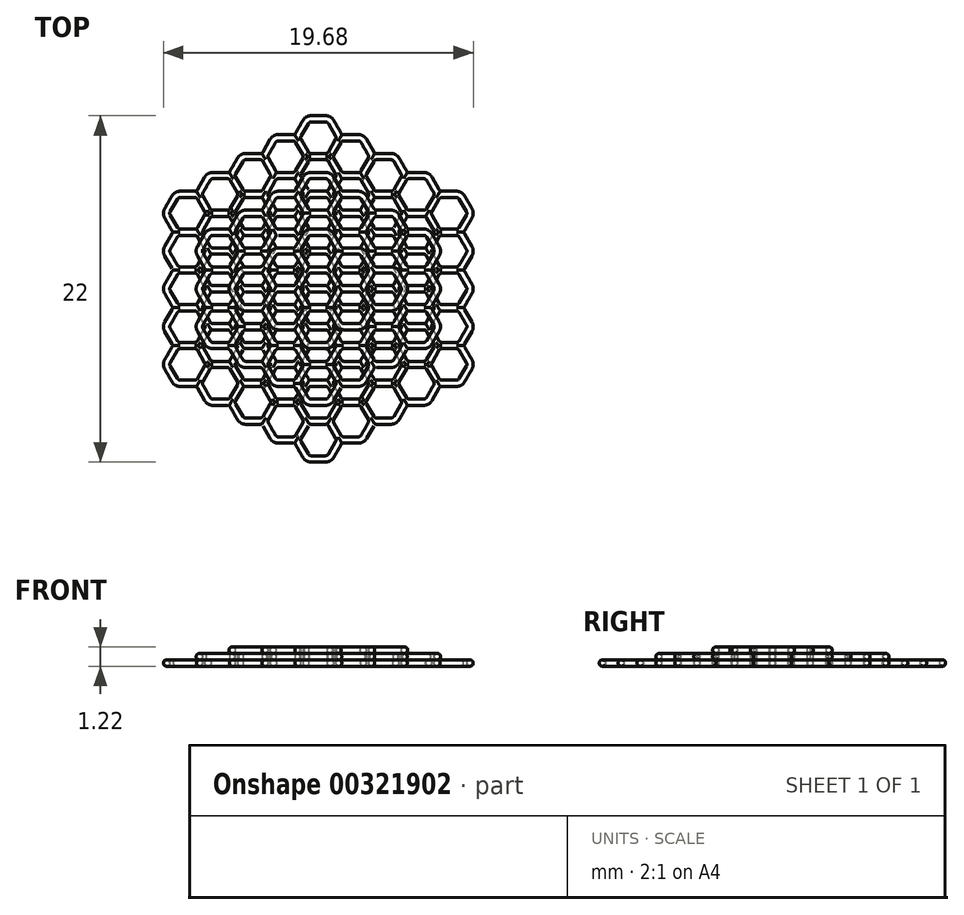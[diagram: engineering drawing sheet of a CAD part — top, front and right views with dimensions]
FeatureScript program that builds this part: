
annotation { "Feature Type Name" : "Feature", "Feature Type Description" : "" }
export const myFeature = defineFeature(function(context is Context, id is Id, definition is map)
    precondition{}
    {
        {
            var Q0;
            Q0=qCreatedBy(makeId("Top.planeOp"),FACE);
            cPlane(context, id + "F0", {"entities" : qUnion([Q0]), "cplaneType" : CPlaneType.OFFSET, "offset" : 0.2 * mm, "width" : 150 * mm, "height" : 150 * mm});
        }
        {
            var Q0;
            Q0=qCreatedBy(id+"F0.planeOp",FACE);
            var sketch = newSketch(context, id + "F1", { "sketchPlane" : qUnion([Q0])});
            skPoint(sketch, "E0.middle", {"position": v(0, 0) * mm});
            skLineSegment(sketch, "E1", {"start": v(-1.27, 0.2) * mm, "end": v(-0.8, 1) * mm});
            skLineSegment(sketch, "E2", {"start": v(-0.46, 1.2) * mm, "end": v(0.46, 1.2) * mm});
            skLineSegment(sketch, "E3", {"start": v(0.8, 1) * mm, "end": v(1.27, 0.2) * mm});
            skLineSegment(sketch, "E4", {"start": v(1.27, -0.2) * mm, "end": v(0.8, -1) * mm});
            skLineSegment(sketch, "E5", {"start": v(0.46, -1.2) * mm, "end": v(-0.46, -1.2) * mm});
            skLineSegment(sketch, "E6", {"start": v(-0.8, -1) * mm, "end": v(-1.27, -0.2) * mm});
            skArc(sketch, "E7.filletArc", {"start": v(-0.46, 1.2) * mm, "mid": v(-0.66, 1.15) * mm, "end": v(-0.8, 1) * mm});
            skArc(sketch, "E8.filletArc", {"start": v(0.8, 1) * mm, "mid": v(0.66, 1.15) * mm, "end": v(0.46, 1.2) * mm});
            skArc(sketch, "E9.filletArc", {"start": v(1.27, -0.2) * mm, "mid": v(1.32, 0) * mm, "end": v(1.27, 0.2) * mm});
            skArc(sketch, "E10.filletArc", {"start": v(0.46, -1.2) * mm, "mid": v(0.66, -1.15) * mm, "end": v(0.8, -1) * mm});
            skArc(sketch, "E11.filletArc", {"start": v(-0.8, -1) * mm, "mid": v(-0.66, -1.15) * mm, "end": v(-0.46, -1.2) * mm});
            skArc(sketch, "E12.filletArc", {"start": v(-1.27, 0.2) * mm, "mid": v(-1.32, 0) * mm, "end": v(-1.27, -0.2) * mm});
            skLineSegment(sketch, "E13", {"start": v(0.8, 1.4) * mm, "end": v(1.27, 2.2) * mm});
            skLineSegment(sketch, "E14", {"start": v(1.62, 2.4) * mm, "end": v(2.54, 2.4) * mm});
            skLineSegment(sketch, "E15", {"start": v(2.89, 2.2) * mm, "end": v(3.35, 1.4) * mm});
            skLineSegment(sketch, "E16", {"start": v(3.35, 1) * mm, "end": v(2.89, 0.2) * mm});
            skLineSegment(sketch, "E17", {"start": v(2.54, 0) * mm, "end": v(1.62, 0) * mm});
            skLineSegment(sketch, "E18", {"start": v(1.27, 0.2) * mm, "end": v(0.8, 1) * mm});
            skArc(sketch, "E19.filletArc", {"start": v(1.62, 2.4) * mm, "mid": v(1.42, 2.35) * mm, "end": v(1.27, 2.2) * mm});
            skArc(sketch, "E20.filletArc", {"start": v(2.89, 2.2) * mm, "mid": v(2.74, 2.35) * mm, "end": v(2.54, 2.4) * mm});
            skArc(sketch, "E21.filletArc", {"start": v(3.35, 1) * mm, "mid": v(3.4, 1.2) * mm, "end": v(3.35, 1.4) * mm});
            skArc(sketch, "E22.filletArc", {"start": v(2.54, 0) * mm, "mid": v(2.74, 0.05) * mm, "end": v(2.89, 0.2) * mm});
            skArc(sketch, "E23.filletArc", {"start": v(1.27, 0.2) * mm, "mid": v(1.42, 0.05) * mm, "end": v(1.62, 0) * mm});
            skArc(sketch, "E24.filletArc", {"start": v(0.8, 1.4) * mm, "mid": v(0.75, 1.2) * mm, "end": v(0.8, 1) * mm});
            skLineSegment(sketch, "E25", {"start": v(-1.27, 2.6) * mm, "end": v(-0.8, 3.4) * mm});
            skLineSegment(sketch, "E26", {"start": v(-0.46, 3.6) * mm, "end": v(0.46, 3.6) * mm});
            skLineSegment(sketch, "E27", {"start": v(0.8, 3.4) * mm, "end": v(1.27, 2.6) * mm});
            skLineSegment(sketch, "E28", {"start": v(1.27, 2.2) * mm, "end": v(0.8, 1.4) * mm});
            skLineSegment(sketch, "E29", {"start": v(0.46, 1.2) * mm, "end": v(-0.46, 1.2) * mm});
            skLineSegment(sketch, "E30", {"start": v(-0.8, 1.4) * mm, "end": v(-1.27, 2.2) * mm});
            skArc(sketch, "E31.filletArc", {"start": v(-0.46, 3.6) * mm, "mid": v(-0.66, 3.55) * mm, "end": v(-0.8, 3.4) * mm});
            skArc(sketch, "E32.filletArc", {"start": v(0.8, 3.4) * mm, "mid": v(0.66, 3.55) * mm, "end": v(0.46, 3.6) * mm});
            skArc(sketch, "E33.filletArc", {"start": v(1.27, 2.2) * mm, "mid": v(1.32, 2.4) * mm, "end": v(1.27, 2.6) * mm});
            skArc(sketch, "E34.filletArc", {"start": v(0.46, 1.2) * mm, "mid": v(0.66, 1.25) * mm, "end": v(0.8, 1.4) * mm});
            skArc(sketch, "E35.filletArc", {"start": v(-0.8, 1.4) * mm, "mid": v(-0.66, 1.25) * mm, "end": v(-0.46, 1.2) * mm});
            skArc(sketch, "E36.filletArc", {"start": v(-1.27, 2.6) * mm, "mid": v(-1.32, 2.4) * mm, "end": v(-1.27, 2.2) * mm});
            skLineSegment(sketch, "E37", {"start": v(-3.35, 1.4) * mm, "end": v(-2.89, 2.2) * mm});
            skLineSegment(sketch, "E38", {"start": v(-2.54, 2.4) * mm, "end": v(-1.62, 2.4) * mm});
            skLineSegment(sketch, "E39", {"start": v(-1.27, 2.2) * mm, "end": v(-0.8, 1.4) * mm});
            skLineSegment(sketch, "E40", {"start": v(-0.8, 1) * mm, "end": v(-1.27, 0.2) * mm});
            skLineSegment(sketch, "E41", {"start": v(-1.62, 0) * mm, "end": v(-2.54, 0) * mm});
            skLineSegment(sketch, "E42", {"start": v(-2.89, 0.2) * mm, "end": v(-3.35, 1) * mm});
            skArc(sketch, "E43.filletArc", {"start": v(-2.54, 2.4) * mm, "mid": v(-2.74, 2.35) * mm, "end": v(-2.89, 2.2) * mm});
            skArc(sketch, "E44.filletArc", {"start": v(-1.27, 2.2) * mm, "mid": v(-1.42, 2.35) * mm, "end": v(-1.62, 2.4) * mm});
            skArc(sketch, "E45.filletArc", {"start": v(-0.8, 1) * mm, "mid": v(-0.75, 1.2) * mm, "end": v(-0.8, 1.4) * mm});
            skArc(sketch, "E46.filletArc", {"start": v(-1.62, 0) * mm, "mid": v(-1.42, 0.05) * mm, "end": v(-1.27, 0.2) * mm});
            skArc(sketch, "E47.filletArc", {"start": v(-2.89, 0.2) * mm, "mid": v(-2.74, 0.05) * mm, "end": v(-2.54, 0) * mm});
            skArc(sketch, "E48.filletArc", {"start": v(-3.35, 1.4) * mm, "mid": v(-3.4, 1.2) * mm, "end": v(-3.35, 1) * mm});
            skLineSegment(sketch, "E49", {"start": v(-3.35, -1) * mm, "end": v(-2.89, -0.2) * mm});
            skLineSegment(sketch, "E50", {"start": v(-2.54, 0) * mm, "end": v(-1.62, 0) * mm});
            skLineSegment(sketch, "E51", {"start": v(-1.27, -0.2) * mm, "end": v(-0.8, -1) * mm});
            skLineSegment(sketch, "E52", {"start": v(-0.8, -1.4) * mm, "end": v(-1.27, -2.2) * mm});
            skLineSegment(sketch, "E53", {"start": v(-1.62, -2.4) * mm, "end": v(-2.54, -2.4) * mm});
            skLineSegment(sketch, "E54", {"start": v(-2.89, -2.2) * mm, "end": v(-3.35, -1.4) * mm});
            skArc(sketch, "E55.filletArc", {"start": v(-2.54, 0) * mm, "mid": v(-2.74, -0.05) * mm, "end": v(-2.89, -0.2) * mm});
            skArc(sketch, "E56.filletArc", {"start": v(-1.27, -0.2) * mm, "mid": v(-1.42, -0.05) * mm, "end": v(-1.62, 0) * mm});
            skArc(sketch, "E57.filletArc", {"start": v(-0.8, -1.4) * mm, "mid": v(-0.75, -1.2) * mm, "end": v(-0.8, -1) * mm});
            skArc(sketch, "E58.filletArc", {"start": v(-1.62, -2.4) * mm, "mid": v(-1.42, -2.35) * mm, "end": v(-1.27, -2.2) * mm});
            skArc(sketch, "E59.filletArc", {"start": v(-2.89, -2.2) * mm, "mid": v(-2.74, -2.35) * mm, "end": v(-2.54, -2.4) * mm});
            skArc(sketch, "E60.filletArc", {"start": v(-3.35, -1) * mm, "mid": v(-3.4, -1.2) * mm, "end": v(-3.35, -1.4) * mm});
            skLineSegment(sketch, "E61", {"start": v(-1.27, -2.2) * mm, "end": v(-0.8, -1.4) * mm});
            skLineSegment(sketch, "E62", {"start": v(-0.46, -1.2) * mm, "end": v(0.46, -1.2) * mm});
            skLineSegment(sketch, "E63", {"start": v(0.8, -1.4) * mm, "end": v(1.27, -2.2) * mm});
            skLineSegment(sketch, "E64", {"start": v(1.27, -2.6) * mm, "end": v(0.8, -3.4) * mm});
            skLineSegment(sketch, "E65", {"start": v(0.46, -3.6) * mm, "end": v(-0.46, -3.6) * mm});
            skLineSegment(sketch, "E66", {"start": v(-0.8, -3.4) * mm, "end": v(-1.27, -2.6) * mm});
            skArc(sketch, "E67.filletArc", {"start": v(-0.46, -1.2) * mm, "mid": v(-0.66, -1.25) * mm, "end": v(-0.8, -1.4) * mm});
            skArc(sketch, "E68.filletArc", {"start": v(0.8, -1.4) * mm, "mid": v(0.66, -1.25) * mm, "end": v(0.46, -1.2) * mm});
            skArc(sketch, "E69.filletArc", {"start": v(1.27, -2.6) * mm, "mid": v(1.32, -2.4) * mm, "end": v(1.27, -2.2) * mm});
            skArc(sketch, "E70.filletArc", {"start": v(0.46, -3.6) * mm, "mid": v(0.66, -3.55) * mm, "end": v(0.8, -3.4) * mm});
            skArc(sketch, "E71.filletArc", {"start": v(-0.8, -3.4) * mm, "mid": v(-0.66, -3.55) * mm, "end": v(-0.46, -3.6) * mm});
            skArc(sketch, "E72.filletArc", {"start": v(-1.27, -2.2) * mm, "mid": v(-1.32, -2.4) * mm, "end": v(-1.27, -2.6) * mm});
            skLineSegment(sketch, "E73", {"start": v(0.8, -1) * mm, "end": v(1.27, -0.2) * mm});
            skLineSegment(sketch, "E74", {"start": v(1.62, 0) * mm, "end": v(2.54, 0) * mm});
            skLineSegment(sketch, "E75", {"start": v(2.89, -0.2) * mm, "end": v(3.35, -1) * mm});
            skLineSegment(sketch, "E76", {"start": v(3.35, -1.4) * mm, "end": v(2.89, -2.2) * mm});
            skLineSegment(sketch, "E77", {"start": v(2.54, -2.4) * mm, "end": v(1.62, -2.4) * mm});
            skLineSegment(sketch, "E78", {"start": v(1.27, -2.2) * mm, "end": v(0.8, -1.4) * mm});
            skArc(sketch, "E79.filletArc", {"start": v(1.62, 0) * mm, "mid": v(1.42, -0.05) * mm, "end": v(1.27, -0.2) * mm});
            skArc(sketch, "E80.filletArc", {"start": v(2.89, -0.2) * mm, "mid": v(2.74, -0.05) * mm, "end": v(2.54, 0) * mm});
            skArc(sketch, "E81.filletArc", {"start": v(3.35, -1.4) * mm, "mid": v(3.4, -1.2) * mm, "end": v(3.35, -1) * mm});
            skArc(sketch, "E82.filletArc", {"start": v(2.54, -2.4) * mm, "mid": v(2.74, -2.35) * mm, "end": v(2.89, -2.2) * mm});
            skArc(sketch, "E83.filletArc", {"start": v(1.27, -2.2) * mm, "mid": v(1.42, -2.35) * mm, "end": v(1.62, -2.4) * mm});
            skArc(sketch, "E84.filletArc", {"start": v(0.8, -1) * mm, "mid": v(0.75, -1.2) * mm, "end": v(0.8, -1.4) * mm});
            skLineSegment(sketch, "E85", {"start": v(2.89, 2.6) * mm, "end": v(3.35, 3.4) * mm});
            skLineSegment(sketch, "E86", {"start": v(3.7, 3.6) * mm, "end": v(4.62, 3.6) * mm});
            skLineSegment(sketch, "E87", {"start": v(4.97, 3.4) * mm, "end": v(5.43, 2.6) * mm});
            skLineSegment(sketch, "E88", {"start": v(5.43, 2.2) * mm, "end": v(4.97, 1.4) * mm});
            skLineSegment(sketch, "E89", {"start": v(4.62, 1.2) * mm, "end": v(3.7, 1.2) * mm});
            skLineSegment(sketch, "E90", {"start": v(3.35, 1.4) * mm, "end": v(2.89, 2.2) * mm});
            skArc(sketch, "E91.filletArc", {"start": v(3.7, 3.6) * mm, "mid": v(3.5, 3.55) * mm, "end": v(3.35, 3.4) * mm});
            skArc(sketch, "E92.filletArc", {"start": v(4.97, 3.4) * mm, "mid": v(4.82, 3.55) * mm, "end": v(4.62, 3.6) * mm});
            skArc(sketch, "E93.filletArc", {"start": v(5.43, 2.2) * mm, "mid": v(5.48, 2.4) * mm, "end": v(5.43, 2.6) * mm});
            skArc(sketch, "E94.filletArc", {"start": v(4.62, 1.2) * mm, "mid": v(4.82, 1.25) * mm, "end": v(4.97, 1.4) * mm});
            skArc(sketch, "E95.filletArc", {"start": v(3.35, 1.4) * mm, "mid": v(3.5, 1.25) * mm, "end": v(3.7, 1.2) * mm});
            skArc(sketch, "E96.filletArc", {"start": v(2.89, 2.6) * mm, "mid": v(2.83, 2.4) * mm, "end": v(2.89, 2.2) * mm});
            skLineSegment(sketch, "E97", {"start": v(0.8, 3.8) * mm, "end": v(1.27, 4.6) * mm});
            skLineSegment(sketch, "E98", {"start": v(1.62, 4.8) * mm, "end": v(2.54, 4.8) * mm});
            skLineSegment(sketch, "E99", {"start": v(2.89, 4.6) * mm, "end": v(3.35, 3.8) * mm});
            skLineSegment(sketch, "E100", {"start": v(3.35, 3.4) * mm, "end": v(2.89, 2.6) * mm});
            skLineSegment(sketch, "E101", {"start": v(2.54, 2.4) * mm, "end": v(1.62, 2.4) * mm});
            skLineSegment(sketch, "E102", {"start": v(1.27, 2.6) * mm, "end": v(0.8, 3.4) * mm});
            skArc(sketch, "E103.filletArc", {"start": v(1.62, 4.8) * mm, "mid": v(1.42, 4.75) * mm, "end": v(1.27, 4.6) * mm});
            skArc(sketch, "E104.filletArc", {"start": v(2.89, 4.6) * mm, "mid": v(2.74, 4.75) * mm, "end": v(2.54, 4.8) * mm});
            skArc(sketch, "E105.filletArc", {"start": v(3.35, 3.4) * mm, "mid": v(3.4, 3.6) * mm, "end": v(3.35, 3.8) * mm});
            skArc(sketch, "E106.filletArc", {"start": v(2.54, 2.4) * mm, "mid": v(2.74, 2.45) * mm, "end": v(2.89, 2.6) * mm});
            skArc(sketch, "E107.filletArc", {"start": v(1.27, 2.6) * mm, "mid": v(1.42, 2.45) * mm, "end": v(1.62, 2.4) * mm});
            skArc(sketch, "E108.filletArc", {"start": v(0.8, 3.8) * mm, "mid": v(0.75, 3.6) * mm, "end": v(0.8, 3.4) * mm});
            skLineSegment(sketch, "E109", {"start": v(2.89, 0.2) * mm, "end": v(3.35, 1) * mm});
            skLineSegment(sketch, "E110", {"start": v(3.7, 1.2) * mm, "end": v(4.62, 1.2) * mm});
            skLineSegment(sketch, "E111", {"start": v(4.97, 1) * mm, "end": v(5.43, 0.2) * mm});
            skLineSegment(sketch, "E112", {"start": v(5.43, -0.2) * mm, "end": v(4.97, -1) * mm});
            skLineSegment(sketch, "E113", {"start": v(4.62, -1.2) * mm, "end": v(3.7, -1.2) * mm});
            skLineSegment(sketch, "E114", {"start": v(3.35, -1) * mm, "end": v(2.89, -0.2) * mm});
            skArc(sketch, "E115.filletArc", {"start": v(3.7, 1.2) * mm, "mid": v(3.5, 1.15) * mm, "end": v(3.35, 1) * mm});
            skArc(sketch, "E116.filletArc", {"start": v(4.97, 1) * mm, "mid": v(4.82, 1.15) * mm, "end": v(4.62, 1.2) * mm});
            skArc(sketch, "E117.filletArc", {"start": v(5.43, -0.2) * mm, "mid": v(5.48, 0) * mm, "end": v(5.43, 0.2) * mm});
            skArc(sketch, "E118.filletArc", {"start": v(4.62, -1.2) * mm, "mid": v(4.82, -1.15) * mm, "end": v(4.97, -1) * mm});
            skArc(sketch, "E119.filletArc", {"start": v(3.35, -1) * mm, "mid": v(3.5, -1.15) * mm, "end": v(3.7, -1.2) * mm});
            skArc(sketch, "E120.filletArc", {"start": v(2.89, 0.2) * mm, "mid": v(2.83, 0) * mm, "end": v(2.89, -0.2) * mm});
            skLineSegment(sketch, "E121", {"start": v(2.89, -2.2) * mm, "end": v(3.35, -1.4) * mm});
            skLineSegment(sketch, "E122", {"start": v(3.7, -1.2) * mm, "end": v(4.62, -1.2) * mm});
            skLineSegment(sketch, "E123", {"start": v(4.97, -1.4) * mm, "end": v(5.43, -2.2) * mm});
            skLineSegment(sketch, "E124", {"start": v(5.43, -2.6) * mm, "end": v(4.97, -3.4) * mm});
            skLineSegment(sketch, "E125", {"start": v(4.62, -3.6) * mm, "end": v(3.7, -3.6) * mm});
            skLineSegment(sketch, "E126", {"start": v(3.35, -3.4) * mm, "end": v(2.89, -2.6) * mm});
            skArc(sketch, "E127.filletArc", {"start": v(3.7, -1.2) * mm, "mid": v(3.5, -1.25) * mm, "end": v(3.35, -1.4) * mm});
            skArc(sketch, "E128.filletArc", {"start": v(4.97, -1.4) * mm, "mid": v(4.82, -1.25) * mm, "end": v(4.62, -1.2) * mm});
            skArc(sketch, "E129.filletArc", {"start": v(5.43, -2.6) * mm, "mid": v(5.48, -2.4) * mm, "end": v(5.43, -2.2) * mm});
            skArc(sketch, "E130.filletArc", {"start": v(4.62, -3.6) * mm, "mid": v(4.82, -3.55) * mm, "end": v(4.97, -3.4) * mm});
            skArc(sketch, "E131.filletArc", {"start": v(3.35, -3.4) * mm, "mid": v(3.5, -3.55) * mm, "end": v(3.7, -3.6) * mm});
            skArc(sketch, "E132.filletArc", {"start": v(2.89, -2.2) * mm, "mid": v(2.83, -2.4) * mm, "end": v(2.89, -2.6) * mm});
            skLineSegment(sketch, "E133", {"start": v(0.8, -3.4) * mm, "end": v(1.27, -2.6) * mm});
            skLineSegment(sketch, "E134", {"start": v(1.62, -2.4) * mm, "end": v(2.54, -2.4) * mm});
            skLineSegment(sketch, "E135", {"start": v(2.89, -2.6) * mm, "end": v(3.35, -3.4) * mm});
            skLineSegment(sketch, "E136", {"start": v(3.35, -3.8) * mm, "end": v(2.89, -4.6) * mm});
            skLineSegment(sketch, "E137", {"start": v(2.54, -4.8) * mm, "end": v(1.62, -4.8) * mm});
            skLineSegment(sketch, "E138", {"start": v(1.27, -4.6) * mm, "end": v(0.8, -3.8) * mm});
            skArc(sketch, "E139.filletArc", {"start": v(1.62, -2.4) * mm, "mid": v(1.42, -2.45) * mm, "end": v(1.27, -2.6) * mm});
            skArc(sketch, "E140.filletArc", {"start": v(2.89, -2.6) * mm, "mid": v(2.74, -2.45) * mm, "end": v(2.54, -2.4) * mm});
            skArc(sketch, "E141.filletArc", {"start": v(3.35, -3.8) * mm, "mid": v(3.4, -3.6) * mm, "end": v(3.35, -3.4) * mm});
            skArc(sketch, "E142.filletArc", {"start": v(2.54, -4.8) * mm, "mid": v(2.74, -4.75) * mm, "end": v(2.89, -4.6) * mm});
            skArc(sketch, "E143.filletArc", {"start": v(1.27, -4.6) * mm, "mid": v(1.42, -4.75) * mm, "end": v(1.62, -4.8) * mm});
            skArc(sketch, "E144.filletArc", {"start": v(0.8, -3.4) * mm, "mid": v(0.75, -3.6) * mm, "end": v(0.8, -3.8) * mm});
            skLineSegment(sketch, "E145", {"start": v(-1.27, -4.6) * mm, "end": v(-0.8, -3.8) * mm});
            skLineSegment(sketch, "E146", {"start": v(-0.46, -3.6) * mm, "end": v(0.46, -3.6) * mm});
            skLineSegment(sketch, "E147", {"start": v(0.8, -3.8) * mm, "end": v(1.27, -4.6) * mm});
            skLineSegment(sketch, "E148", {"start": v(1.27, -5) * mm, "end": v(0.8, -5.8) * mm});
            skLineSegment(sketch, "E149", {"start": v(0.46, -6) * mm, "end": v(-0.46, -6) * mm});
            skLineSegment(sketch, "E150", {"start": v(-0.8, -5.8) * mm, "end": v(-1.27, -5) * mm});
            skArc(sketch, "E151.filletArc", {"start": v(-0.46, -3.6) * mm, "mid": v(-0.66, -3.65) * mm, "end": v(-0.8, -3.8) * mm});
            skArc(sketch, "E152.filletArc", {"start": v(0.8, -3.8) * mm, "mid": v(0.66, -3.65) * mm, "end": v(0.46, -3.6) * mm});
            skArc(sketch, "E153.filletArc", {"start": v(1.27, -5) * mm, "mid": v(1.32, -4.8) * mm, "end": v(1.27, -4.6) * mm});
            skArc(sketch, "E154.filletArc", {"start": v(0.46, -6) * mm, "mid": v(0.66, -5.95) * mm, "end": v(0.8, -5.8) * mm});
            skArc(sketch, "E155.filletArc", {"start": v(-0.8, -5.8) * mm, "mid": v(-0.66, -5.95) * mm, "end": v(-0.46, -6) * mm});
            skArc(sketch, "E156.filletArc", {"start": v(-1.27, -4.6) * mm, "mid": v(-1.32, -4.8) * mm, "end": v(-1.27, -5) * mm});
            skLineSegment(sketch, "E157", {"start": v(-3.35, -3.4) * mm, "end": v(-2.89, -2.6) * mm});
            skLineSegment(sketch, "E158", {"start": v(-2.54, -2.4) * mm, "end": v(-1.62, -2.4) * mm});
            skLineSegment(sketch, "E159", {"start": v(-1.27, -2.6) * mm, "end": v(-0.8, -3.4) * mm});
            skLineSegment(sketch, "E160", {"start": v(-0.8, -3.8) * mm, "end": v(-1.27, -4.6) * mm});
            skLineSegment(sketch, "E161", {"start": v(-1.62, -4.8) * mm, "end": v(-2.54, -4.8) * mm});
            skLineSegment(sketch, "E162", {"start": v(-2.89, -4.6) * mm, "end": v(-3.35, -3.8) * mm});
            skArc(sketch, "E163.filletArc", {"start": v(-2.54, -2.4) * mm, "mid": v(-2.74, -2.45) * mm, "end": v(-2.89, -2.6) * mm});
            skArc(sketch, "E164.filletArc", {"start": v(-1.27, -2.6) * mm, "mid": v(-1.42, -2.45) * mm, "end": v(-1.62, -2.4) * mm});
            skArc(sketch, "E165.filletArc", {"start": v(-0.8, -3.8) * mm, "mid": v(-0.75, -3.6) * mm, "end": v(-0.8, -3.4) * mm});
            skArc(sketch, "E166.filletArc", {"start": v(-1.62, -4.8) * mm, "mid": v(-1.42, -4.75) * mm, "end": v(-1.27, -4.6) * mm});
            skArc(sketch, "E167.filletArc", {"start": v(-2.89, -4.6) * mm, "mid": v(-2.74, -4.75) * mm, "end": v(-2.54, -4.8) * mm});
            skArc(sketch, "E168.filletArc", {"start": v(-3.35, -3.4) * mm, "mid": v(-3.4, -3.6) * mm, "end": v(-3.35, -3.8) * mm});
            skLineSegment(sketch, "E169", {"start": v(-5.43, -2.2) * mm, "end": v(-4.97, -1.4) * mm});
            skLineSegment(sketch, "E170", {"start": v(-4.62, -1.2) * mm, "end": v(-3.7, -1.2) * mm});
            skLineSegment(sketch, "E171", {"start": v(-3.35, -1.4) * mm, "end": v(-2.89, -2.2) * mm});
            skLineSegment(sketch, "E172", {"start": v(-2.89, -2.6) * mm, "end": v(-3.35, -3.4) * mm});
            skLineSegment(sketch, "E173", {"start": v(-3.7, -3.6) * mm, "end": v(-4.62, -3.6) * mm});
            skLineSegment(sketch, "E174", {"start": v(-4.97, -3.4) * mm, "end": v(-5.43, -2.6) * mm});
            skArc(sketch, "E175.filletArc", {"start": v(-4.62, -1.2) * mm, "mid": v(-4.82, -1.25) * mm, "end": v(-4.97, -1.4) * mm});
            skArc(sketch, "E176.filletArc", {"start": v(-3.35, -1.4) * mm, "mid": v(-3.5, -1.25) * mm, "end": v(-3.7, -1.2) * mm});
            skArc(sketch, "E177.filletArc", {"start": v(-2.89, -2.6) * mm, "mid": v(-2.83, -2.4) * mm, "end": v(-2.89, -2.2) * mm});
            skArc(sketch, "E178.filletArc", {"start": v(-3.7, -3.6) * mm, "mid": v(-3.5, -3.55) * mm, "end": v(-3.35, -3.4) * mm});
            skArc(sketch, "E179.filletArc", {"start": v(-4.97, -3.4) * mm, "mid": v(-4.82, -3.55) * mm, "end": v(-4.62, -3.6) * mm});
            skArc(sketch, "E180.filletArc", {"start": v(-5.43, -2.2) * mm, "mid": v(-5.48, -2.4) * mm, "end": v(-5.43, -2.6) * mm});
            skLineSegment(sketch, "E181", {"start": v(-5.43, 0.2) * mm, "end": v(-4.97, 1) * mm});
            skLineSegment(sketch, "E182", {"start": v(-4.62, 1.2) * mm, "end": v(-3.7, 1.2) * mm});
            skLineSegment(sketch, "E183", {"start": v(-3.35, 1) * mm, "end": v(-2.89, 0.2) * mm});
            skLineSegment(sketch, "E184", {"start": v(-2.89, -0.2) * mm, "end": v(-3.35, -1) * mm});
            skLineSegment(sketch, "E185", {"start": v(-3.7, -1.2) * mm, "end": v(-4.62, -1.2) * mm});
            skLineSegment(sketch, "E186", {"start": v(-4.97, -1) * mm, "end": v(-5.43, -0.2) * mm});
            skArc(sketch, "E187.filletArc", {"start": v(-4.62, 1.2) * mm, "mid": v(-4.82, 1.15) * mm, "end": v(-4.97, 1) * mm});
            skArc(sketch, "E188.filletArc", {"start": v(-3.35, 1) * mm, "mid": v(-3.5, 1.15) * mm, "end": v(-3.7, 1.2) * mm});
            skArc(sketch, "E189.filletArc", {"start": v(-2.89, -0.2) * mm, "mid": v(-2.83, 0) * mm, "end": v(-2.89, 0.2) * mm});
            skArc(sketch, "E190.filletArc", {"start": v(-3.7, -1.2) * mm, "mid": v(-3.5, -1.15) * mm, "end": v(-3.35, -1) * mm});
            skArc(sketch, "E191.filletArc", {"start": v(-4.97, -1) * mm, "mid": v(-4.82, -1.15) * mm, "end": v(-4.62, -1.2) * mm});
            skArc(sketch, "E192.filletArc", {"start": v(-5.43, 0.2) * mm, "mid": v(-5.48, 0) * mm, "end": v(-5.43, -0.2) * mm});
            skLineSegment(sketch, "E193", {"start": v(-5.43, 2.6) * mm, "end": v(-4.97, 3.4) * mm});
            skLineSegment(sketch, "E194", {"start": v(-4.62, 3.6) * mm, "end": v(-3.7, 3.6) * mm});
            skLineSegment(sketch, "E195", {"start": v(-3.35, 3.4) * mm, "end": v(-2.89, 2.6) * mm});
            skLineSegment(sketch, "E196", {"start": v(-2.89, 2.2) * mm, "end": v(-3.35, 1.4) * mm});
            skLineSegment(sketch, "E197", {"start": v(-3.7, 1.2) * mm, "end": v(-4.62, 1.2) * mm});
            skLineSegment(sketch, "E198", {"start": v(-4.97, 1.4) * mm, "end": v(-5.43, 2.2) * mm});
            skArc(sketch, "E199.filletArc", {"start": v(-4.62, 3.6) * mm, "mid": v(-4.82, 3.55) * mm, "end": v(-4.97, 3.4) * mm});
            skArc(sketch, "E200.filletArc", {"start": v(-3.35, 3.4) * mm, "mid": v(-3.5, 3.55) * mm, "end": v(-3.7, 3.6) * mm});
            skArc(sketch, "E201.filletArc", {"start": v(-2.89, 2.2) * mm, "mid": v(-2.83, 2.4) * mm, "end": v(-2.89, 2.6) * mm});
            skArc(sketch, "E202.filletArc", {"start": v(-3.7, 1.2) * mm, "mid": v(-3.5, 1.25) * mm, "end": v(-3.35, 1.4) * mm});
            skArc(sketch, "E203.filletArc", {"start": v(-4.97, 1.4) * mm, "mid": v(-4.82, 1.25) * mm, "end": v(-4.62, 1.2) * mm});
            skArc(sketch, "E204.filletArc", {"start": v(-5.43, 2.6) * mm, "mid": v(-5.48, 2.4) * mm, "end": v(-5.43, 2.2) * mm});
            skLineSegment(sketch, "E205", {"start": v(-3.35, 3.8) * mm, "end": v(-2.89, 4.6) * mm});
            skLineSegment(sketch, "E206", {"start": v(-2.54, 4.8) * mm, "end": v(-1.62, 4.8) * mm});
            skLineSegment(sketch, "E207", {"start": v(-1.27, 4.6) * mm, "end": v(-0.8, 3.8) * mm});
            skLineSegment(sketch, "E208", {"start": v(-0.8, 3.4) * mm, "end": v(-1.27, 2.6) * mm});
            skLineSegment(sketch, "E209", {"start": v(-1.62, 2.4) * mm, "end": v(-2.54, 2.4) * mm});
            skLineSegment(sketch, "E210", {"start": v(-2.89, 2.6) * mm, "end": v(-3.35, 3.4) * mm});
            skArc(sketch, "E211.filletArc", {"start": v(-2.54, 4.8) * mm, "mid": v(-2.74, 4.75) * mm, "end": v(-2.89, 4.6) * mm});
            skArc(sketch, "E212.filletArc", {"start": v(-1.27, 4.6) * mm, "mid": v(-1.42, 4.75) * mm, "end": v(-1.62, 4.8) * mm});
            skArc(sketch, "E213.filletArc", {"start": v(-0.8, 3.4) * mm, "mid": v(-0.75, 3.6) * mm, "end": v(-0.8, 3.8) * mm});
            skArc(sketch, "E214.filletArc", {"start": v(-1.62, 2.4) * mm, "mid": v(-1.42, 2.45) * mm, "end": v(-1.27, 2.6) * mm});
            skArc(sketch, "E215.filletArc", {"start": v(-2.89, 2.6) * mm, "mid": v(-2.74, 2.45) * mm, "end": v(-2.54, 2.4) * mm});
            skArc(sketch, "E216.filletArc", {"start": v(-3.35, 3.8) * mm, "mid": v(-3.4, 3.6) * mm, "end": v(-3.35, 3.4) * mm});
            skLineSegment(sketch, "E217", {"start": v(-1.27, 5) * mm, "end": v(-0.8, 5.8) * mm});
            skLineSegment(sketch, "E218", {"start": v(-0.46, 6) * mm, "end": v(0.46, 6) * mm});
            skLineSegment(sketch, "E219", {"start": v(0.8, 5.8) * mm, "end": v(1.27, 5) * mm});
            skLineSegment(sketch, "E220", {"start": v(1.27, 4.6) * mm, "end": v(0.8, 3.8) * mm});
            skLineSegment(sketch, "E221", {"start": v(0.46, 3.6) * mm, "end": v(-0.46, 3.6) * mm});
            skLineSegment(sketch, "E222", {"start": v(-0.8, 3.8) * mm, "end": v(-1.27, 4.6) * mm});
            skArc(sketch, "E223.filletArc", {"start": v(-0.46, 6) * mm, "mid": v(-0.66, 5.95) * mm, "end": v(-0.8, 5.8) * mm});
            skArc(sketch, "E224.filletArc", {"start": v(0.8, 5.8) * mm, "mid": v(0.66, 5.95) * mm, "end": v(0.46, 6) * mm});
            skArc(sketch, "E225.filletArc", {"start": v(1.27, 4.6) * mm, "mid": v(1.32, 4.8) * mm, "end": v(1.27, 5) * mm});
            skArc(sketch, "E226.filletArc", {"start": v(0.46, 3.6) * mm, "mid": v(0.66, 3.65) * mm, "end": v(0.8, 3.8) * mm});
            skArc(sketch, "E227.filletArc", {"start": v(-0.8, 3.8) * mm, "mid": v(-0.66, 3.65) * mm, "end": v(-0.46, 3.6) * mm});
            skArc(sketch, "E228.filletArc", {"start": v(-1.27, 5) * mm, "mid": v(-1.32, 4.8) * mm, "end": v(-1.27, 4.6) * mm});
            skLineSegment(sketch, "E229", {"start": v(2.89, 5) * mm, "end": v(3.35, 5.8) * mm});
            skLineSegment(sketch, "E230", {"start": v(3.7, 6) * mm, "end": v(4.62, 6) * mm});
            skLineSegment(sketch, "E231", {"start": v(4.97, 5.8) * mm, "end": v(5.43, 5) * mm});
            skLineSegment(sketch, "E232", {"start": v(5.43, 4.6) * mm, "end": v(4.97, 3.8) * mm});
            skLineSegment(sketch, "E233", {"start": v(4.62, 3.6) * mm, "end": v(3.7, 3.6) * mm});
            skLineSegment(sketch, "E234", {"start": v(3.35, 3.8) * mm, "end": v(2.89, 4.6) * mm});
            skArc(sketch, "E235.filletArc", {"start": v(3.7, 6) * mm, "mid": v(3.5, 5.95) * mm, "end": v(3.35, 5.8) * mm});
            skArc(sketch, "E236.filletArc", {"start": v(4.97, 5.8) * mm, "mid": v(4.82, 5.95) * mm, "end": v(4.62, 6) * mm});
            skArc(sketch, "E237.filletArc", {"start": v(5.43, 4.6) * mm, "mid": v(5.48, 4.8) * mm, "end": v(5.43, 5) * mm});
            skArc(sketch, "E238.filletArc", {"start": v(4.62, 3.6) * mm, "mid": v(4.82, 3.65) * mm, "end": v(4.97, 3.8) * mm});
            skArc(sketch, "E239.filletArc", {"start": v(3.35, 3.8) * mm, "mid": v(3.5, 3.65) * mm, "end": v(3.7, 3.6) * mm});
            skArc(sketch, "E240.filletArc", {"start": v(2.89, 5) * mm, "mid": v(2.83, 4.8) * mm, "end": v(2.89, 4.6) * mm});
            skLineSegment(sketch, "E241", {"start": v(0.8, 6.2) * mm, "end": v(1.27, 7) * mm});
            skLineSegment(sketch, "E242", {"start": v(1.62, 7.2) * mm, "end": v(2.54, 7.2) * mm});
            skLineSegment(sketch, "E243", {"start": v(2.89, 7) * mm, "end": v(3.35, 6.2) * mm});
            skLineSegment(sketch, "E244", {"start": v(3.35, 5.8) * mm, "end": v(2.89, 5) * mm});
            skLineSegment(sketch, "E245", {"start": v(2.54, 4.8) * mm, "end": v(1.62, 4.8) * mm});
            skLineSegment(sketch, "E246", {"start": v(1.27, 5) * mm, "end": v(0.8, 5.8) * mm});
            skArc(sketch, "E247.filletArc", {"start": v(1.62, 7.2) * mm, "mid": v(1.42, 7.15) * mm, "end": v(1.27, 7) * mm});
            skArc(sketch, "E248.filletArc", {"start": v(2.89, 7) * mm, "mid": v(2.74, 7.15) * mm, "end": v(2.54, 7.2) * mm});
            skArc(sketch, "E249.filletArc", {"start": v(3.35, 5.8) * mm, "mid": v(3.4, 6) * mm, "end": v(3.35, 6.2) * mm});
            skArc(sketch, "E250.filletArc", {"start": v(2.54, 4.8) * mm, "mid": v(2.74, 4.85) * mm, "end": v(2.89, 5) * mm});
            skArc(sketch, "E251.filletArc", {"start": v(1.27, 5) * mm, "mid": v(1.42, 4.85) * mm, "end": v(1.62, 4.8) * mm});
            skArc(sketch, "E252.filletArc", {"start": v(0.8, 6.2) * mm, "mid": v(0.75, 6) * mm, "end": v(0.8, 5.8) * mm});
            skLineSegment(sketch, "E253", {"start": v(-1.27, 7.4) * mm, "end": v(-0.8, 8.2) * mm});
            skLineSegment(sketch, "E254", {"start": v(-0.46, 8.4) * mm, "end": v(0.46, 8.4) * mm});
            skLineSegment(sketch, "E255", {"start": v(0.8, 8.2) * mm, "end": v(1.27, 7.4) * mm});
            skLineSegment(sketch, "E256", {"start": v(1.27, 7) * mm, "end": v(0.8, 6.2) * mm});
            skLineSegment(sketch, "E257", {"start": v(0.46, 6) * mm, "end": v(-0.46, 6) * mm});
            skLineSegment(sketch, "E258", {"start": v(-0.8, 6.2) * mm, "end": v(-1.27, 7) * mm});
            skArc(sketch, "E259.filletArc", {"start": v(-0.46, 8.4) * mm, "mid": v(-0.66, 8.35) * mm, "end": v(-0.8, 8.2) * mm});
            skArc(sketch, "E260.filletArc", {"start": v(0.8, 8.2) * mm, "mid": v(0.66, 8.35) * mm, "end": v(0.46, 8.4) * mm});
            skArc(sketch, "E261.filletArc", {"start": v(1.27, 7) * mm, "mid": v(1.32, 7.2) * mm, "end": v(1.27, 7.4) * mm});
            skArc(sketch, "E262.filletArc", {"start": v(0.46, 6) * mm, "mid": v(0.66, 6.05) * mm, "end": v(0.8, 6.2) * mm});
            skArc(sketch, "E263.filletArc", {"start": v(-0.8, 6.2) * mm, "mid": v(-0.66, 6.05) * mm, "end": v(-0.46, 6) * mm});
            skArc(sketch, "E264.filletArc", {"start": v(-1.27, 7.4) * mm, "mid": v(-1.32, 7.2) * mm, "end": v(-1.27, 7) * mm});
            skLineSegment(sketch, "E265", {"start": v(-3.35, 6.2) * mm, "end": v(-2.89, 7) * mm});
            skLineSegment(sketch, "E266", {"start": v(-2.54, 7.2) * mm, "end": v(-1.62, 7.2) * mm});
            skLineSegment(sketch, "E267", {"start": v(-1.27, 7) * mm, "end": v(-0.8, 6.2) * mm});
            skLineSegment(sketch, "E268", {"start": v(-0.8, 5.8) * mm, "end": v(-1.27, 5) * mm});
            skLineSegment(sketch, "E269", {"start": v(-1.62, 4.8) * mm, "end": v(-2.54, 4.8) * mm});
            skLineSegment(sketch, "E270", {"start": v(-2.89, 5) * mm, "end": v(-3.35, 5.8) * mm});
            skArc(sketch, "E271.filletArc", {"start": v(-2.54, 7.2) * mm, "mid": v(-2.74, 7.15) * mm, "end": v(-2.89, 7) * mm});
            skArc(sketch, "E272.filletArc", {"start": v(-1.27, 7) * mm, "mid": v(-1.42, 7.15) * mm, "end": v(-1.62, 7.2) * mm});
            skArc(sketch, "E273.filletArc", {"start": v(-0.8, 5.8) * mm, "mid": v(-0.75, 6) * mm, "end": v(-0.8, 6.2) * mm});
            skArc(sketch, "E274.filletArc", {"start": v(-1.62, 4.8) * mm, "mid": v(-1.42, 4.85) * mm, "end": v(-1.27, 5) * mm});
            skArc(sketch, "E275.filletArc", {"start": v(-2.89, 5) * mm, "mid": v(-2.74, 4.85) * mm, "end": v(-2.54, 4.8) * mm});
            skArc(sketch, "E276.filletArc", {"start": v(-3.35, 6.2) * mm, "mid": v(-3.4, 6) * mm, "end": v(-3.35, 5.8) * mm});
            skLineSegment(sketch, "E277", {"start": v(-5.43, 5) * mm, "end": v(-4.97, 5.8) * mm});
            skLineSegment(sketch, "E278", {"start": v(-4.62, 6) * mm, "end": v(-3.7, 6) * mm});
            skLineSegment(sketch, "E279", {"start": v(-3.35, 5.8) * mm, "end": v(-2.89, 5) * mm});
            skLineSegment(sketch, "E280", {"start": v(-2.89, 4.6) * mm, "end": v(-3.35, 3.8) * mm});
            skLineSegment(sketch, "E281", {"start": v(-3.7, 3.6) * mm, "end": v(-4.62, 3.6) * mm});
            skLineSegment(sketch, "E282", {"start": v(-4.97, 3.8) * mm, "end": v(-5.43, 4.6) * mm});
            skArc(sketch, "E283.filletArc", {"start": v(-4.62, 6) * mm, "mid": v(-4.82, 5.95) * mm, "end": v(-4.97, 5.8) * mm});
            skArc(sketch, "E284.filletArc", {"start": v(-3.35, 5.8) * mm, "mid": v(-3.5, 5.95) * mm, "end": v(-3.7, 6) * mm});
            skArc(sketch, "E285.filletArc", {"start": v(-2.89, 4.6) * mm, "mid": v(-2.83, 4.8) * mm, "end": v(-2.89, 5) * mm});
            skArc(sketch, "E286.filletArc", {"start": v(-3.7, 3.6) * mm, "mid": v(-3.5, 3.65) * mm, "end": v(-3.35, 3.8) * mm});
            skArc(sketch, "E287.filletArc", {"start": v(-4.97, 3.8) * mm, "mid": v(-4.82, 3.65) * mm, "end": v(-4.62, 3.6) * mm});
            skArc(sketch, "E288.filletArc", {"start": v(-5.43, 5) * mm, "mid": v(-5.48, 4.8) * mm, "end": v(-5.43, 4.6) * mm});
            skLineSegment(sketch, "E289", {"start": v(-7.5, 3.8) * mm, "end": v(-7.04, 4.6) * mm});
            skLineSegment(sketch, "E290", {"start": v(-6.7, 4.8) * mm, "end": v(-5.77, 4.8) * mm});
            skLineSegment(sketch, "E291", {"start": v(-5.43, 4.6) * mm, "end": v(-4.97, 3.8) * mm});
            skLineSegment(sketch, "E292", {"start": v(-4.97, 3.4) * mm, "end": v(-5.43, 2.6) * mm});
            skLineSegment(sketch, "E293", {"start": v(-5.77, 2.4) * mm, "end": v(-6.7, 2.4) * mm});
            skLineSegment(sketch, "E294", {"start": v(-7.04, 2.6) * mm, "end": v(-7.5, 3.4) * mm});
            skArc(sketch, "E295.filletArc", {"start": v(-6.7, 4.8) * mm, "mid": v(-6.9, 4.75) * mm, "end": v(-7.04, 4.6) * mm});
            skArc(sketch, "E296.filletArc", {"start": v(-5.43, 4.6) * mm, "mid": v(-5.57, 4.75) * mm, "end": v(-5.77, 4.8) * mm});
            skArc(sketch, "E297.filletArc", {"start": v(-4.97, 3.4) * mm, "mid": v(-4.91, 3.6) * mm, "end": v(-4.97, 3.8) * mm});
            skArc(sketch, "E298.filletArc", {"start": v(-5.77, 2.4) * mm, "mid": v(-5.57, 2.45) * mm, "end": v(-5.43, 2.6) * mm});
            skArc(sketch, "E299.filletArc", {"start": v(-7.04, 2.6) * mm, "mid": v(-6.9, 2.45) * mm, "end": v(-6.7, 2.4) * mm});
            skArc(sketch, "E300.filletArc", {"start": v(-7.5, 3.8) * mm, "mid": v(-7.56, 3.6) * mm, "end": v(-7.5, 3.4) * mm});
            skLineSegment(sketch, "E301", {"start": v(-7.5, 1.4) * mm, "end": v(-7.04, 2.2) * mm});
            skLineSegment(sketch, "E302", {"start": v(-6.7, 2.4) * mm, "end": v(-5.77, 2.4) * mm});
            skLineSegment(sketch, "E303", {"start": v(-5.43, 2.2) * mm, "end": v(-4.97, 1.4) * mm});
            skLineSegment(sketch, "E304", {"start": v(-4.97, 1) * mm, "end": v(-5.43, 0.2) * mm});
            skLineSegment(sketch, "E305", {"start": v(-5.77, 0) * mm, "end": v(-6.7, 0) * mm});
            skLineSegment(sketch, "E306", {"start": v(-7.04, 0.2) * mm, "end": v(-7.5, 1) * mm});
            skArc(sketch, "E307.filletArc", {"start": v(-6.7, 2.4) * mm, "mid": v(-6.9, 2.35) * mm, "end": v(-7.04, 2.2) * mm});
            skArc(sketch, "E308.filletArc", {"start": v(-5.43, 2.2) * mm, "mid": v(-5.57, 2.35) * mm, "end": v(-5.77, 2.4) * mm});
            skArc(sketch, "E309.filletArc", {"start": v(-4.97, 1) * mm, "mid": v(-4.91, 1.2) * mm, "end": v(-4.97, 1.4) * mm});
            skArc(sketch, "E310.filletArc", {"start": v(-5.77, 0) * mm, "mid": v(-5.57, 0.05) * mm, "end": v(-5.43, 0.2) * mm});
            skArc(sketch, "E311.filletArc", {"start": v(-7.04, 0.2) * mm, "mid": v(-6.9, 0.05) * mm, "end": v(-6.7, 0) * mm});
            skArc(sketch, "E312.filletArc", {"start": v(-7.5, 1.4) * mm, "mid": v(-7.56, 1.2) * mm, "end": v(-7.5, 1) * mm});
            skLineSegment(sketch, "E313", {"start": v(-7.5, -1) * mm, "end": v(-7.04, -0.2) * mm});
            skLineSegment(sketch, "E314", {"start": v(-6.7, 0) * mm, "end": v(-5.77, 0) * mm});
            skLineSegment(sketch, "E315", {"start": v(-5.43, -0.2) * mm, "end": v(-4.97, -1) * mm});
            skLineSegment(sketch, "E316", {"start": v(-4.97, -1.4) * mm, "end": v(-5.43, -2.2) * mm});
            skLineSegment(sketch, "E317", {"start": v(-5.77, -2.4) * mm, "end": v(-6.7, -2.4) * mm});
            skLineSegment(sketch, "E318", {"start": v(-7.04, -2.2) * mm, "end": v(-7.5, -1.4) * mm});
            skArc(sketch, "E319.filletArc", {"start": v(-6.7, 0) * mm, "mid": v(-6.9, -0.05) * mm, "end": v(-7.04, -0.2) * mm});
            skArc(sketch, "E320.filletArc", {"start": v(-5.43, -0.2) * mm, "mid": v(-5.57, -0.05) * mm, "end": v(-5.77, 0) * mm});
            skArc(sketch, "E321.filletArc", {"start": v(-4.97, -1.4) * mm, "mid": v(-4.91, -1.2) * mm, "end": v(-4.97, -1) * mm});
            skArc(sketch, "E322.filletArc", {"start": v(-5.77, -2.4) * mm, "mid": v(-5.57, -2.35) * mm, "end": v(-5.43, -2.2) * mm});
            skArc(sketch, "E323.filletArc", {"start": v(-7.04, -2.2) * mm, "mid": v(-6.9, -2.35) * mm, "end": v(-6.7, -2.4) * mm});
            skArc(sketch, "E324.filletArc", {"start": v(-7.5, -1) * mm, "mid": v(-7.56, -1.2) * mm, "end": v(-7.5, -1.4) * mm});
            skLineSegment(sketch, "E325", {"start": v(-7.5, -3.4) * mm, "end": v(-7.04, -2.6) * mm});
            skLineSegment(sketch, "E326", {"start": v(-6.7, -2.4) * mm, "end": v(-5.77, -2.4) * mm});
            skLineSegment(sketch, "E327", {"start": v(-5.43, -2.6) * mm, "end": v(-4.97, -3.4) * mm});
            skLineSegment(sketch, "E328", {"start": v(-4.97, -3.8) * mm, "end": v(-5.43, -4.6) * mm});
            skLineSegment(sketch, "E329", {"start": v(-5.77, -4.8) * mm, "end": v(-6.7, -4.8) * mm});
            skLineSegment(sketch, "E330", {"start": v(-7.04, -4.6) * mm, "end": v(-7.5, -3.8) * mm});
            skArc(sketch, "E331.filletArc", {"start": v(-6.7, -2.4) * mm, "mid": v(-6.9, -2.45) * mm, "end": v(-7.04, -2.6) * mm});
            skArc(sketch, "E332.filletArc", {"start": v(-5.43, -2.6) * mm, "mid": v(-5.57, -2.45) * mm, "end": v(-5.77, -2.4) * mm});
            skArc(sketch, "E333.filletArc", {"start": v(-4.97, -3.8) * mm, "mid": v(-4.91, -3.6) * mm, "end": v(-4.97, -3.4) * mm});
            skArc(sketch, "E334.filletArc", {"start": v(-5.77, -4.8) * mm, "mid": v(-5.57, -4.75) * mm, "end": v(-5.43, -4.6) * mm});
            skArc(sketch, "E335.filletArc", {"start": v(-7.04, -4.6) * mm, "mid": v(-6.9, -4.75) * mm, "end": v(-6.7, -4.8) * mm});
            skArc(sketch, "E336.filletArc", {"start": v(-7.5, -3.4) * mm, "mid": v(-7.56, -3.6) * mm, "end": v(-7.5, -3.8) * mm});
            skLineSegment(sketch, "E337", {"start": v(-3.35, -5.8) * mm, "end": v(-2.89, -5) * mm});
            skLineSegment(sketch, "E338", {"start": v(-2.54, -4.8) * mm, "end": v(-1.62, -4.8) * mm});
            skLineSegment(sketch, "E339", {"start": v(-1.27, -5) * mm, "end": v(-0.8, -5.8) * mm});
            skLineSegment(sketch, "E340", {"start": v(-0.8, -6.2) * mm, "end": v(-1.27, -7) * mm});
            skLineSegment(sketch, "E341", {"start": v(-1.62, -7.2) * mm, "end": v(-2.54, -7.2) * mm});
            skLineSegment(sketch, "E342", {"start": v(-2.89, -7) * mm, "end": v(-3.35, -6.2) * mm});
            skArc(sketch, "E343.filletArc", {"start": v(-2.54, -4.8) * mm, "mid": v(-2.74, -4.85) * mm, "end": v(-2.89, -5) * mm});
            skArc(sketch, "E344.filletArc", {"start": v(-1.27, -5) * mm, "mid": v(-1.42, -4.85) * mm, "end": v(-1.62, -4.8) * mm});
            skArc(sketch, "E345.filletArc", {"start": v(-0.8, -6.2) * mm, "mid": v(-0.75, -6) * mm, "end": v(-0.8, -5.8) * mm});
            skArc(sketch, "E346.filletArc", {"start": v(-1.62, -7.2) * mm, "mid": v(-1.42, -7.15) * mm, "end": v(-1.27, -7) * mm});
            skArc(sketch, "E347.filletArc", {"start": v(-2.89, -7) * mm, "mid": v(-2.74, -7.15) * mm, "end": v(-2.54, -7.2) * mm});
            skArc(sketch, "E348.filletArc", {"start": v(-3.35, -5.8) * mm, "mid": v(-3.4, -6) * mm, "end": v(-3.35, -6.2) * mm});
            skLineSegment(sketch, "E349", {"start": v(-5.43, -4.6) * mm, "end": v(-4.97, -3.8) * mm});
            skLineSegment(sketch, "E350", {"start": v(-4.62, -3.6) * mm, "end": v(-3.7, -3.6) * mm});
            skLineSegment(sketch, "E351", {"start": v(-3.35, -3.8) * mm, "end": v(-2.89, -4.6) * mm});
            skLineSegment(sketch, "E352", {"start": v(-2.89, -5) * mm, "end": v(-3.35, -5.8) * mm});
            skLineSegment(sketch, "E353", {"start": v(-3.7, -6) * mm, "end": v(-4.62, -6) * mm});
            skLineSegment(sketch, "E354", {"start": v(-4.97, -5.8) * mm, "end": v(-5.43, -5) * mm});
            skArc(sketch, "E355.filletArc", {"start": v(-4.62, -3.6) * mm, "mid": v(-4.82, -3.65) * mm, "end": v(-4.97, -3.8) * mm});
            skArc(sketch, "E356.filletArc", {"start": v(-3.35, -3.8) * mm, "mid": v(-3.5, -3.65) * mm, "end": v(-3.7, -3.6) * mm});
            skArc(sketch, "E357.filletArc", {"start": v(-2.89, -5) * mm, "mid": v(-2.83, -4.8) * mm, "end": v(-2.89, -4.6) * mm});
            skArc(sketch, "E358.filletArc", {"start": v(-3.7, -6) * mm, "mid": v(-3.5, -5.95) * mm, "end": v(-3.35, -5.8) * mm});
            skArc(sketch, "E359.filletArc", {"start": v(-4.97, -5.8) * mm, "mid": v(-4.82, -5.95) * mm, "end": v(-4.62, -6) * mm});
            skArc(sketch, "E360.filletArc", {"start": v(-5.43, -4.6) * mm, "mid": v(-5.48, -4.8) * mm, "end": v(-5.43, -5) * mm});
            skLineSegment(sketch, "E361", {"start": v(-1.27, -7) * mm, "end": v(-0.8, -6.2) * mm});
            skLineSegment(sketch, "E362", {"start": v(-0.46, -6) * mm, "end": v(0.46, -6) * mm});
            skLineSegment(sketch, "E363", {"start": v(0.8, -6.2) * mm, "end": v(1.27, -7) * mm});
            skLineSegment(sketch, "E364", {"start": v(1.27, -7.4) * mm, "end": v(0.8, -8.2) * mm});
            skLineSegment(sketch, "E365", {"start": v(0.46, -8.4) * mm, "end": v(-0.46, -8.4) * mm});
            skLineSegment(sketch, "E366", {"start": v(-0.8, -8.2) * mm, "end": v(-1.27, -7.4) * mm});
            skArc(sketch, "E367.filletArc", {"start": v(-0.46, -6) * mm, "mid": v(-0.66, -6.05) * mm, "end": v(-0.8, -6.2) * mm});
            skArc(sketch, "E368.filletArc", {"start": v(0.8, -6.2) * mm, "mid": v(0.66, -6.05) * mm, "end": v(0.46, -6) * mm});
            skArc(sketch, "E369.filletArc", {"start": v(1.27, -7.4) * mm, "mid": v(1.32, -7.2) * mm, "end": v(1.27, -7) * mm});
            skArc(sketch, "E370.filletArc", {"start": v(0.46, -8.4) * mm, "mid": v(0.66, -8.35) * mm, "end": v(0.8, -8.2) * mm});
            skArc(sketch, "E371.filletArc", {"start": v(-0.8, -8.2) * mm, "mid": v(-0.66, -8.35) * mm, "end": v(-0.46, -8.4) * mm});
            skArc(sketch, "E372.filletArc", {"start": v(-1.27, -7) * mm, "mid": v(-1.32, -7.2) * mm, "end": v(-1.27, -7.4) * mm});
            skLineSegment(sketch, "E373", {"start": v(0.8, -5.8) * mm, "end": v(1.27, -5) * mm});
            skLineSegment(sketch, "E374", {"start": v(1.62, -4.8) * mm, "end": v(2.54, -4.8) * mm});
            skLineSegment(sketch, "E375", {"start": v(2.89, -5) * mm, "end": v(3.35, -5.8) * mm});
            skLineSegment(sketch, "E376", {"start": v(3.35, -6.2) * mm, "end": v(2.89, -7) * mm});
            skLineSegment(sketch, "E377", {"start": v(2.54, -7.2) * mm, "end": v(1.62, -7.2) * mm});
            skLineSegment(sketch, "E378", {"start": v(1.27, -7) * mm, "end": v(0.8, -6.2) * mm});
            skArc(sketch, "E379.filletArc", {"start": v(1.62, -4.8) * mm, "mid": v(1.42, -4.85) * mm, "end": v(1.27, -5) * mm});
            skArc(sketch, "E380.filletArc", {"start": v(2.89, -5) * mm, "mid": v(2.74, -4.85) * mm, "end": v(2.54, -4.8) * mm});
            skArc(sketch, "E381.filletArc", {"start": v(3.35, -6.2) * mm, "mid": v(3.4, -6) * mm, "end": v(3.35, -5.8) * mm});
            skArc(sketch, "E382.filletArc", {"start": v(2.54, -7.2) * mm, "mid": v(2.74, -7.15) * mm, "end": v(2.89, -7) * mm});
            skArc(sketch, "E383.filletArc", {"start": v(1.27, -7) * mm, "mid": v(1.42, -7.15) * mm, "end": v(1.62, -7.2) * mm});
            skArc(sketch, "E384.filletArc", {"start": v(0.8, -5.8) * mm, "mid": v(0.75, -6) * mm, "end": v(0.8, -6.2) * mm});
            skLineSegment(sketch, "E385", {"start": v(2.89, -4.6) * mm, "end": v(3.35, -3.8) * mm});
            skLineSegment(sketch, "E386", {"start": v(3.7, -3.6) * mm, "end": v(4.62, -3.6) * mm});
            skLineSegment(sketch, "E387", {"start": v(4.97, -3.8) * mm, "end": v(5.43, -4.6) * mm});
            skLineSegment(sketch, "E388", {"start": v(5.43, -5) * mm, "end": v(4.97, -5.8) * mm});
            skLineSegment(sketch, "E389", {"start": v(4.62, -6) * mm, "end": v(3.7, -6) * mm});
            skLineSegment(sketch, "E390", {"start": v(3.35, -5.8) * mm, "end": v(2.89, -5) * mm});
            skArc(sketch, "E391.filletArc", {"start": v(3.7, -3.6) * mm, "mid": v(3.5, -3.65) * mm, "end": v(3.35, -3.8) * mm});
            skArc(sketch, "E392.filletArc", {"start": v(4.97, -3.8) * mm, "mid": v(4.82, -3.65) * mm, "end": v(4.62, -3.6) * mm});
            skArc(sketch, "E393.filletArc", {"start": v(5.43, -5) * mm, "mid": v(5.48, -4.8) * mm, "end": v(5.43, -4.6) * mm});
            skArc(sketch, "E394.filletArc", {"start": v(4.62, -6) * mm, "mid": v(4.82, -5.95) * mm, "end": v(4.97, -5.8) * mm});
            skArc(sketch, "E395.filletArc", {"start": v(3.35, -5.8) * mm, "mid": v(3.5, -5.95) * mm, "end": v(3.7, -6) * mm});
            skArc(sketch, "E396.filletArc", {"start": v(2.89, -4.6) * mm, "mid": v(2.83, -4.8) * mm, "end": v(2.89, -5) * mm});
            skLineSegment(sketch, "E397", {"start": v(4.97, -3.4) * mm, "end": v(5.43, -2.6) * mm});
            skLineSegment(sketch, "E398", {"start": v(5.77, -2.4) * mm, "end": v(6.7, -2.4) * mm});
            skLineSegment(sketch, "E399", {"start": v(7.04, -2.6) * mm, "end": v(7.5, -3.4) * mm});
            skLineSegment(sketch, "E400", {"start": v(7.5, -3.8) * mm, "end": v(7.04, -4.6) * mm});
            skLineSegment(sketch, "E401", {"start": v(6.7, -4.8) * mm, "end": v(5.77, -4.8) * mm});
            skLineSegment(sketch, "E402", {"start": v(5.43, -4.6) * mm, "end": v(4.97, -3.8) * mm});
            skArc(sketch, "E403.filletArc", {"start": v(5.77, -2.4) * mm, "mid": v(5.57, -2.45) * mm, "end": v(5.43, -2.6) * mm});
            skArc(sketch, "E404.filletArc", {"start": v(7.04, -2.6) * mm, "mid": v(6.9, -2.45) * mm, "end": v(6.7, -2.4) * mm});
            skArc(sketch, "E405.filletArc", {"start": v(7.5, -3.8) * mm, "mid": v(7.56, -3.6) * mm, "end": v(7.5, -3.4) * mm});
            skArc(sketch, "E406.filletArc", {"start": v(6.7, -4.8) * mm, "mid": v(6.9, -4.75) * mm, "end": v(7.04, -4.6) * mm});
            skArc(sketch, "E407.filletArc", {"start": v(5.43, -4.6) * mm, "mid": v(5.57, -4.75) * mm, "end": v(5.77, -4.8) * mm});
            skArc(sketch, "E408.filletArc", {"start": v(4.97, -3.4) * mm, "mid": v(4.91, -3.6) * mm, "end": v(4.97, -3.8) * mm});
            skLineSegment(sketch, "E409", {"start": v(4.97, -1) * mm, "end": v(5.43, -0.2) * mm});
            skLineSegment(sketch, "E410", {"start": v(5.77, 0) * mm, "end": v(6.7, 0) * mm});
            skLineSegment(sketch, "E411", {"start": v(7.04, -0.2) * mm, "end": v(7.5, -1) * mm});
            skLineSegment(sketch, "E412", {"start": v(7.5, -1.4) * mm, "end": v(7.04, -2.2) * mm});
            skLineSegment(sketch, "E413", {"start": v(6.7, -2.4) * mm, "end": v(5.77, -2.4) * mm});
            skLineSegment(sketch, "E414", {"start": v(5.43, -2.2) * mm, "end": v(4.97, -1.4) * mm});
            skArc(sketch, "E415.filletArc", {"start": v(5.77, 0) * mm, "mid": v(5.57, -0.05) * mm, "end": v(5.43, -0.2) * mm});
            skArc(sketch, "E416.filletArc", {"start": v(7.04, -0.2) * mm, "mid": v(6.9, -0.05) * mm, "end": v(6.7, 0) * mm});
            skArc(sketch, "E417.filletArc", {"start": v(7.5, -1.4) * mm, "mid": v(7.56, -1.2) * mm, "end": v(7.5, -1) * mm});
            skArc(sketch, "E418.filletArc", {"start": v(6.7, -2.4) * mm, "mid": v(6.9, -2.35) * mm, "end": v(7.04, -2.2) * mm});
            skArc(sketch, "E419.filletArc", {"start": v(5.43, -2.2) * mm, "mid": v(5.57, -2.35) * mm, "end": v(5.77, -2.4) * mm});
            skArc(sketch, "E420.filletArc", {"start": v(4.97, -1) * mm, "mid": v(4.91, -1.2) * mm, "end": v(4.97, -1.4) * mm});
            skLineSegment(sketch, "E421", {"start": v(4.97, 1.4) * mm, "end": v(5.43, 2.2) * mm});
            skLineSegment(sketch, "E422", {"start": v(5.77, 2.4) * mm, "end": v(6.7, 2.4) * mm});
            skLineSegment(sketch, "E423", {"start": v(7.04, 2.2) * mm, "end": v(7.5, 1.4) * mm});
            skLineSegment(sketch, "E424", {"start": v(7.5, 1) * mm, "end": v(7.04, 0.2) * mm});
            skLineSegment(sketch, "E425", {"start": v(6.7, 0) * mm, "end": v(5.77, 0) * mm});
            skLineSegment(sketch, "E426", {"start": v(5.43, 0.2) * mm, "end": v(4.97, 1) * mm});
            skArc(sketch, "E427.filletArc", {"start": v(5.77, 2.4) * mm, "mid": v(5.57, 2.35) * mm, "end": v(5.43, 2.2) * mm});
            skArc(sketch, "E428.filletArc", {"start": v(7.04, 2.2) * mm, "mid": v(6.9, 2.35) * mm, "end": v(6.7, 2.4) * mm});
            skArc(sketch, "E429.filletArc", {"start": v(7.5, 1) * mm, "mid": v(7.56, 1.2) * mm, "end": v(7.5, 1.4) * mm});
            skArc(sketch, "E430.filletArc", {"start": v(6.7, 0) * mm, "mid": v(6.9, 0.05) * mm, "end": v(7.04, 0.2) * mm});
            skArc(sketch, "E431.filletArc", {"start": v(5.43, 0.2) * mm, "mid": v(5.57, 0.05) * mm, "end": v(5.77, 0) * mm});
            skArc(sketch, "E432.filletArc", {"start": v(4.97, 1.4) * mm, "mid": v(4.91, 1.2) * mm, "end": v(4.97, 1) * mm});
            skLineSegment(sketch, "E433", {"start": v(4.97, 3.8) * mm, "end": v(5.43, 4.6) * mm});
            skLineSegment(sketch, "E434", {"start": v(5.77, 4.8) * mm, "end": v(6.7, 4.8) * mm});
            skLineSegment(sketch, "E435", {"start": v(7.04, 4.6) * mm, "end": v(7.5, 3.8) * mm});
            skLineSegment(sketch, "E436", {"start": v(7.5, 3.4) * mm, "end": v(7.04, 2.6) * mm});
            skLineSegment(sketch, "E437", {"start": v(6.7, 2.4) * mm, "end": v(5.77, 2.4) * mm});
            skLineSegment(sketch, "E438", {"start": v(5.43, 2.6) * mm, "end": v(4.97, 3.4) * mm});
            skArc(sketch, "E439.filletArc", {"start": v(5.77, 4.8) * mm, "mid": v(5.57, 4.75) * mm, "end": v(5.43, 4.6) * mm});
            skArc(sketch, "E440.filletArc", {"start": v(7.04, 4.6) * mm, "mid": v(6.9, 4.75) * mm, "end": v(6.7, 4.8) * mm});
            skArc(sketch, "E441.filletArc", {"start": v(7.5, 3.4) * mm, "mid": v(7.56, 3.6) * mm, "end": v(7.5, 3.8) * mm});
            skArc(sketch, "E442.filletArc", {"start": v(6.7, 2.4) * mm, "mid": v(6.9, 2.45) * mm, "end": v(7.04, 2.6) * mm});
            skArc(sketch, "E443.filletArc", {"start": v(5.43, 2.6) * mm, "mid": v(5.57, 2.45) * mm, "end": v(5.77, 2.4) * mm});
            skArc(sketch, "E444.filletArc", {"start": v(4.97, 3.8) * mm, "mid": v(4.91, 3.6) * mm, "end": v(4.97, 3.4) * mm});
            skLineSegment(sketch, "E445", {"start": v(0.8, 8.6) * mm, "end": v(1.27, 9.4) * mm});
            skLineSegment(sketch, "E446", {"start": v(1.62, 9.6) * mm, "end": v(2.54, 9.6) * mm});
            skLineSegment(sketch, "E447", {"start": v(2.89, 9.4) * mm, "end": v(3.35, 8.6) * mm});
            skLineSegment(sketch, "E448", {"start": v(3.35, 8.2) * mm, "end": v(2.89, 7.4) * mm});
            skLineSegment(sketch, "E449", {"start": v(2.54, 7.2) * mm, "end": v(1.62, 7.2) * mm});
            skLineSegment(sketch, "E450", {"start": v(1.27, 7.4) * mm, "end": v(0.8, 8.2) * mm});
            skArc(sketch, "E451.filletArc", {"start": v(1.62, 9.6) * mm, "mid": v(1.42, 9.55) * mm, "end": v(1.27, 9.4) * mm});
            skArc(sketch, "E452.filletArc", {"start": v(2.89, 9.4) * mm, "mid": v(2.74, 9.55) * mm, "end": v(2.54, 9.6) * mm});
            skArc(sketch, "E453.filletArc", {"start": v(3.35, 8.2) * mm, "mid": v(3.4, 8.4) * mm, "end": v(3.35, 8.6) * mm});
            skArc(sketch, "E454.filletArc", {"start": v(2.54, 7.2) * mm, "mid": v(2.74, 7.25) * mm, "end": v(2.89, 7.4) * mm});
            skArc(sketch, "E455.filletArc", {"start": v(1.27, 7.4) * mm, "mid": v(1.42, 7.25) * mm, "end": v(1.62, 7.2) * mm});
            skArc(sketch, "E456.filletArc", {"start": v(0.8, 8.6) * mm, "mid": v(0.75, 8.4) * mm, "end": v(0.8, 8.2) * mm});
            skLineSegment(sketch, "E457", {"start": v(2.89, 7.4) * mm, "end": v(3.35, 8.2) * mm});
            skLineSegment(sketch, "E458", {"start": v(3.7, 8.4) * mm, "end": v(4.62, 8.4) * mm});
            skLineSegment(sketch, "E459", {"start": v(4.97, 8.2) * mm, "end": v(5.43, 7.4) * mm});
            skLineSegment(sketch, "E460", {"start": v(5.43, 7) * mm, "end": v(4.97, 6.2) * mm});
            skLineSegment(sketch, "E461", {"start": v(4.62, 6) * mm, "end": v(3.7, 6) * mm});
            skLineSegment(sketch, "E462", {"start": v(3.35, 6.2) * mm, "end": v(2.89, 7) * mm});
            skArc(sketch, "E463.filletArc", {"start": v(3.7, 8.4) * mm, "mid": v(3.5, 8.35) * mm, "end": v(3.35, 8.2) * mm});
            skArc(sketch, "E464.filletArc", {"start": v(4.97, 8.2) * mm, "mid": v(4.82, 8.35) * mm, "end": v(4.62, 8.4) * mm});
            skArc(sketch, "E465.filletArc", {"start": v(5.43, 7) * mm, "mid": v(5.48, 7.2) * mm, "end": v(5.43, 7.4) * mm});
            skArc(sketch, "E466.filletArc", {"start": v(4.62, 6) * mm, "mid": v(4.82, 6.05) * mm, "end": v(4.97, 6.2) * mm});
            skArc(sketch, "E467.filletArc", {"start": v(3.35, 6.2) * mm, "mid": v(3.5, 6.05) * mm, "end": v(3.7, 6) * mm});
            skArc(sketch, "E468.filletArc", {"start": v(2.89, 7.4) * mm, "mid": v(2.83, 7.2) * mm, "end": v(2.89, 7) * mm});
            skLineSegment(sketch, "E469", {"start": v(4.97, 6.2) * mm, "end": v(5.43, 7) * mm});
            skLineSegment(sketch, "E470", {"start": v(5.77, 7.2) * mm, "end": v(6.7, 7.2) * mm});
            skLineSegment(sketch, "E471", {"start": v(7.04, 7) * mm, "end": v(7.5, 6.2) * mm});
            skLineSegment(sketch, "E472", {"start": v(7.5, 5.8) * mm, "end": v(7.04, 5) * mm});
            skLineSegment(sketch, "E473", {"start": v(6.7, 4.8) * mm, "end": v(5.77, 4.8) * mm});
            skLineSegment(sketch, "E474", {"start": v(5.43, 5) * mm, "end": v(4.97, 5.8) * mm});
            skArc(sketch, "E475.filletArc", {"start": v(5.77, 7.2) * mm, "mid": v(5.57, 7.15) * mm, "end": v(5.43, 7) * mm});
            skArc(sketch, "E476.filletArc", {"start": v(7.04, 7) * mm, "mid": v(6.9, 7.15) * mm, "end": v(6.7, 7.2) * mm});
            skArc(sketch, "E477.filletArc", {"start": v(7.5, 5.8) * mm, "mid": v(7.56, 6) * mm, "end": v(7.5, 6.2) * mm});
            skArc(sketch, "E478.filletArc", {"start": v(6.7, 4.8) * mm, "mid": v(6.9, 4.85) * mm, "end": v(7.04, 5) * mm});
            skArc(sketch, "E479.filletArc", {"start": v(5.43, 5) * mm, "mid": v(5.57, 4.85) * mm, "end": v(5.77, 4.8) * mm});
            skArc(sketch, "E480.filletArc", {"start": v(4.97, 6.2) * mm, "mid": v(4.91, 6) * mm, "end": v(4.97, 5.8) * mm});
            skLineSegment(sketch, "E481", {"start": v(7.04, 5) * mm, "end": v(7.5, 5.8) * mm});
            skLineSegment(sketch, "E482", {"start": v(7.85, 6) * mm, "end": v(8.78, 6) * mm});
            skLineSegment(sketch, "E483", {"start": v(9.12, 5.8) * mm, "end": v(9.58, 5) * mm});
            skLineSegment(sketch, "E484", {"start": v(9.58, 4.6) * mm, "end": v(9.12, 3.8) * mm});
            skLineSegment(sketch, "E485", {"start": v(8.78, 3.6) * mm, "end": v(7.85, 3.6) * mm});
            skLineSegment(sketch, "E486", {"start": v(7.5, 3.8) * mm, "end": v(7.04, 4.6) * mm});
            skArc(sketch, "E487.filletArc", {"start": v(7.85, 6) * mm, "mid": v(7.65, 5.95) * mm, "end": v(7.5, 5.8) * mm});
            skArc(sketch, "E488.filletArc", {"start": v(9.12, 5.8) * mm, "mid": v(8.98, 5.95) * mm, "end": v(8.78, 6) * mm});
            skArc(sketch, "E489.filletArc", {"start": v(9.58, 4.6) * mm, "mid": v(9.64, 4.8) * mm, "end": v(9.58, 5) * mm});
            skArc(sketch, "E490.filletArc", {"start": v(8.78, 3.6) * mm, "mid": v(8.98, 3.65) * mm, "end": v(9.12, 3.8) * mm});
            skArc(sketch, "E491.filletArc", {"start": v(7.5, 3.8) * mm, "mid": v(7.65, 3.65) * mm, "end": v(7.85, 3.6) * mm});
            skArc(sketch, "E492.filletArc", {"start": v(7.04, 5) * mm, "mid": v(7, 4.8) * mm, "end": v(7.04, 4.6) * mm});
            skLineSegment(sketch, "E493", {"start": v(7.04, 2.6) * mm, "end": v(7.5, 3.4) * mm});
            skLineSegment(sketch, "E494", {"start": v(7.85, 3.6) * mm, "end": v(8.78, 3.6) * mm});
            skLineSegment(sketch, "E495", {"start": v(9.12, 3.4) * mm, "end": v(9.58, 2.6) * mm});
            skLineSegment(sketch, "E496", {"start": v(9.58, 2.2) * mm, "end": v(9.12, 1.4) * mm});
            skLineSegment(sketch, "E497", {"start": v(8.78, 1.2) * mm, "end": v(7.85, 1.2) * mm});
            skLineSegment(sketch, "E498", {"start": v(7.5, 1.4) * mm, "end": v(7.04, 2.2) * mm});
            skArc(sketch, "E499.filletArc", {"start": v(7.85, 3.6) * mm, "mid": v(7.65, 3.55) * mm, "end": v(7.5, 3.4) * mm});
            skArc(sketch, "E500.filletArc", {"start": v(9.12, 3.4) * mm, "mid": v(8.98, 3.55) * mm, "end": v(8.78, 3.6) * mm});
            skArc(sketch, "E501.filletArc", {"start": v(9.58, 2.2) * mm, "mid": v(9.64, 2.4) * mm, "end": v(9.58, 2.6) * mm});
            skArc(sketch, "E502.filletArc", {"start": v(8.78, 1.2) * mm, "mid": v(8.98, 1.25) * mm, "end": v(9.12, 1.4) * mm});
            skArc(sketch, "E503.filletArc", {"start": v(7.5, 1.4) * mm, "mid": v(7.65, 1.25) * mm, "end": v(7.85, 1.2) * mm});
            skArc(sketch, "E504.filletArc", {"start": v(7.04, 2.6) * mm, "mid": v(7, 2.4) * mm, "end": v(7.04, 2.2) * mm});
            skLineSegment(sketch, "E505", {"start": v(7.04, 0.2) * mm, "end": v(7.5, 1) * mm});
            skLineSegment(sketch, "E506", {"start": v(7.85, 1.2) * mm, "end": v(8.78, 1.2) * mm});
            skLineSegment(sketch, "E507", {"start": v(9.12, 1) * mm, "end": v(9.58, 0.2) * mm});
            skLineSegment(sketch, "E508", {"start": v(9.58, -0.2) * mm, "end": v(9.12, -1) * mm});
            skLineSegment(sketch, "E509", {"start": v(8.78, -1.2) * mm, "end": v(7.85, -1.2) * mm});
            skLineSegment(sketch, "E510", {"start": v(7.5, -1) * mm, "end": v(7.04, -0.2) * mm});
            skArc(sketch, "E511.filletArc", {"start": v(7.85, 1.2) * mm, "mid": v(7.65, 1.15) * mm, "end": v(7.5, 1) * mm});
            skArc(sketch, "E512.filletArc", {"start": v(9.12, 1) * mm, "mid": v(8.98, 1.15) * mm, "end": v(8.78, 1.2) * mm});
            skArc(sketch, "E513.filletArc", {"start": v(9.58, -0.2) * mm, "mid": v(9.64, 0) * mm, "end": v(9.58, 0.2) * mm});
            skArc(sketch, "E514.filletArc", {"start": v(8.78, -1.2) * mm, "mid": v(8.98, -1.15) * mm, "end": v(9.12, -1) * mm});
            skArc(sketch, "E515.filletArc", {"start": v(7.5, -1) * mm, "mid": v(7.65, -1.15) * mm, "end": v(7.85, -1.2) * mm});
            skArc(sketch, "E516.filletArc", {"start": v(7.04, 0.2) * mm, "mid": v(7, 0) * mm, "end": v(7.04, -0.2) * mm});
            skLineSegment(sketch, "E517", {"start": v(7.04, -2.2) * mm, "end": v(7.5, -1.4) * mm});
            skLineSegment(sketch, "E518", {"start": v(7.85, -1.2) * mm, "end": v(8.78, -1.2) * mm});
            skLineSegment(sketch, "E519", {"start": v(9.12, -1.4) * mm, "end": v(9.58, -2.2) * mm});
            skLineSegment(sketch, "E520", {"start": v(9.58, -2.6) * mm, "end": v(9.12, -3.4) * mm});
            skLineSegment(sketch, "E521", {"start": v(8.78, -3.6) * mm, "end": v(7.85, -3.6) * mm});
            skLineSegment(sketch, "E522", {"start": v(7.5, -3.4) * mm, "end": v(7.04, -2.6) * mm});
            skArc(sketch, "E523.filletArc", {"start": v(7.85, -1.2) * mm, "mid": v(7.65, -1.25) * mm, "end": v(7.5, -1.4) * mm});
            skArc(sketch, "E524.filletArc", {"start": v(9.12, -1.4) * mm, "mid": v(8.98, -1.25) * mm, "end": v(8.78, -1.2) * mm});
            skArc(sketch, "E525.filletArc", {"start": v(9.58, -2.6) * mm, "mid": v(9.64, -2.4) * mm, "end": v(9.58, -2.2) * mm});
            skArc(sketch, "E526.filletArc", {"start": v(8.78, -3.6) * mm, "mid": v(8.98, -3.55) * mm, "end": v(9.12, -3.4) * mm});
            skArc(sketch, "E527.filletArc", {"start": v(7.5, -3.4) * mm, "mid": v(7.65, -3.55) * mm, "end": v(7.85, -3.6) * mm});
            skArc(sketch, "E528.filletArc", {"start": v(7.04, -2.2) * mm, "mid": v(7, -2.4) * mm, "end": v(7.04, -2.6) * mm});
            skLineSegment(sketch, "E529", {"start": v(7.04, -4.6) * mm, "end": v(7.5, -3.8) * mm});
            skLineSegment(sketch, "E530", {"start": v(7.85, -3.6) * mm, "end": v(8.78, -3.6) * mm});
            skLineSegment(sketch, "E531", {"start": v(9.12, -3.8) * mm, "end": v(9.58, -4.6) * mm});
            skLineSegment(sketch, "E532", {"start": v(9.58, -5) * mm, "end": v(9.12, -5.8) * mm});
            skLineSegment(sketch, "E533", {"start": v(8.78, -6) * mm, "end": v(7.85, -6) * mm});
            skLineSegment(sketch, "E534", {"start": v(7.5, -5.8) * mm, "end": v(7.04, -5) * mm});
            skArc(sketch, "E535.filletArc", {"start": v(7.85, -3.6) * mm, "mid": v(7.65, -3.65) * mm, "end": v(7.5, -3.8) * mm});
            skArc(sketch, "E536.filletArc", {"start": v(9.12, -3.8) * mm, "mid": v(8.98, -3.65) * mm, "end": v(8.78, -3.6) * mm});
            skArc(sketch, "E537.filletArc", {"start": v(9.58, -5) * mm, "mid": v(9.64, -4.8) * mm, "end": v(9.58, -4.6) * mm});
            skArc(sketch, "E538.filletArc", {"start": v(8.78, -6) * mm, "mid": v(8.98, -5.95) * mm, "end": v(9.12, -5.8) * mm});
            skArc(sketch, "E539.filletArc", {"start": v(7.5, -5.8) * mm, "mid": v(7.65, -5.95) * mm, "end": v(7.85, -6) * mm});
            skArc(sketch, "E540.filletArc", {"start": v(7.04, -4.6) * mm, "mid": v(7, -4.8) * mm, "end": v(7.04, -5) * mm});
            skLineSegment(sketch, "E541", {"start": v(2.89, -7) * mm, "end": v(3.35, -6.2) * mm});
            skLineSegment(sketch, "E542", {"start": v(3.7, -6) * mm, "end": v(4.62, -6) * mm});
            skLineSegment(sketch, "E543", {"start": v(4.97, -6.2) * mm, "end": v(5.43, -7) * mm});
            skLineSegment(sketch, "E544", {"start": v(5.43, -7.4) * mm, "end": v(4.97, -8.2) * mm});
            skLineSegment(sketch, "E545", {"start": v(4.62, -8.4) * mm, "end": v(3.7, -8.4) * mm});
            skLineSegment(sketch, "E546", {"start": v(3.35, -8.2) * mm, "end": v(2.89, -7.4) * mm});
            skArc(sketch, "E547.filletArc", {"start": v(3.7, -6) * mm, "mid": v(3.5, -6.05) * mm, "end": v(3.35, -6.2) * mm});
            skArc(sketch, "E548.filletArc", {"start": v(4.97, -6.2) * mm, "mid": v(4.82, -6.05) * mm, "end": v(4.62, -6) * mm});
            skArc(sketch, "E549.filletArc", {"start": v(5.43, -7.4) * mm, "mid": v(5.48, -7.2) * mm, "end": v(5.43, -7) * mm});
            skArc(sketch, "E550.filletArc", {"start": v(4.62, -8.4) * mm, "mid": v(4.82, -8.35) * mm, "end": v(4.97, -8.2) * mm});
            skArc(sketch, "E551.filletArc", {"start": v(3.35, -8.2) * mm, "mid": v(3.5, -8.35) * mm, "end": v(3.7, -8.4) * mm});
            skArc(sketch, "E552.filletArc", {"start": v(2.89, -7) * mm, "mid": v(2.83, -7.2) * mm, "end": v(2.89, -7.4) * mm});
            skLineSegment(sketch, "E553", {"start": v(4.97, -5.8) * mm, "end": v(5.43, -5) * mm});
            skLineSegment(sketch, "E554", {"start": v(5.77, -4.8) * mm, "end": v(6.7, -4.8) * mm});
            skLineSegment(sketch, "E555", {"start": v(7.04, -5) * mm, "end": v(7.5, -5.8) * mm});
            skLineSegment(sketch, "E556", {"start": v(7.5, -6.2) * mm, "end": v(7.04, -7) * mm});
            skLineSegment(sketch, "E557", {"start": v(6.7, -7.2) * mm, "end": v(5.77, -7.2) * mm});
            skLineSegment(sketch, "E558", {"start": v(5.43, -7) * mm, "end": v(4.97, -6.2) * mm});
            skArc(sketch, "E559.filletArc", {"start": v(5.77, -4.8) * mm, "mid": v(5.57, -4.85) * mm, "end": v(5.43, -5) * mm});
            skArc(sketch, "E560.filletArc", {"start": v(7.04, -5) * mm, "mid": v(6.9, -4.85) * mm, "end": v(6.7, -4.8) * mm});
            skArc(sketch, "E561.filletArc", {"start": v(7.5, -6.2) * mm, "mid": v(7.56, -6) * mm, "end": v(7.5, -5.8) * mm});
            skArc(sketch, "E562.filletArc", {"start": v(6.7, -7.2) * mm, "mid": v(6.9, -7.15) * mm, "end": v(7.04, -7) * mm});
            skArc(sketch, "E563.filletArc", {"start": v(5.43, -7) * mm, "mid": v(5.57, -7.15) * mm, "end": v(5.77, -7.2) * mm});
            skArc(sketch, "E564.filletArc", {"start": v(4.97, -5.8) * mm, "mid": v(4.91, -6) * mm, "end": v(4.97, -6.2) * mm});
            skLineSegment(sketch, "E565", {"start": v(0.8, -8.2) * mm, "end": v(1.27, -7.4) * mm});
            skLineSegment(sketch, "E566", {"start": v(1.62, -7.2) * mm, "end": v(2.54, -7.2) * mm});
            skLineSegment(sketch, "E567", {"start": v(2.89, -7.4) * mm, "end": v(3.35, -8.2) * mm});
            skLineSegment(sketch, "E568", {"start": v(3.35, -8.6) * mm, "end": v(2.89, -9.4) * mm});
            skLineSegment(sketch, "E569", {"start": v(2.54, -9.6) * mm, "end": v(1.62, -9.6) * mm});
            skLineSegment(sketch, "E570", {"start": v(1.27, -9.4) * mm, "end": v(0.8, -8.6) * mm});
            skArc(sketch, "E571.filletArc", {"start": v(1.62, -7.2) * mm, "mid": v(1.42, -7.25) * mm, "end": v(1.27, -7.4) * mm});
            skArc(sketch, "E572.filletArc", {"start": v(2.89, -7.4) * mm, "mid": v(2.74, -7.25) * mm, "end": v(2.54, -7.2) * mm});
            skArc(sketch, "E573.filletArc", {"start": v(3.35, -8.6) * mm, "mid": v(3.4, -8.4) * mm, "end": v(3.35, -8.2) * mm});
            skArc(sketch, "E574.filletArc", {"start": v(2.54, -9.6) * mm, "mid": v(2.74, -9.55) * mm, "end": v(2.89, -9.4) * mm});
            skArc(sketch, "E575.filletArc", {"start": v(1.27, -9.4) * mm, "mid": v(1.42, -9.55) * mm, "end": v(1.62, -9.6) * mm});
            skArc(sketch, "E576.filletArc", {"start": v(0.8, -8.2) * mm, "mid": v(0.75, -8.4) * mm, "end": v(0.8, -8.6) * mm});
            skLineSegment(sketch, "E577", {"start": v(-1.27, -9.4) * mm, "end": v(-0.8, -8.6) * mm});
            skLineSegment(sketch, "E578", {"start": v(-0.46, -8.4) * mm, "end": v(0.46, -8.4) * mm});
            skLineSegment(sketch, "E579", {"start": v(0.8, -8.6) * mm, "end": v(1.27, -9.4) * mm});
            skLineSegment(sketch, "E580", {"start": v(1.27, -9.8) * mm, "end": v(0.8, -10.6) * mm});
            skLineSegment(sketch, "E581", {"start": v(0.46, -10.8) * mm, "end": v(-0.46, -10.8) * mm});
            skLineSegment(sketch, "E582", {"start": v(-0.8, -10.6) * mm, "end": v(-1.27, -9.8) * mm});
            skArc(sketch, "E583.filletArc", {"start": v(-0.46, -8.4) * mm, "mid": v(-0.66, -8.45) * mm, "end": v(-0.8, -8.6) * mm});
            skArc(sketch, "E584.filletArc", {"start": v(0.8, -8.6) * mm, "mid": v(0.66, -8.45) * mm, "end": v(0.46, -8.4) * mm});
            skArc(sketch, "E585.filletArc", {"start": v(1.27, -9.8) * mm, "mid": v(1.32, -9.6) * mm, "end": v(1.27, -9.4) * mm});
            skArc(sketch, "E586.filletArc", {"start": v(0.46, -10.8) * mm, "mid": v(0.66, -10.75) * mm, "end": v(0.8, -10.6) * mm});
            skArc(sketch, "E587.filletArc", {"start": v(-0.8, -10.6) * mm, "mid": v(-0.66, -10.75) * mm, "end": v(-0.46, -10.8) * mm});
            skArc(sketch, "E588.filletArc", {"start": v(-1.27, -9.4) * mm, "mid": v(-1.32, -9.6) * mm, "end": v(-1.27, -9.8) * mm});
            skLineSegment(sketch, "E589", {"start": v(-3.35, -8.2) * mm, "end": v(-2.89, -7.4) * mm});
            skLineSegment(sketch, "E590", {"start": v(-2.54, -7.2) * mm, "end": v(-1.62, -7.2) * mm});
            skLineSegment(sketch, "E591", {"start": v(-1.27, -7.4) * mm, "end": v(-0.8, -8.2) * mm});
            skLineSegment(sketch, "E592", {"start": v(-0.8, -8.6) * mm, "end": v(-1.27, -9.4) * mm});
            skLineSegment(sketch, "E593", {"start": v(-1.62, -9.6) * mm, "end": v(-2.54, -9.6) * mm});
            skLineSegment(sketch, "E594", {"start": v(-2.89, -9.4) * mm, "end": v(-3.35, -8.6) * mm});
            skArc(sketch, "E595.filletArc", {"start": v(-2.54, -7.2) * mm, "mid": v(-2.74, -7.25) * mm, "end": v(-2.89, -7.4) * mm});
            skArc(sketch, "E596.filletArc", {"start": v(-1.27, -7.4) * mm, "mid": v(-1.42, -7.25) * mm, "end": v(-1.62, -7.2) * mm});
            skArc(sketch, "E597.filletArc", {"start": v(-0.8, -8.6) * mm, "mid": v(-0.75, -8.4) * mm, "end": v(-0.8, -8.2) * mm});
            skArc(sketch, "E598.filletArc", {"start": v(-1.62, -9.6) * mm, "mid": v(-1.42, -9.55) * mm, "end": v(-1.27, -9.4) * mm});
            skArc(sketch, "E599.filletArc", {"start": v(-2.89, -9.4) * mm, "mid": v(-2.74, -9.55) * mm, "end": v(-2.54, -9.6) * mm});
            skArc(sketch, "E600.filletArc", {"start": v(-3.35, -8.2) * mm, "mid": v(-3.4, -8.4) * mm, "end": v(-3.35, -8.6) * mm});
            skLineSegment(sketch, "E601", {"start": v(-5.43, -7) * mm, "end": v(-4.97, -6.2) * mm});
            skLineSegment(sketch, "E602", {"start": v(-4.62, -6) * mm, "end": v(-3.7, -6) * mm});
            skLineSegment(sketch, "E603", {"start": v(-3.35, -6.2) * mm, "end": v(-2.89, -7) * mm});
            skLineSegment(sketch, "E604", {"start": v(-2.89, -7.4) * mm, "end": v(-3.35, -8.2) * mm});
            skLineSegment(sketch, "E605", {"start": v(-3.7, -8.4) * mm, "end": v(-4.62, -8.4) * mm});
            skLineSegment(sketch, "E606", {"start": v(-4.97, -8.2) * mm, "end": v(-5.43, -7.4) * mm});
            skArc(sketch, "E607.filletArc", {"start": v(-4.62, -6) * mm, "mid": v(-4.82, -6.05) * mm, "end": v(-4.97, -6.2) * mm});
            skArc(sketch, "E608.filletArc", {"start": v(-3.35, -6.2) * mm, "mid": v(-3.5, -6.05) * mm, "end": v(-3.7, -6) * mm});
            skArc(sketch, "E609.filletArc", {"start": v(-2.89, -7.4) * mm, "mid": v(-2.83, -7.2) * mm, "end": v(-2.89, -7) * mm});
            skArc(sketch, "E610.filletArc", {"start": v(-3.7, -8.4) * mm, "mid": v(-3.5, -8.35) * mm, "end": v(-3.35, -8.2) * mm});
            skArc(sketch, "E611.filletArc", {"start": v(-4.97, -8.2) * mm, "mid": v(-4.82, -8.35) * mm, "end": v(-4.62, -8.4) * mm});
            skArc(sketch, "E612.filletArc", {"start": v(-5.43, -7) * mm, "mid": v(-5.48, -7.2) * mm, "end": v(-5.43, -7.4) * mm});
            skLineSegment(sketch, "E613", {"start": v(-7.5, -5.8) * mm, "end": v(-7.04, -5) * mm});
            skLineSegment(sketch, "E614", {"start": v(-6.7, -4.8) * mm, "end": v(-5.77, -4.8) * mm});
            skLineSegment(sketch, "E615", {"start": v(-5.43, -5) * mm, "end": v(-4.97, -5.8) * mm});
            skLineSegment(sketch, "E616", {"start": v(-4.97, -6.2) * mm, "end": v(-5.43, -7) * mm});
            skLineSegment(sketch, "E617", {"start": v(-5.77, -7.2) * mm, "end": v(-6.7, -7.2) * mm});
            skLineSegment(sketch, "E618", {"start": v(-7.04, -7) * mm, "end": v(-7.5, -6.2) * mm});
            skArc(sketch, "E619.filletArc", {"start": v(-6.7, -4.8) * mm, "mid": v(-6.9, -4.85) * mm, "end": v(-7.04, -5) * mm});
            skArc(sketch, "E620.filletArc", {"start": v(-5.43, -5) * mm, "mid": v(-5.57, -4.85) * mm, "end": v(-5.77, -4.8) * mm});
            skArc(sketch, "E621.filletArc", {"start": v(-4.97, -6.2) * mm, "mid": v(-4.91, -6) * mm, "end": v(-4.97, -5.8) * mm});
            skArc(sketch, "E622.filletArc", {"start": v(-5.77, -7.2) * mm, "mid": v(-5.57, -7.15) * mm, "end": v(-5.43, -7) * mm});
            skArc(sketch, "E623.filletArc", {"start": v(-7.04, -7) * mm, "mid": v(-6.9, -7.15) * mm, "end": v(-6.7, -7.2) * mm});
            skArc(sketch, "E624.filletArc", {"start": v(-7.5, -5.8) * mm, "mid": v(-7.56, -6) * mm, "end": v(-7.5, -6.2) * mm});
            skLineSegment(sketch, "E625", {"start": v(-9.58, -2.2) * mm, "end": v(-9.12, -1.4) * mm});
            skLineSegment(sketch, "E626", {"start": v(-8.78, -1.2) * mm, "end": v(-7.85, -1.2) * mm});
            skLineSegment(sketch, "E627", {"start": v(-7.5, -1.4) * mm, "end": v(-7.04, -2.2) * mm});
            skLineSegment(sketch, "E628", {"start": v(-7.04, -2.6) * mm, "end": v(-7.5, -3.4) * mm});
            skLineSegment(sketch, "E629", {"start": v(-7.85, -3.6) * mm, "end": v(-8.78, -3.6) * mm});
            skLineSegment(sketch, "E630", {"start": v(-9.12, -3.4) * mm, "end": v(-9.58, -2.6) * mm});
            skArc(sketch, "E631.filletArc", {"start": v(-8.78, -1.2) * mm, "mid": v(-8.98, -1.25) * mm, "end": v(-9.12, -1.4) * mm});
            skArc(sketch, "E632.filletArc", {"start": v(-7.5, -1.4) * mm, "mid": v(-7.65, -1.25) * mm, "end": v(-7.85, -1.2) * mm});
            skArc(sketch, "E633.filletArc", {"start": v(-7.04, -2.6) * mm, "mid": v(-7, -2.4) * mm, "end": v(-7.04, -2.2) * mm});
            skArc(sketch, "E634.filletArc", {"start": v(-7.85, -3.6) * mm, "mid": v(-7.65, -3.55) * mm, "end": v(-7.5, -3.4) * mm});
            skArc(sketch, "E635.filletArc", {"start": v(-9.12, -3.4) * mm, "mid": v(-8.98, -3.55) * mm, "end": v(-8.78, -3.6) * mm});
            skArc(sketch, "E636.filletArc", {"start": v(-9.58, -2.2) * mm, "mid": v(-9.64, -2.4) * mm, "end": v(-9.58, -2.6) * mm});
            skLineSegment(sketch, "E637", {"start": v(-9.58, 0.2) * mm, "end": v(-9.12, 1) * mm});
            skLineSegment(sketch, "E638", {"start": v(-8.78, 1.2) * mm, "end": v(-7.85, 1.2) * mm});
            skLineSegment(sketch, "E639", {"start": v(-7.5, 1) * mm, "end": v(-7.04, 0.2) * mm});
            skLineSegment(sketch, "E640", {"start": v(-7.04, -0.2) * mm, "end": v(-7.5, -1) * mm});
            skLineSegment(sketch, "E641", {"start": v(-7.85, -1.2) * mm, "end": v(-8.78, -1.2) * mm});
            skLineSegment(sketch, "E642", {"start": v(-9.12, -1) * mm, "end": v(-9.58, -0.2) * mm});
            skArc(sketch, "E643.filletArc", {"start": v(-8.78, 1.2) * mm, "mid": v(-8.98, 1.15) * mm, "end": v(-9.12, 1) * mm});
            skArc(sketch, "E644.filletArc", {"start": v(-7.5, 1) * mm, "mid": v(-7.65, 1.15) * mm, "end": v(-7.85, 1.2) * mm});
            skArc(sketch, "E645.filletArc", {"start": v(-7.04, -0.2) * mm, "mid": v(-7, 0) * mm, "end": v(-7.04, 0.2) * mm});
            skArc(sketch, "E646.filletArc", {"start": v(-7.85, -1.2) * mm, "mid": v(-7.65, -1.15) * mm, "end": v(-7.5, -1) * mm});
            skArc(sketch, "E647.filletArc", {"start": v(-9.12, -1) * mm, "mid": v(-8.98, -1.15) * mm, "end": v(-8.78, -1.2) * mm});
            skArc(sketch, "E648.filletArc", {"start": v(-9.58, 0.2) * mm, "mid": v(-9.64, 0) * mm, "end": v(-9.58, -0.2) * mm});
            skLineSegment(sketch, "E649", {"start": v(-9.58, 2.6) * mm, "end": v(-9.12, 3.4) * mm});
            skLineSegment(sketch, "E650", {"start": v(-8.78, 3.6) * mm, "end": v(-7.85, 3.6) * mm});
            skLineSegment(sketch, "E651", {"start": v(-7.5, 3.4) * mm, "end": v(-7.04, 2.6) * mm});
            skLineSegment(sketch, "E652", {"start": v(-7.04, 2.2) * mm, "end": v(-7.5, 1.4) * mm});
            skLineSegment(sketch, "E653", {"start": v(-7.85, 1.2) * mm, "end": v(-8.78, 1.2) * mm});
            skLineSegment(sketch, "E654", {"start": v(-9.12, 1.4) * mm, "end": v(-9.58, 2.2) * mm});
            skArc(sketch, "E655.filletArc", {"start": v(-8.78, 3.6) * mm, "mid": v(-8.98, 3.55) * mm, "end": v(-9.12, 3.4) * mm});
            skArc(sketch, "E656.filletArc", {"start": v(-7.5, 3.4) * mm, "mid": v(-7.65, 3.55) * mm, "end": v(-7.85, 3.6) * mm});
            skArc(sketch, "E657.filletArc", {"start": v(-7.04, 2.2) * mm, "mid": v(-7, 2.4) * mm, "end": v(-7.04, 2.6) * mm});
            skArc(sketch, "E658.filletArc", {"start": v(-7.85, 1.2) * mm, "mid": v(-7.65, 1.25) * mm, "end": v(-7.5, 1.4) * mm});
            skArc(sketch, "E659.filletArc", {"start": v(-9.12, 1.4) * mm, "mid": v(-8.98, 1.25) * mm, "end": v(-8.78, 1.2) * mm});
            skArc(sketch, "E660.filletArc", {"start": v(-9.58, 2.6) * mm, "mid": v(-9.64, 2.4) * mm, "end": v(-9.58, 2.2) * mm});
            skLineSegment(sketch, "E661", {"start": v(-9.58, 5) * mm, "end": v(-9.12, 5.8) * mm});
            skLineSegment(sketch, "E662", {"start": v(-8.78, 6) * mm, "end": v(-7.85, 6) * mm});
            skLineSegment(sketch, "E663", {"start": v(-7.5, 5.8) * mm, "end": v(-7.04, 5) * mm});
            skLineSegment(sketch, "E664", {"start": v(-7.04, 4.6) * mm, "end": v(-7.5, 3.8) * mm});
            skLineSegment(sketch, "E665", {"start": v(-7.85, 3.6) * mm, "end": v(-8.78, 3.6) * mm});
            skLineSegment(sketch, "E666", {"start": v(-9.12, 3.8) * mm, "end": v(-9.58, 4.6) * mm});
            skArc(sketch, "E667.filletArc", {"start": v(-8.78, 6) * mm, "mid": v(-8.98, 5.95) * mm, "end": v(-9.12, 5.8) * mm});
            skArc(sketch, "E668.filletArc", {"start": v(-7.5, 5.8) * mm, "mid": v(-7.65, 5.95) * mm, "end": v(-7.85, 6) * mm});
            skArc(sketch, "E669.filletArc", {"start": v(-7.04, 4.6) * mm, "mid": v(-7, 4.8) * mm, "end": v(-7.04, 5) * mm});
            skArc(sketch, "E670.filletArc", {"start": v(-7.85, 3.6) * mm, "mid": v(-7.65, 3.65) * mm, "end": v(-7.5, 3.8) * mm});
            skArc(sketch, "E671.filletArc", {"start": v(-9.12, 3.8) * mm, "mid": v(-8.98, 3.65) * mm, "end": v(-8.78, 3.6) * mm});
            skArc(sketch, "E672.filletArc", {"start": v(-9.58, 5) * mm, "mid": v(-9.64, 4.8) * mm, "end": v(-9.58, 4.6) * mm});
            skLineSegment(sketch, "E673", {"start": v(-7.5, 6.2) * mm, "end": v(-7.04, 7) * mm});
            skLineSegment(sketch, "E674", {"start": v(-6.7, 7.2) * mm, "end": v(-5.77, 7.2) * mm});
            skLineSegment(sketch, "E675", {"start": v(-5.43, 7) * mm, "end": v(-4.97, 6.2) * mm});
            skLineSegment(sketch, "E676", {"start": v(-4.97, 5.8) * mm, "end": v(-5.43, 5) * mm});
            skLineSegment(sketch, "E677", {"start": v(-5.77, 4.8) * mm, "end": v(-6.7, 4.8) * mm});
            skLineSegment(sketch, "E678", {"start": v(-7.04, 5) * mm, "end": v(-7.5, 5.8) * mm});
            skArc(sketch, "E679.filletArc", {"start": v(-6.7, 7.2) * mm, "mid": v(-6.9, 7.15) * mm, "end": v(-7.04, 7) * mm});
            skArc(sketch, "E680.filletArc", {"start": v(-5.43, 7) * mm, "mid": v(-5.57, 7.15) * mm, "end": v(-5.77, 7.2) * mm});
            skArc(sketch, "E681.filletArc", {"start": v(-4.97, 5.8) * mm, "mid": v(-4.91, 6) * mm, "end": v(-4.97, 6.2) * mm});
            skArc(sketch, "E682.filletArc", {"start": v(-5.77, 4.8) * mm, "mid": v(-5.57, 4.85) * mm, "end": v(-5.43, 5) * mm});
            skArc(sketch, "E683.filletArc", {"start": v(-7.04, 5) * mm, "mid": v(-6.9, 4.85) * mm, "end": v(-6.7, 4.8) * mm});
            skArc(sketch, "E684.filletArc", {"start": v(-7.5, 6.2) * mm, "mid": v(-7.56, 6) * mm, "end": v(-7.5, 5.8) * mm});
            skLineSegment(sketch, "E685", {"start": v(-5.43, 7.4) * mm, "end": v(-4.97, 8.2) * mm});
            skLineSegment(sketch, "E686", {"start": v(-4.62, 8.4) * mm, "end": v(-3.7, 8.4) * mm});
            skLineSegment(sketch, "E687", {"start": v(-3.35, 8.2) * mm, "end": v(-2.89, 7.4) * mm});
            skLineSegment(sketch, "E688", {"start": v(-2.89, 7) * mm, "end": v(-3.35, 6.2) * mm});
            skLineSegment(sketch, "E689", {"start": v(-3.7, 6) * mm, "end": v(-4.62, 6) * mm});
            skLineSegment(sketch, "E690", {"start": v(-4.97, 6.2) * mm, "end": v(-5.43, 7) * mm});
            skArc(sketch, "E691.filletArc", {"start": v(-4.62, 8.4) * mm, "mid": v(-4.82, 8.35) * mm, "end": v(-4.97, 8.2) * mm});
            skArc(sketch, "E692.filletArc", {"start": v(-3.35, 8.2) * mm, "mid": v(-3.5, 8.35) * mm, "end": v(-3.7, 8.4) * mm});
            skArc(sketch, "E693.filletArc", {"start": v(-2.89, 7) * mm, "mid": v(-2.83, 7.2) * mm, "end": v(-2.89, 7.4) * mm});
            skArc(sketch, "E694.filletArc", {"start": v(-3.7, 6) * mm, "mid": v(-3.5, 6.05) * mm, "end": v(-3.35, 6.2) * mm});
            skArc(sketch, "E695.filletArc", {"start": v(-4.97, 6.2) * mm, "mid": v(-4.82, 6.05) * mm, "end": v(-4.62, 6) * mm});
            skArc(sketch, "E696.filletArc", {"start": v(-5.43, 7.4) * mm, "mid": v(-5.48, 7.2) * mm, "end": v(-5.43, 7) * mm});
            skLineSegment(sketch, "E697", {"start": v(-3.35, 8.6) * mm, "end": v(-2.89, 9.4) * mm});
            skLineSegment(sketch, "E698", {"start": v(-2.54, 9.6) * mm, "end": v(-1.62, 9.6) * mm});
            skLineSegment(sketch, "E699", {"start": v(-1.27, 9.4) * mm, "end": v(-0.8, 8.6) * mm});
            skLineSegment(sketch, "E700", {"start": v(-0.8, 8.2) * mm, "end": v(-1.27, 7.4) * mm});
            skLineSegment(sketch, "E701", {"start": v(-1.62, 7.2) * mm, "end": v(-2.54, 7.2) * mm});
            skLineSegment(sketch, "E702", {"start": v(-2.89, 7.4) * mm, "end": v(-3.35, 8.2) * mm});
            skArc(sketch, "E703.filletArc", {"start": v(-2.54, 9.6) * mm, "mid": v(-2.74, 9.55) * mm, "end": v(-2.89, 9.4) * mm});
            skArc(sketch, "E704.filletArc", {"start": v(-1.27, 9.4) * mm, "mid": v(-1.42, 9.55) * mm, "end": v(-1.62, 9.6) * mm});
            skArc(sketch, "E705.filletArc", {"start": v(-0.8, 8.2) * mm, "mid": v(-0.75, 8.4) * mm, "end": v(-0.8, 8.6) * mm});
            skArc(sketch, "E706.filletArc", {"start": v(-1.62, 7.2) * mm, "mid": v(-1.42, 7.25) * mm, "end": v(-1.27, 7.4) * mm});
            skArc(sketch, "E707.filletArc", {"start": v(-2.89, 7.4) * mm, "mid": v(-2.74, 7.25) * mm, "end": v(-2.54, 7.2) * mm});
            skArc(sketch, "E708.filletArc", {"start": v(-3.35, 8.6) * mm, "mid": v(-3.4, 8.4) * mm, "end": v(-3.35, 8.2) * mm});
            skLineSegment(sketch, "E709", {"start": v(-1.27, 9.8) * mm, "end": v(-0.8, 10.6) * mm});
            skLineSegment(sketch, "E710", {"start": v(-0.46, 10.8) * mm, "end": v(0.46, 10.8) * mm});
            skLineSegment(sketch, "E711", {"start": v(0.8, 10.6) * mm, "end": v(1.27, 9.8) * mm});
            skLineSegment(sketch, "E712", {"start": v(1.27, 9.4) * mm, "end": v(0.8, 8.6) * mm});
            skLineSegment(sketch, "E713", {"start": v(0.46, 8.4) * mm, "end": v(-0.46, 8.4) * mm});
            skLineSegment(sketch, "E714", {"start": v(-0.8, 8.6) * mm, "end": v(-1.27, 9.4) * mm});
            skArc(sketch, "E715.filletArc", {"start": v(-0.46, 10.8) * mm, "mid": v(-0.66, 10.75) * mm, "end": v(-0.8, 10.6) * mm});
            skArc(sketch, "E716.filletArc", {"start": v(0.8, 10.6) * mm, "mid": v(0.66, 10.75) * mm, "end": v(0.46, 10.8) * mm});
            skArc(sketch, "E717.filletArc", {"start": v(1.27, 9.4) * mm, "mid": v(1.32, 9.6) * mm, "end": v(1.27, 9.8) * mm});
            skArc(sketch, "E718.filletArc", {"start": v(0.46, 8.4) * mm, "mid": v(0.66, 8.45) * mm, "end": v(0.8, 8.6) * mm});
            skArc(sketch, "E719.filletArc", {"start": v(-0.8, 8.6) * mm, "mid": v(-0.66, 8.45) * mm, "end": v(-0.46, 8.4) * mm});
            skArc(sketch, "E720.filletArc", {"start": v(-1.27, 9.8) * mm, "mid": v(-1.32, 9.6) * mm, "end": v(-1.27, 9.4) * mm});
            skLineSegment(sketch, "E721", {"start": v(-9.58, -4.6) * mm, "end": v(-9.12, -3.8) * mm});
            skLineSegment(sketch, "E722", {"start": v(-8.78, -3.6) * mm, "end": v(-7.85, -3.6) * mm});
            skLineSegment(sketch, "E723", {"start": v(-7.5, -3.8) * mm, "end": v(-7.04, -4.6) * mm});
            skLineSegment(sketch, "E724", {"start": v(-7.04, -5) * mm, "end": v(-7.5, -5.8) * mm});
            skLineSegment(sketch, "E725", {"start": v(-7.85, -6) * mm, "end": v(-8.78, -6) * mm});
            skLineSegment(sketch, "E726", {"start": v(-9.12, -5.8) * mm, "end": v(-9.58, -5) * mm});
            skArc(sketch, "E727.filletArc", {"start": v(-8.78, -3.6) * mm, "mid": v(-8.98, -3.65) * mm, "end": v(-9.12, -3.8) * mm});
            skArc(sketch, "E728.filletArc", {"start": v(-7.5, -3.8) * mm, "mid": v(-7.65, -3.65) * mm, "end": v(-7.85, -3.6) * mm});
            skArc(sketch, "E729.filletArc", {"start": v(-7.04, -5) * mm, "mid": v(-7, -4.8) * mm, "end": v(-7.04, -4.6) * mm});
            skArc(sketch, "E730.filletArc", {"start": v(-7.85, -6) * mm, "mid": v(-7.65, -5.95) * mm, "end": v(-7.5, -5.8) * mm});
            skArc(sketch, "E731.filletArc", {"start": v(-9.12, -5.8) * mm, "mid": v(-8.98, -5.95) * mm, "end": v(-8.78, -6) * mm});
            skArc(sketch, "E732.filletArc", {"start": v(-9.58, -4.6) * mm, "mid": v(-9.64, -4.8) * mm, "end": v(-9.58, -5) * mm});
            skSolve(sketch);
        }
        {
            var Q0;
            Q0=qCreatedBy(id+"F0.planeOp",FACE);
            cPlane(context, id + "F2", {"entities" : qUnion([Q0]), "cplaneType" : CPlaneType.OFFSET, "offset" : 0.4 * mm, "width" : 150 * mm, "height" : 150 * mm});
        }
        {
            var Q0;
            Q0=qCreatedBy(id+"F2.planeOp",FACE);
            var sketch = newSketch(context, id + "F3", { "sketchPlane" : qUnion([Q0])});
            skPoint(sketch, "E733.middle", {"position": v(0, 0) * mm});
            skLineSegment(sketch, "E734", {"start": v(-1.27, 1.4) * mm, "end": v(-0.8, 2.2) * mm});
            skLineSegment(sketch, "E735", {"start": v(-0.46, 2.4) * mm, "end": v(0.46, 2.4) * mm});
            skLineSegment(sketch, "E736", {"start": v(0.8, 2.2) * mm, "end": v(1.27, 1.4) * mm});
            skLineSegment(sketch, "E737", {"start": v(0.8, 0.2) * mm, "end": v(1.27, 1) * mm});
            skLineSegment(sketch, "E738", {"start": v(-0.8, 0.2) * mm, "end": v(-1.27, 1) * mm});
            skLineSegment(sketch, "E739", {"start": v(-0.46, 0) * mm, "end": v(0.46, 0) * mm});
            skArc(sketch, "E740.filletArc", {"start": v(-0.46, 2.4) * mm, "mid": v(-0.66, 2.35) * mm, "end": v(-0.8, 2.2) * mm});
            skArc(sketch, "E741.filletArc", {"start": v(0.8, 2.2) * mm, "mid": v(0.66, 2.35) * mm, "end": v(0.46, 2.4) * mm});
            skArc(sketch, "E742.filletArc", {"start": v(1.27, 1) * mm, "mid": v(1.32, 1.2) * mm, "end": v(1.27, 1.4) * mm});
            skArc(sketch, "E743.filletArc", {"start": v(-1.27, 1.4) * mm, "mid": v(-1.32, 1.2) * mm, "end": v(-1.27, 1) * mm});
            skArc(sketch, "E744.filletArc", {"start": v(-0.8, 0.2) * mm, "mid": v(-0.66, 0.05) * mm, "end": v(-0.46, 0) * mm});
            skArc(sketch, "E745.filletArc", {"start": v(0.46, 0) * mm, "mid": v(0.66, 0.05) * mm, "end": v(0.8, 0.2) * mm});
            skLineSegment(sketch, "E746", {"start": v(-3.35, 2.6) * mm, "end": v(-2.89, 3.4) * mm});
            skLineSegment(sketch, "E747", {"start": v(-2.54, 3.6) * mm, "end": v(-1.62, 3.6) * mm});
            skLineSegment(sketch, "E748", {"start": v(-1.27, 3.4) * mm, "end": v(-0.8, 2.6) * mm});
            skLineSegment(sketch, "E749", {"start": v(-2.89, 1.4) * mm, "end": v(-3.35, 2.2) * mm});
            skLineSegment(sketch, "E750", {"start": v(-2.54, 1.2) * mm, "end": v(-1.62, 1.2) * mm});
            skArc(sketch, "E751.filletArc", {"start": v(-2.54, 3.6) * mm, "mid": v(-2.74, 3.55) * mm, "end": v(-2.89, 3.4) * mm});
            skArc(sketch, "E752.filletArc", {"start": v(-1.27, 3.4) * mm, "mid": v(-1.42, 3.55) * mm, "end": v(-1.62, 3.6) * mm});
            skArc(sketch, "E753.filletArc", {"start": v(-0.8, 2.2) * mm, "mid": v(-0.75, 2.4) * mm, "end": v(-0.8, 2.6) * mm});
            skArc(sketch, "E754.filletArc", {"start": v(-3.35, 2.6) * mm, "mid": v(-3.4, 2.4) * mm, "end": v(-3.35, 2.2) * mm});
            skArc(sketch, "E755.filletArc", {"start": v(-2.89, 1.4) * mm, "mid": v(-2.74, 1.25) * mm, "end": v(-2.54, 1.2) * mm});
            skArc(sketch, "E756.filletArc", {"start": v(-1.62, 1.2) * mm, "mid": v(-1.42, 1.25) * mm, "end": v(-1.27, 1.4) * mm});
            skLineSegment(sketch, "E757", {"start": v(-1.27, 3.8) * mm, "end": v(-0.8, 4.6) * mm});
            skLineSegment(sketch, "E758", {"start": v(-0.46, 4.8) * mm, "end": v(0.46, 4.8) * mm});
            skLineSegment(sketch, "E759", {"start": v(0.8, 4.6) * mm, "end": v(1.27, 3.8) * mm});
            skLineSegment(sketch, "E760", {"start": v(0.8, 2.6) * mm, "end": v(1.27, 3.4) * mm});
            skLineSegment(sketch, "E761", {"start": v(-0.8, 2.6) * mm, "end": v(-1.27, 3.4) * mm});
            skArc(sketch, "E762.filletArc", {"start": v(-0.46, 4.8) * mm, "mid": v(-0.66, 4.75) * mm, "end": v(-0.8, 4.6) * mm});
            skArc(sketch, "E763.filletArc", {"start": v(0.8, 4.6) * mm, "mid": v(0.66, 4.75) * mm, "end": v(0.46, 4.8) * mm});
            skArc(sketch, "E764.filletArc", {"start": v(1.27, 3.4) * mm, "mid": v(1.32, 3.6) * mm, "end": v(1.27, 3.8) * mm});
            skArc(sketch, "E765.filletArc", {"start": v(-1.27, 3.8) * mm, "mid": v(-1.32, 3.6) * mm, "end": v(-1.27, 3.4) * mm});
            skArc(sketch, "E766.filletArc", {"start": v(-0.8, 2.6) * mm, "mid": v(-0.66, 2.45) * mm, "end": v(-0.46, 2.4) * mm});
            skArc(sketch, "E767.filletArc", {"start": v(0.46, 2.4) * mm, "mid": v(0.66, 2.45) * mm, "end": v(0.8, 2.6) * mm});
            skLineSegment(sketch, "E768", {"start": v(1.62, 3.6) * mm, "end": v(2.54, 3.6) * mm});
            skLineSegment(sketch, "E769", {"start": v(2.89, 3.4) * mm, "end": v(3.35, 2.6) * mm});
            skLineSegment(sketch, "E770", {"start": v(2.89, 1.4) * mm, "end": v(3.35, 2.2) * mm});
            skLineSegment(sketch, "E771", {"start": v(1.27, 1.4) * mm, "end": v(0.8, 2.2) * mm});
            skLineSegment(sketch, "E772", {"start": v(1.62, 1.2) * mm, "end": v(2.54, 1.2) * mm});
            skArc(sketch, "E773.filletArc", {"start": v(1.62, 3.6) * mm, "mid": v(1.42, 3.55) * mm, "end": v(1.27, 3.4) * mm});
            skArc(sketch, "E774.filletArc", {"start": v(2.89, 3.4) * mm, "mid": v(2.74, 3.55) * mm, "end": v(2.54, 3.6) * mm});
            skArc(sketch, "E775.filletArc", {"start": v(3.35, 2.2) * mm, "mid": v(3.4, 2.4) * mm, "end": v(3.35, 2.6) * mm});
            skArc(sketch, "E776.filletArc", {"start": v(0.8, 2.6) * mm, "mid": v(0.75, 2.4) * mm, "end": v(0.8, 2.2) * mm});
            skArc(sketch, "E777.filletArc", {"start": v(1.27, 1.4) * mm, "mid": v(1.42, 1.25) * mm, "end": v(1.62, 1.2) * mm});
            skArc(sketch, "E778.filletArc", {"start": v(2.54, 1.2) * mm, "mid": v(2.74, 1.25) * mm, "end": v(2.89, 1.4) * mm});
            skLineSegment(sketch, "E779", {"start": v(2.89, 1) * mm, "end": v(3.35, 0.2) * mm});
            skLineSegment(sketch, "E780", {"start": v(2.89, -1) * mm, "end": v(3.35, -0.2) * mm});
            skLineSegment(sketch, "E781", {"start": v(1.27, -1) * mm, "end": v(0.8, -0.2) * mm});
            skLineSegment(sketch, "E782", {"start": v(1.62, -1.2) * mm, "end": v(2.54, -1.2) * mm});
            skArc(sketch, "E783.filletArc", {"start": v(1.62, 1.2) * mm, "mid": v(1.42, 1.15) * mm, "end": v(1.27, 1) * mm});
            skArc(sketch, "E784.filletArc", {"start": v(2.89, 1) * mm, "mid": v(2.74, 1.15) * mm, "end": v(2.54, 1.2) * mm});
            skArc(sketch, "E785.filletArc", {"start": v(3.35, -0.2) * mm, "mid": v(3.4, 0) * mm, "end": v(3.35, 0.2) * mm});
            skArc(sketch, "E786.filletArc", {"start": v(0.8, 0.2) * mm, "mid": v(0.75, 0) * mm, "end": v(0.8, -0.2) * mm});
            skArc(sketch, "E787.filletArc", {"start": v(1.27, -1) * mm, "mid": v(1.42, -1.15) * mm, "end": v(1.62, -1.2) * mm});
            skArc(sketch, "E788.filletArc", {"start": v(2.54, -1.2) * mm, "mid": v(2.74, -1.15) * mm, "end": v(2.89, -1) * mm});
            skLineSegment(sketch, "E789", {"start": v(-1.27, -1) * mm, "end": v(-0.8, -0.2) * mm});
            skLineSegment(sketch, "E790", {"start": v(0.8, -0.2) * mm, "end": v(1.27, -1) * mm});
            skLineSegment(sketch, "E791", {"start": v(0.8, -2.2) * mm, "end": v(1.27, -1.4) * mm});
            skLineSegment(sketch, "E792", {"start": v(-0.8, -2.2) * mm, "end": v(-1.27, -1.4) * mm});
            skLineSegment(sketch, "E793", {"start": v(-0.46, -2.4) * mm, "end": v(0.46, -2.4) * mm});
            skArc(sketch, "E794.filletArc", {"start": v(-0.46, 0) * mm, "mid": v(-0.66, -0.05) * mm, "end": v(-0.8, -0.2) * mm});
            skArc(sketch, "E795.filletArc", {"start": v(0.8, -0.2) * mm, "mid": v(0.66, -0.05) * mm, "end": v(0.46, 0) * mm});
            skArc(sketch, "E796.filletArc", {"start": v(1.27, -1.4) * mm, "mid": v(1.32, -1.2) * mm, "end": v(1.27, -1) * mm});
            skArc(sketch, "E797.filletArc", {"start": v(-1.27, -1) * mm, "mid": v(-1.32, -1.2) * mm, "end": v(-1.27, -1.4) * mm});
            skArc(sketch, "E798.filletArc", {"start": v(-0.8, -2.2) * mm, "mid": v(-0.66, -2.35) * mm, "end": v(-0.46, -2.4) * mm});
            skArc(sketch, "E799.filletArc", {"start": v(0.46, -2.4) * mm, "mid": v(0.66, -2.35) * mm, "end": v(0.8, -2.2) * mm});
            skLineSegment(sketch, "E800", {"start": v(-3.35, 0.2) * mm, "end": v(-2.89, 1) * mm});
            skLineSegment(sketch, "E801", {"start": v(-1.27, 1) * mm, "end": v(-0.8, 0.2) * mm});
            skLineSegment(sketch, "E802", {"start": v(-2.89, -1) * mm, "end": v(-3.35, -0.2) * mm});
            skLineSegment(sketch, "E803", {"start": v(-2.54, -1.2) * mm, "end": v(-1.62, -1.2) * mm});
            skArc(sketch, "E804.filletArc", {"start": v(-2.54, 1.2) * mm, "mid": v(-2.74, 1.15) * mm, "end": v(-2.89, 1) * mm});
            skArc(sketch, "E805.filletArc", {"start": v(-1.27, 1) * mm, "mid": v(-1.42, 1.15) * mm, "end": v(-1.62, 1.2) * mm});
            skArc(sketch, "E806.filletArc", {"start": v(-0.8, -0.2) * mm, "mid": v(-0.75, 0) * mm, "end": v(-0.8, 0.2) * mm});
            skArc(sketch, "E807.filletArc", {"start": v(-3.35, 0.2) * mm, "mid": v(-3.4, 0) * mm, "end": v(-3.35, -0.2) * mm});
            skArc(sketch, "E808.filletArc", {"start": v(-2.89, -1) * mm, "mid": v(-2.74, -1.15) * mm, "end": v(-2.54, -1.2) * mm});
            skArc(sketch, "E809.filletArc", {"start": v(-1.62, -1.2) * mm, "mid": v(-1.42, -1.15) * mm, "end": v(-1.27, -1) * mm});
            skLineSegment(sketch, "E810", {"start": v(-3.35, 5) * mm, "end": v(-2.89, 5.8) * mm});
            skLineSegment(sketch, "E811", {"start": v(-2.54, 6) * mm, "end": v(-1.62, 6) * mm});
            skLineSegment(sketch, "E812", {"start": v(-1.27, 5.8) * mm, "end": v(-0.8, 5) * mm});
            skLineSegment(sketch, "E813", {"start": v(-2.89, 3.8) * mm, "end": v(-3.35, 4.6) * mm});
            skArc(sketch, "E814.filletArc", {"start": v(-2.54, 6) * mm, "mid": v(-2.74, 5.95) * mm, "end": v(-2.89, 5.8) * mm});
            skArc(sketch, "E815.filletArc", {"start": v(-1.27, 5.8) * mm, "mid": v(-1.42, 5.95) * mm, "end": v(-1.62, 6) * mm});
            skArc(sketch, "E816.filletArc", {"start": v(-0.8, 4.6) * mm, "mid": v(-0.75, 4.8) * mm, "end": v(-0.8, 5) * mm});
            skArc(sketch, "E817.filletArc", {"start": v(-3.35, 5) * mm, "mid": v(-3.4, 4.8) * mm, "end": v(-3.35, 4.6) * mm});
            skArc(sketch, "E818.filletArc", {"start": v(-2.89, 3.8) * mm, "mid": v(-2.74, 3.65) * mm, "end": v(-2.54, 3.6) * mm});
            skArc(sketch, "E819.filletArc", {"start": v(-1.62, 3.6) * mm, "mid": v(-1.42, 3.65) * mm, "end": v(-1.27, 3.8) * mm});
            skLineSegment(sketch, "E820", {"start": v(-1.27, 6.2) * mm, "end": v(-0.8, 7) * mm});
            skLineSegment(sketch, "E821", {"start": v(-0.46, 7.2) * mm, "end": v(0.46, 7.2) * mm});
            skLineSegment(sketch, "E822", {"start": v(0.8, 7) * mm, "end": v(1.27, 6.2) * mm});
            skLineSegment(sketch, "E823", {"start": v(0.8, 5) * mm, "end": v(1.27, 5.8) * mm});
            skLineSegment(sketch, "E824", {"start": v(-0.8, 5) * mm, "end": v(-1.27, 5.8) * mm});
            skArc(sketch, "E825.filletArc", {"start": v(-0.46, 7.2) * mm, "mid": v(-0.66, 7.15) * mm, "end": v(-0.8, 7) * mm});
            skArc(sketch, "E826.filletArc", {"start": v(0.8, 7) * mm, "mid": v(0.66, 7.15) * mm, "end": v(0.46, 7.2) * mm});
            skArc(sketch, "E827.filletArc", {"start": v(1.27, 5.8) * mm, "mid": v(1.32, 6) * mm, "end": v(1.27, 6.2) * mm});
            skArc(sketch, "E828.filletArc", {"start": v(-1.27, 6.2) * mm, "mid": v(-1.32, 6) * mm, "end": v(-1.27, 5.8) * mm});
            skArc(sketch, "E829.filletArc", {"start": v(-0.8, 5) * mm, "mid": v(-0.66, 4.85) * mm, "end": v(-0.46, 4.8) * mm});
            skArc(sketch, "E830.filletArc", {"start": v(0.46, 4.8) * mm, "mid": v(0.66, 4.85) * mm, "end": v(0.8, 5) * mm});
            skLineSegment(sketch, "E831", {"start": v(1.62, 6) * mm, "end": v(2.54, 6) * mm});
            skLineSegment(sketch, "E832", {"start": v(2.89, 5.8) * mm, "end": v(3.35, 5) * mm});
            skLineSegment(sketch, "E833", {"start": v(2.89, 3.8) * mm, "end": v(3.35, 4.6) * mm});
            skLineSegment(sketch, "E834", {"start": v(1.27, 3.8) * mm, "end": v(0.8, 4.6) * mm});
            skArc(sketch, "E835.filletArc", {"start": v(1.62, 6) * mm, "mid": v(1.42, 5.95) * mm, "end": v(1.27, 5.8) * mm});
            skArc(sketch, "E836.filletArc", {"start": v(2.89, 5.8) * mm, "mid": v(2.74, 5.95) * mm, "end": v(2.54, 6) * mm});
            skArc(sketch, "E837.filletArc", {"start": v(3.35, 4.6) * mm, "mid": v(3.4, 4.8) * mm, "end": v(3.35, 5) * mm});
            skArc(sketch, "E838.filletArc", {"start": v(0.8, 5) * mm, "mid": v(0.75, 4.8) * mm, "end": v(0.8, 4.6) * mm});
            skArc(sketch, "E839.filletArc", {"start": v(1.27, 3.8) * mm, "mid": v(1.42, 3.65) * mm, "end": v(1.62, 3.6) * mm});
            skArc(sketch, "E840.filletArc", {"start": v(2.54, 3.6) * mm, "mid": v(2.74, 3.65) * mm, "end": v(2.89, 3.8) * mm});
            skLineSegment(sketch, "E841", {"start": v(3.7, 4.8) * mm, "end": v(4.62, 4.8) * mm});
            skLineSegment(sketch, "E842", {"start": v(4.97, 4.6) * mm, "end": v(5.43, 3.8) * mm});
            skLineSegment(sketch, "E843", {"start": v(4.97, 2.6) * mm, "end": v(5.43, 3.4) * mm});
            skLineSegment(sketch, "E844", {"start": v(3.35, 2.6) * mm, "end": v(2.89, 3.4) * mm});
            skLineSegment(sketch, "E845", {"start": v(3.7, 2.4) * mm, "end": v(4.62, 2.4) * mm});
            skArc(sketch, "E846.filletArc", {"start": v(3.7, 4.8) * mm, "mid": v(3.5, 4.75) * mm, "end": v(3.35, 4.6) * mm});
            skArc(sketch, "E847.filletArc", {"start": v(4.97, 4.6) * mm, "mid": v(4.82, 4.75) * mm, "end": v(4.62, 4.8) * mm});
            skArc(sketch, "E848.filletArc", {"start": v(5.43, 3.4) * mm, "mid": v(5.48, 3.6) * mm, "end": v(5.43, 3.8) * mm});
            skArc(sketch, "E849.filletArc", {"start": v(2.89, 3.8) * mm, "mid": v(2.83, 3.6) * mm, "end": v(2.89, 3.4) * mm});
            skArc(sketch, "E850.filletArc", {"start": v(3.35, 2.6) * mm, "mid": v(3.5, 2.45) * mm, "end": v(3.7, 2.4) * mm});
            skArc(sketch, "E851.filletArc", {"start": v(4.62, 2.4) * mm, "mid": v(4.82, 2.45) * mm, "end": v(4.97, 2.6) * mm});
            skLineSegment(sketch, "E852", {"start": v(4.97, 2.2) * mm, "end": v(5.43, 1.4) * mm});
            skLineSegment(sketch, "E853", {"start": v(4.97, 0.2) * mm, "end": v(5.43, 1) * mm});
            skLineSegment(sketch, "E854", {"start": v(3.35, 0.2) * mm, "end": v(2.89, 1) * mm});
            skLineSegment(sketch, "E855", {"start": v(3.7, 0) * mm, "end": v(4.62, 0) * mm});
            skArc(sketch, "E856.filletArc", {"start": v(3.7, 2.4) * mm, "mid": v(3.5, 2.35) * mm, "end": v(3.35, 2.2) * mm});
            skArc(sketch, "E857.filletArc", {"start": v(4.97, 2.2) * mm, "mid": v(4.82, 2.35) * mm, "end": v(4.62, 2.4) * mm});
            skArc(sketch, "E858.filletArc", {"start": v(5.43, 1) * mm, "mid": v(5.48, 1.2) * mm, "end": v(5.43, 1.4) * mm});
            skArc(sketch, "E859.filletArc", {"start": v(2.89, 1.4) * mm, "mid": v(2.83, 1.2) * mm, "end": v(2.89, 1) * mm});
            skArc(sketch, "E860.filletArc", {"start": v(3.35, 0.2) * mm, "mid": v(3.5, 0.05) * mm, "end": v(3.7, 0) * mm});
            skArc(sketch, "E861.filletArc", {"start": v(4.62, 0) * mm, "mid": v(4.82, 0.05) * mm, "end": v(4.97, 0.2) * mm});
            skLineSegment(sketch, "E862", {"start": v(4.97, -0.2) * mm, "end": v(5.43, -1) * mm});
            skLineSegment(sketch, "E863", {"start": v(4.97, -2.2) * mm, "end": v(5.43, -1.4) * mm});
            skLineSegment(sketch, "E864", {"start": v(3.35, -2.2) * mm, "end": v(2.89, -1.4) * mm});
            skLineSegment(sketch, "E865", {"start": v(3.7, -2.4) * mm, "end": v(4.62, -2.4) * mm});
            skArc(sketch, "E866.filletArc", {"start": v(3.7, 0) * mm, "mid": v(3.5, -0.05) * mm, "end": v(3.35, -0.2) * mm});
            skArc(sketch, "E867.filletArc", {"start": v(4.97, -0.2) * mm, "mid": v(4.82, -0.05) * mm, "end": v(4.62, 0) * mm});
            skArc(sketch, "E868.filletArc", {"start": v(5.43, -1.4) * mm, "mid": v(5.48, -1.2) * mm, "end": v(5.43, -1) * mm});
            skArc(sketch, "E869.filletArc", {"start": v(2.89, -1) * mm, "mid": v(2.83, -1.2) * mm, "end": v(2.89, -1.4) * mm});
            skArc(sketch, "E870.filletArc", {"start": v(3.35, -2.2) * mm, "mid": v(3.5, -2.35) * mm, "end": v(3.7, -2.4) * mm});
            skArc(sketch, "E871.filletArc", {"start": v(4.62, -2.4) * mm, "mid": v(4.82, -2.35) * mm, "end": v(4.97, -2.2) * mm});
            skLineSegment(sketch, "E872", {"start": v(2.89, -1.4) * mm, "end": v(3.35, -2.2) * mm});
            skLineSegment(sketch, "E873", {"start": v(2.89, -3.4) * mm, "end": v(3.35, -2.6) * mm});
            skLineSegment(sketch, "E874", {"start": v(1.27, -3.4) * mm, "end": v(0.8, -2.6) * mm});
            skLineSegment(sketch, "E875", {"start": v(1.62, -3.6) * mm, "end": v(2.54, -3.6) * mm});
            skArc(sketch, "E876.filletArc", {"start": v(1.62, -1.2) * mm, "mid": v(1.42, -1.25) * mm, "end": v(1.27, -1.4) * mm});
            skArc(sketch, "E877.filletArc", {"start": v(2.89, -1.4) * mm, "mid": v(2.74, -1.25) * mm, "end": v(2.54, -1.2) * mm});
            skArc(sketch, "E878.filletArc", {"start": v(3.35, -2.6) * mm, "mid": v(3.4, -2.4) * mm, "end": v(3.35, -2.2) * mm});
            skArc(sketch, "E879.filletArc", {"start": v(0.8, -2.2) * mm, "mid": v(0.75, -2.4) * mm, "end": v(0.8, -2.6) * mm});
            skArc(sketch, "E880.filletArc", {"start": v(1.27, -3.4) * mm, "mid": v(1.42, -3.55) * mm, "end": v(1.62, -3.6) * mm});
            skArc(sketch, "E881.filletArc", {"start": v(2.54, -3.6) * mm, "mid": v(2.74, -3.55) * mm, "end": v(2.89, -3.4) * mm});
            skLineSegment(sketch, "E882", {"start": v(-1.27, -3.4) * mm, "end": v(-0.8, -2.6) * mm});
            skLineSegment(sketch, "E883", {"start": v(0.8, -2.6) * mm, "end": v(1.27, -3.4) * mm});
            skLineSegment(sketch, "E884", {"start": v(0.8, -4.6) * mm, "end": v(1.27, -3.8) * mm});
            skLineSegment(sketch, "E885", {"start": v(-0.8, -4.6) * mm, "end": v(-1.27, -3.8) * mm});
            skLineSegment(sketch, "E886", {"start": v(-0.46, -4.8) * mm, "end": v(0.46, -4.8) * mm});
            skArc(sketch, "E887.filletArc", {"start": v(-0.46, -2.4) * mm, "mid": v(-0.66, -2.45) * mm, "end": v(-0.8, -2.6) * mm});
            skArc(sketch, "E888.filletArc", {"start": v(0.8, -2.6) * mm, "mid": v(0.66, -2.45) * mm, "end": v(0.46, -2.4) * mm});
            skArc(sketch, "E889.filletArc", {"start": v(1.27, -3.8) * mm, "mid": v(1.32, -3.6) * mm, "end": v(1.27, -3.4) * mm});
            skArc(sketch, "E890.filletArc", {"start": v(-1.27, -3.4) * mm, "mid": v(-1.32, -3.6) * mm, "end": v(-1.27, -3.8) * mm});
            skArc(sketch, "E891.filletArc", {"start": v(-0.8, -4.6) * mm, "mid": v(-0.66, -4.75) * mm, "end": v(-0.46, -4.8) * mm});
            skArc(sketch, "E892.filletArc", {"start": v(0.46, -4.8) * mm, "mid": v(0.66, -4.75) * mm, "end": v(0.8, -4.6) * mm});
            skLineSegment(sketch, "E893", {"start": v(-3.35, -2.2) * mm, "end": v(-2.89, -1.4) * mm});
            skLineSegment(sketch, "E894", {"start": v(-1.27, -1.4) * mm, "end": v(-0.8, -2.2) * mm});
            skLineSegment(sketch, "E895", {"start": v(-2.89, -3.4) * mm, "end": v(-3.35, -2.6) * mm});
            skLineSegment(sketch, "E896", {"start": v(-2.54, -3.6) * mm, "end": v(-1.62, -3.6) * mm});
            skArc(sketch, "E897.filletArc", {"start": v(-2.54, -1.2) * mm, "mid": v(-2.74, -1.25) * mm, "end": v(-2.89, -1.4) * mm});
            skArc(sketch, "E898.filletArc", {"start": v(-1.27, -1.4) * mm, "mid": v(-1.42, -1.25) * mm, "end": v(-1.62, -1.2) * mm});
            skArc(sketch, "E899.filletArc", {"start": v(-0.8, -2.6) * mm, "mid": v(-0.75, -2.4) * mm, "end": v(-0.8, -2.2) * mm});
            skArc(sketch, "E900.filletArc", {"start": v(-3.35, -2.2) * mm, "mid": v(-3.4, -2.4) * mm, "end": v(-3.35, -2.6) * mm});
            skArc(sketch, "E901.filletArc", {"start": v(-2.89, -3.4) * mm, "mid": v(-2.74, -3.55) * mm, "end": v(-2.54, -3.6) * mm});
            skArc(sketch, "E902.filletArc", {"start": v(-1.62, -3.6) * mm, "mid": v(-1.42, -3.55) * mm, "end": v(-1.27, -3.4) * mm});
            skLineSegment(sketch, "E903", {"start": v(-5.43, -1) * mm, "end": v(-4.97, -0.2) * mm});
            skLineSegment(sketch, "E904", {"start": v(-4.62, 0) * mm, "end": v(-3.7, 0) * mm});
            skLineSegment(sketch, "E905", {"start": v(-3.35, -0.2) * mm, "end": v(-2.89, -1) * mm});
            skLineSegment(sketch, "E906", {"start": v(-4.97, -2.2) * mm, "end": v(-5.43, -1.4) * mm});
            skLineSegment(sketch, "E907", {"start": v(-4.62, -2.4) * mm, "end": v(-3.7, -2.4) * mm});
            skArc(sketch, "E908.filletArc", {"start": v(-4.62, 0) * mm, "mid": v(-4.82, -0.05) * mm, "end": v(-4.97, -0.2) * mm});
            skArc(sketch, "E909.filletArc", {"start": v(-3.35, -0.2) * mm, "mid": v(-3.5, -0.05) * mm, "end": v(-3.7, 0) * mm});
            skArc(sketch, "E910.filletArc", {"start": v(-2.89, -1.4) * mm, "mid": v(-2.83, -1.2) * mm, "end": v(-2.89, -1) * mm});
            skArc(sketch, "E911.filletArc", {"start": v(-5.43, -1) * mm, "mid": v(-5.48, -1.2) * mm, "end": v(-5.43, -1.4) * mm});
            skArc(sketch, "E912.filletArc", {"start": v(-4.97, -2.2) * mm, "mid": v(-4.82, -2.35) * mm, "end": v(-4.62, -2.4) * mm});
            skArc(sketch, "E913.filletArc", {"start": v(-3.7, -2.4) * mm, "mid": v(-3.5, -2.35) * mm, "end": v(-3.35, -2.2) * mm});
            skLineSegment(sketch, "E914", {"start": v(-5.43, 1.4) * mm, "end": v(-4.97, 2.2) * mm});
            skLineSegment(sketch, "E915", {"start": v(-4.62, 2.4) * mm, "end": v(-3.7, 2.4) * mm});
            skLineSegment(sketch, "E916", {"start": v(-3.35, 2.2) * mm, "end": v(-2.89, 1.4) * mm});
            skLineSegment(sketch, "E917", {"start": v(-4.97, 0.2) * mm, "end": v(-5.43, 1) * mm});
            skArc(sketch, "E918.filletArc", {"start": v(-4.62, 2.4) * mm, "mid": v(-4.82, 2.35) * mm, "end": v(-4.97, 2.2) * mm});
            skArc(sketch, "E919.filletArc", {"start": v(-3.35, 2.2) * mm, "mid": v(-3.5, 2.35) * mm, "end": v(-3.7, 2.4) * mm});
            skArc(sketch, "E920.filletArc", {"start": v(-2.89, 1) * mm, "mid": v(-2.83, 1.2) * mm, "end": v(-2.89, 1.4) * mm});
            skArc(sketch, "E921.filletArc", {"start": v(-5.43, 1.4) * mm, "mid": v(-5.48, 1.2) * mm, "end": v(-5.43, 1) * mm});
            skArc(sketch, "E922.filletArc", {"start": v(-4.97, 0.2) * mm, "mid": v(-4.82, 0.05) * mm, "end": v(-4.62, 0) * mm});
            skArc(sketch, "E923.filletArc", {"start": v(-3.7, 0) * mm, "mid": v(-3.5, 0.05) * mm, "end": v(-3.35, 0.2) * mm});
            skLineSegment(sketch, "E924", {"start": v(-5.43, 3.8) * mm, "end": v(-4.97, 4.6) * mm});
            skLineSegment(sketch, "E925", {"start": v(-4.62, 4.8) * mm, "end": v(-3.7, 4.8) * mm});
            skLineSegment(sketch, "E926", {"start": v(-3.35, 4.6) * mm, "end": v(-2.89, 3.8) * mm});
            skLineSegment(sketch, "E927", {"start": v(-4.97, 2.6) * mm, "end": v(-5.43, 3.4) * mm});
            skArc(sketch, "E928.filletArc", {"start": v(-4.62, 4.8) * mm, "mid": v(-4.82, 4.75) * mm, "end": v(-4.97, 4.6) * mm});
            skArc(sketch, "E929.filletArc", {"start": v(-3.35, 4.6) * mm, "mid": v(-3.5, 4.75) * mm, "end": v(-3.7, 4.8) * mm});
            skArc(sketch, "E930.filletArc", {"start": v(-2.89, 3.4) * mm, "mid": v(-2.83, 3.6) * mm, "end": v(-2.89, 3.8) * mm});
            skArc(sketch, "E931.filletArc", {"start": v(-5.43, 3.8) * mm, "mid": v(-5.48, 3.6) * mm, "end": v(-5.43, 3.4) * mm});
            skArc(sketch, "E932.filletArc", {"start": v(-4.97, 2.6) * mm, "mid": v(-4.82, 2.45) * mm, "end": v(-4.62, 2.4) * mm});
            skArc(sketch, "E933.filletArc", {"start": v(-3.7, 2.4) * mm, "mid": v(-3.5, 2.45) * mm, "end": v(-3.35, 2.6) * mm});
            skLineSegment(sketch, "E934", {"start": v(-1.27, 8.6) * mm, "end": v(-0.8, 9.4) * mm});
            skLineSegment(sketch, "E935", {"start": v(-0.46, 9.6) * mm, "end": v(0.46, 9.6) * mm});
            skLineSegment(sketch, "E936", {"start": v(0.8, 9.4) * mm, "end": v(1.27, 8.6) * mm});
            skLineSegment(sketch, "E937", {"start": v(0.8, 7.4) * mm, "end": v(1.27, 8.2) * mm});
            skLineSegment(sketch, "E938", {"start": v(-0.8, 7.4) * mm, "end": v(-1.27, 8.2) * mm});
            skArc(sketch, "E939.filletArc", {"start": v(-0.46, 9.6) * mm, "mid": v(-0.66, 9.55) * mm, "end": v(-0.8, 9.4) * mm});
            skArc(sketch, "E940.filletArc", {"start": v(0.8, 9.4) * mm, "mid": v(0.66, 9.55) * mm, "end": v(0.46, 9.6) * mm});
            skArc(sketch, "E941.filletArc", {"start": v(1.27, 8.2) * mm, "mid": v(1.32, 8.4) * mm, "end": v(1.27, 8.6) * mm});
            skArc(sketch, "E942.filletArc", {"start": v(-1.27, 8.6) * mm, "mid": v(-1.32, 8.4) * mm, "end": v(-1.27, 8.2) * mm});
            skArc(sketch, "E943.filletArc", {"start": v(-0.8, 7.4) * mm, "mid": v(-0.66, 7.25) * mm, "end": v(-0.46, 7.2) * mm});
            skArc(sketch, "E944.filletArc", {"start": v(0.46, 7.2) * mm, "mid": v(0.66, 7.25) * mm, "end": v(0.8, 7.4) * mm});
            skLineSegment(sketch, "E945", {"start": v(2.89, 6.2) * mm, "end": v(3.35, 7) * mm});
            skLineSegment(sketch, "E946", {"start": v(3.7, 7.2) * mm, "end": v(4.62, 7.2) * mm});
            skLineSegment(sketch, "E947", {"start": v(4.97, 7) * mm, "end": v(5.43, 6.2) * mm});
            skLineSegment(sketch, "E948", {"start": v(4.97, 5) * mm, "end": v(5.43, 5.8) * mm});
            skLineSegment(sketch, "E949", {"start": v(3.35, 5) * mm, "end": v(2.89, 5.8) * mm});
            skArc(sketch, "E950.filletArc", {"start": v(3.7, 7.2) * mm, "mid": v(3.5, 7.15) * mm, "end": v(3.35, 7) * mm});
            skArc(sketch, "E951.filletArc", {"start": v(4.97, 7) * mm, "mid": v(4.82, 7.15) * mm, "end": v(4.62, 7.2) * mm});
            skArc(sketch, "E952.filletArc", {"start": v(5.43, 5.8) * mm, "mid": v(5.48, 6) * mm, "end": v(5.43, 6.2) * mm});
            skArc(sketch, "E953.filletArc", {"start": v(2.89, 6.2) * mm, "mid": v(2.83, 6) * mm, "end": v(2.89, 5.8) * mm});
            skArc(sketch, "E954.filletArc", {"start": v(3.35, 5) * mm, "mid": v(3.5, 4.85) * mm, "end": v(3.7, 4.8) * mm});
            skArc(sketch, "E955.filletArc", {"start": v(4.62, 4.8) * mm, "mid": v(4.82, 4.85) * mm, "end": v(4.97, 5) * mm});
            skLineSegment(sketch, "E956", {"start": v(5.77, 6) * mm, "end": v(6.7, 6) * mm});
            skLineSegment(sketch, "E957", {"start": v(7.04, 5.8) * mm, "end": v(7.5, 5) * mm});
            skLineSegment(sketch, "E958", {"start": v(7.04, 3.8) * mm, "end": v(7.5, 4.6) * mm});
            skLineSegment(sketch, "E959", {"start": v(5.43, 3.8) * mm, "end": v(4.97, 4.6) * mm});
            skLineSegment(sketch, "E960", {"start": v(5.77, 3.6) * mm, "end": v(6.7, 3.6) * mm});
            skArc(sketch, "E961.filletArc", {"start": v(5.77, 6) * mm, "mid": v(5.57, 5.95) * mm, "end": v(5.43, 5.8) * mm});
            skArc(sketch, "E962.filletArc", {"start": v(7.04, 5.8) * mm, "mid": v(6.9, 5.95) * mm, "end": v(6.7, 6) * mm});
            skArc(sketch, "E963.filletArc", {"start": v(7.5, 4.6) * mm, "mid": v(7.56, 4.8) * mm, "end": v(7.5, 5) * mm});
            skArc(sketch, "E964.filletArc", {"start": v(4.97, 5) * mm, "mid": v(4.91, 4.8) * mm, "end": v(4.97, 4.6) * mm});
            skArc(sketch, "E965.filletArc", {"start": v(5.43, 3.8) * mm, "mid": v(5.57, 3.65) * mm, "end": v(5.77, 3.6) * mm});
            skArc(sketch, "E966.filletArc", {"start": v(6.7, 3.6) * mm, "mid": v(6.9, 3.65) * mm, "end": v(7.04, 3.8) * mm});
            skLineSegment(sketch, "E967", {"start": v(7.04, 3.4) * mm, "end": v(7.5, 2.6) * mm});
            skLineSegment(sketch, "E968", {"start": v(7.04, 1.4) * mm, "end": v(7.5, 2.2) * mm});
            skLineSegment(sketch, "E969", {"start": v(5.43, 1.4) * mm, "end": v(4.97, 2.2) * mm});
            skLineSegment(sketch, "E970", {"start": v(5.77, 1.2) * mm, "end": v(6.7, 1.2) * mm});
            skArc(sketch, "E971.filletArc", {"start": v(5.77, 3.6) * mm, "mid": v(5.57, 3.55) * mm, "end": v(5.43, 3.4) * mm});
            skArc(sketch, "E972.filletArc", {"start": v(7.04, 3.4) * mm, "mid": v(6.9, 3.55) * mm, "end": v(6.7, 3.6) * mm});
            skArc(sketch, "E973.filletArc", {"start": v(7.5, 2.2) * mm, "mid": v(7.56, 2.4) * mm, "end": v(7.5, 2.6) * mm});
            skArc(sketch, "E974.filletArc", {"start": v(4.97, 2.6) * mm, "mid": v(4.91, 2.4) * mm, "end": v(4.97, 2.2) * mm});
            skArc(sketch, "E975.filletArc", {"start": v(5.43, 1.4) * mm, "mid": v(5.57, 1.25) * mm, "end": v(5.77, 1.2) * mm});
            skArc(sketch, "E976.filletArc", {"start": v(6.7, 1.2) * mm, "mid": v(6.9, 1.25) * mm, "end": v(7.04, 1.4) * mm});
            skLineSegment(sketch, "E977", {"start": v(7.04, 1) * mm, "end": v(7.5, 0.2) * mm});
            skLineSegment(sketch, "E978", {"start": v(7.04, -1) * mm, "end": v(7.5, -0.2) * mm});
            skLineSegment(sketch, "E979", {"start": v(5.43, -1) * mm, "end": v(4.97, -0.2) * mm});
            skLineSegment(sketch, "E980", {"start": v(5.77, -1.2) * mm, "end": v(6.7, -1.2) * mm});
            skArc(sketch, "E981.filletArc", {"start": v(5.77, 1.2) * mm, "mid": v(5.57, 1.15) * mm, "end": v(5.43, 1) * mm});
            skArc(sketch, "E982.filletArc", {"start": v(7.04, 1) * mm, "mid": v(6.9, 1.15) * mm, "end": v(6.7, 1.2) * mm});
            skArc(sketch, "E983.filletArc", {"start": v(7.5, -0.2) * mm, "mid": v(7.56, 0) * mm, "end": v(7.5, 0.2) * mm});
            skArc(sketch, "E984.filletArc", {"start": v(4.97, 0.2) * mm, "mid": v(4.91, 0) * mm, "end": v(4.97, -0.2) * mm});
            skArc(sketch, "E985.filletArc", {"start": v(5.43, -1) * mm, "mid": v(5.57, -1.15) * mm, "end": v(5.77, -1.2) * mm});
            skArc(sketch, "E986.filletArc", {"start": v(6.7, -1.2) * mm, "mid": v(6.9, -1.15) * mm, "end": v(7.04, -1) * mm});
            skLineSegment(sketch, "E987", {"start": v(7.04, -1.4) * mm, "end": v(7.5, -2.2) * mm});
            skLineSegment(sketch, "E988", {"start": v(7.04, -3.4) * mm, "end": v(7.5, -2.6) * mm});
            skLineSegment(sketch, "E989", {"start": v(5.43, -3.4) * mm, "end": v(4.97, -2.6) * mm});
            skLineSegment(sketch, "E990", {"start": v(5.77, -3.6) * mm, "end": v(6.7, -3.6) * mm});
            skArc(sketch, "E991.filletArc", {"start": v(5.77, -1.2) * mm, "mid": v(5.57, -1.25) * mm, "end": v(5.43, -1.4) * mm});
            skArc(sketch, "E992.filletArc", {"start": v(7.04, -1.4) * mm, "mid": v(6.9, -1.25) * mm, "end": v(6.7, -1.2) * mm});
            skArc(sketch, "E993.filletArc", {"start": v(7.5, -2.6) * mm, "mid": v(7.56, -2.4) * mm, "end": v(7.5, -2.2) * mm});
            skArc(sketch, "E994.filletArc", {"start": v(4.97, -2.2) * mm, "mid": v(4.91, -2.4) * mm, "end": v(4.97, -2.6) * mm});
            skArc(sketch, "E995.filletArc", {"start": v(5.43, -3.4) * mm, "mid": v(5.57, -3.55) * mm, "end": v(5.77, -3.6) * mm});
            skArc(sketch, "E996.filletArc", {"start": v(6.7, -3.6) * mm, "mid": v(6.9, -3.55) * mm, "end": v(7.04, -3.4) * mm});
            skLineSegment(sketch, "E997", {"start": v(4.97, -2.6) * mm, "end": v(5.43, -3.4) * mm});
            skLineSegment(sketch, "E998", {"start": v(4.97, -4.6) * mm, "end": v(5.43, -3.8) * mm});
            skLineSegment(sketch, "E999", {"start": v(3.35, -4.6) * mm, "end": v(2.89, -3.8) * mm});
            skLineSegment(sketch, "E1000", {"start": v(3.7, -4.8) * mm, "end": v(4.62, -4.8) * mm});
            skArc(sketch, "E1001.filletArc", {"start": v(3.7, -2.4) * mm, "mid": v(3.5, -2.45) * mm, "end": v(3.35, -2.6) * mm});
            skArc(sketch, "E1002.filletArc", {"start": v(4.97, -2.6) * mm, "mid": v(4.82, -2.45) * mm, "end": v(4.62, -2.4) * mm});
            skArc(sketch, "E1003.filletArc", {"start": v(5.43, -3.8) * mm, "mid": v(5.48, -3.6) * mm, "end": v(5.43, -3.4) * mm});
            skArc(sketch, "E1004.filletArc", {"start": v(2.89, -3.4) * mm, "mid": v(2.83, -3.6) * mm, "end": v(2.89, -3.8) * mm});
            skArc(sketch, "E1005.filletArc", {"start": v(3.35, -4.6) * mm, "mid": v(3.5, -4.75) * mm, "end": v(3.7, -4.8) * mm});
            skArc(sketch, "E1006.filletArc", {"start": v(4.62, -4.8) * mm, "mid": v(4.82, -4.75) * mm, "end": v(4.97, -4.6) * mm});
            skLineSegment(sketch, "E1007", {"start": v(2.89, -3.8) * mm, "end": v(3.35, -4.6) * mm});
            skLineSegment(sketch, "E1008", {"start": v(2.89, -5.8) * mm, "end": v(3.35, -5) * mm});
            skLineSegment(sketch, "E1009", {"start": v(1.27, -5.8) * mm, "end": v(0.8, -5) * mm});
            skLineSegment(sketch, "E1010", {"start": v(1.62, -6) * mm, "end": v(2.54, -6) * mm});
            skArc(sketch, "E1011.filletArc", {"start": v(1.62, -3.6) * mm, "mid": v(1.42, -3.65) * mm, "end": v(1.27, -3.8) * mm});
            skArc(sketch, "E1012.filletArc", {"start": v(2.89, -3.8) * mm, "mid": v(2.74, -3.65) * mm, "end": v(2.54, -3.6) * mm});
            skArc(sketch, "E1013.filletArc", {"start": v(3.35, -5) * mm, "mid": v(3.4, -4.8) * mm, "end": v(3.35, -4.6) * mm});
            skArc(sketch, "E1014.filletArc", {"start": v(0.8, -4.6) * mm, "mid": v(0.75, -4.8) * mm, "end": v(0.8, -5) * mm});
            skArc(sketch, "E1015.filletArc", {"start": v(1.27, -5.8) * mm, "mid": v(1.42, -5.95) * mm, "end": v(1.62, -6) * mm});
            skArc(sketch, "E1016.filletArc", {"start": v(2.54, -6) * mm, "mid": v(2.74, -5.95) * mm, "end": v(2.89, -5.8) * mm});
            skLineSegment(sketch, "E1017", {"start": v(-1.27, -5.8) * mm, "end": v(-0.8, -5) * mm});
            skLineSegment(sketch, "E1018", {"start": v(0.8, -5) * mm, "end": v(1.27, -5.8) * mm});
            skLineSegment(sketch, "E1019", {"start": v(0.8, -7) * mm, "end": v(1.27, -6.2) * mm});
            skLineSegment(sketch, "E1020", {"start": v(-0.8, -7) * mm, "end": v(-1.27, -6.2) * mm});
            skLineSegment(sketch, "E1021", {"start": v(-0.46, -7.2) * mm, "end": v(0.46, -7.2) * mm});
            skArc(sketch, "E1022.filletArc", {"start": v(-0.46, -4.8) * mm, "mid": v(-0.66, -4.85) * mm, "end": v(-0.8, -5) * mm});
            skArc(sketch, "E1023.filletArc", {"start": v(0.8, -5) * mm, "mid": v(0.66, -4.85) * mm, "end": v(0.46, -4.8) * mm});
            skArc(sketch, "E1024.filletArc", {"start": v(1.27, -6.2) * mm, "mid": v(1.32, -6) * mm, "end": v(1.27, -5.8) * mm});
            skArc(sketch, "E1025.filletArc", {"start": v(-1.27, -5.8) * mm, "mid": v(-1.32, -6) * mm, "end": v(-1.27, -6.2) * mm});
            skArc(sketch, "E1026.filletArc", {"start": v(-0.8, -7) * mm, "mid": v(-0.66, -7.15) * mm, "end": v(-0.46, -7.2) * mm});
            skArc(sketch, "E1027.filletArc", {"start": v(0.46, -7.2) * mm, "mid": v(0.66, -7.15) * mm, "end": v(0.8, -7) * mm});
            skLineSegment(sketch, "E1028", {"start": v(-3.35, -4.6) * mm, "end": v(-2.89, -3.8) * mm});
            skLineSegment(sketch, "E1029", {"start": v(-1.27, -3.8) * mm, "end": v(-0.8, -4.6) * mm});
            skLineSegment(sketch, "E1030", {"start": v(-2.89, -5.8) * mm, "end": v(-3.35, -5) * mm});
            skLineSegment(sketch, "E1031", {"start": v(-2.54, -6) * mm, "end": v(-1.62, -6) * mm});
            skArc(sketch, "E1032.filletArc", {"start": v(-2.54, -3.6) * mm, "mid": v(-2.74, -3.65) * mm, "end": v(-2.89, -3.8) * mm});
            skArc(sketch, "E1033.filletArc", {"start": v(-1.27, -3.8) * mm, "mid": v(-1.42, -3.65) * mm, "end": v(-1.62, -3.6) * mm});
            skArc(sketch, "E1034.filletArc", {"start": v(-0.8, -5) * mm, "mid": v(-0.75, -4.8) * mm, "end": v(-0.8, -4.6) * mm});
            skArc(sketch, "E1035.filletArc", {"start": v(-3.35, -4.6) * mm, "mid": v(-3.4, -4.8) * mm, "end": v(-3.35, -5) * mm});
            skArc(sketch, "E1036.filletArc", {"start": v(-2.89, -5.8) * mm, "mid": v(-2.74, -5.95) * mm, "end": v(-2.54, -6) * mm});
            skArc(sketch, "E1037.filletArc", {"start": v(-1.62, -6) * mm, "mid": v(-1.42, -5.95) * mm, "end": v(-1.27, -5.8) * mm});
            skLineSegment(sketch, "E1038", {"start": v(-5.43, -3.4) * mm, "end": v(-4.97, -2.6) * mm});
            skLineSegment(sketch, "E1039", {"start": v(-3.35, -2.6) * mm, "end": v(-2.89, -3.4) * mm});
            skLineSegment(sketch, "E1040", {"start": v(-4.97, -4.6) * mm, "end": v(-5.43, -3.8) * mm});
            skLineSegment(sketch, "E1041", {"start": v(-4.62, -4.8) * mm, "end": v(-3.7, -4.8) * mm});
            skArc(sketch, "E1042.filletArc", {"start": v(-4.62, -2.4) * mm, "mid": v(-4.82, -2.45) * mm, "end": v(-4.97, -2.6) * mm});
            skArc(sketch, "E1043.filletArc", {"start": v(-3.35, -2.6) * mm, "mid": v(-3.5, -2.45) * mm, "end": v(-3.7, -2.4) * mm});
            skArc(sketch, "E1044.filletArc", {"start": v(-2.89, -3.8) * mm, "mid": v(-2.83, -3.6) * mm, "end": v(-2.89, -3.4) * mm});
            skArc(sketch, "E1045.filletArc", {"start": v(-5.43, -3.4) * mm, "mid": v(-5.48, -3.6) * mm, "end": v(-5.43, -3.8) * mm});
            skArc(sketch, "E1046.filletArc", {"start": v(-4.97, -4.6) * mm, "mid": v(-4.82, -4.75) * mm, "end": v(-4.62, -4.8) * mm});
            skArc(sketch, "E1047.filletArc", {"start": v(-3.7, -4.8) * mm, "mid": v(-3.5, -4.75) * mm, "end": v(-3.35, -4.6) * mm});
            skLineSegment(sketch, "E1048", {"start": v(-7.5, -2.2) * mm, "end": v(-7.04, -1.4) * mm});
            skLineSegment(sketch, "E1049", {"start": v(-6.7, -1.2) * mm, "end": v(-5.77, -1.2) * mm});
            skLineSegment(sketch, "E1050", {"start": v(-5.43, -1.4) * mm, "end": v(-4.97, -2.2) * mm});
            skLineSegment(sketch, "E1051", {"start": v(-7.04, -3.4) * mm, "end": v(-7.5, -2.6) * mm});
            skLineSegment(sketch, "E1052", {"start": v(-6.7, -3.6) * mm, "end": v(-5.77, -3.6) * mm});
            skArc(sketch, "E1053.filletArc", {"start": v(-6.7, -1.2) * mm, "mid": v(-6.9, -1.25) * mm, "end": v(-7.04, -1.4) * mm});
            skArc(sketch, "E1054.filletArc", {"start": v(-5.43, -1.4) * mm, "mid": v(-5.57, -1.25) * mm, "end": v(-5.77, -1.2) * mm});
            skArc(sketch, "E1055.filletArc", {"start": v(-4.97, -2.6) * mm, "mid": v(-4.91, -2.4) * mm, "end": v(-4.97, -2.2) * mm});
            skArc(sketch, "E1056.filletArc", {"start": v(-7.5, -2.2) * mm, "mid": v(-7.56, -2.4) * mm, "end": v(-7.5, -2.6) * mm});
            skArc(sketch, "E1057.filletArc", {"start": v(-7.04, -3.4) * mm, "mid": v(-6.9, -3.55) * mm, "end": v(-6.7, -3.6) * mm});
            skArc(sketch, "E1058.filletArc", {"start": v(-5.77, -3.6) * mm, "mid": v(-5.57, -3.55) * mm, "end": v(-5.43, -3.4) * mm});
            skLineSegment(sketch, "E1059", {"start": v(-7.5, 0.2) * mm, "end": v(-7.04, 1) * mm});
            skLineSegment(sketch, "E1060", {"start": v(-6.7, 1.2) * mm, "end": v(-5.77, 1.2) * mm});
            skLineSegment(sketch, "E1061", {"start": v(-5.43, 1) * mm, "end": v(-4.97, 0.2) * mm});
            skLineSegment(sketch, "E1062", {"start": v(-7.04, -1) * mm, "end": v(-7.5, -0.2) * mm});
            skArc(sketch, "E1063.filletArc", {"start": v(-6.7, 1.2) * mm, "mid": v(-6.9, 1.15) * mm, "end": v(-7.04, 1) * mm});
            skArc(sketch, "E1064.filletArc", {"start": v(-5.43, 1) * mm, "mid": v(-5.57, 1.15) * mm, "end": v(-5.77, 1.2) * mm});
            skArc(sketch, "E1065.filletArc", {"start": v(-4.97, -0.2) * mm, "mid": v(-4.91, 0) * mm, "end": v(-4.97, 0.2) * mm});
            skArc(sketch, "E1066.filletArc", {"start": v(-7.5, 0.2) * mm, "mid": v(-7.56, 0) * mm, "end": v(-7.5, -0.2) * mm});
            skArc(sketch, "E1067.filletArc", {"start": v(-7.04, -1) * mm, "mid": v(-6.9, -1.15) * mm, "end": v(-6.7, -1.2) * mm});
            skArc(sketch, "E1068.filletArc", {"start": v(-5.77, -1.2) * mm, "mid": v(-5.57, -1.15) * mm, "end": v(-5.43, -1) * mm});
            skLineSegment(sketch, "E1069", {"start": v(1.62, 8.4) * mm, "end": v(2.54, 8.4) * mm});
            skLineSegment(sketch, "E1070", {"start": v(2.89, 8.2) * mm, "end": v(3.35, 7.4) * mm});
            skLineSegment(sketch, "E1071", {"start": v(1.27, 6.2) * mm, "end": v(0.8, 7) * mm});
            skArc(sketch, "E1072.filletArc", {"start": v(1.62, 8.4) * mm, "mid": v(1.42, 8.35) * mm, "end": v(1.27, 8.2) * mm});
            skArc(sketch, "E1073.filletArc", {"start": v(2.89, 8.2) * mm, "mid": v(2.74, 8.35) * mm, "end": v(2.54, 8.4) * mm});
            skArc(sketch, "E1074.filletArc", {"start": v(3.35, 7) * mm, "mid": v(3.4, 7.2) * mm, "end": v(3.35, 7.4) * mm});
            skArc(sketch, "E1075.filletArc", {"start": v(0.8, 7.4) * mm, "mid": v(0.75, 7.2) * mm, "end": v(0.8, 7) * mm});
            skArc(sketch, "E1076.filletArc", {"start": v(1.27, 6.2) * mm, "mid": v(1.42, 6.05) * mm, "end": v(1.62, 6) * mm});
            skArc(sketch, "E1077.filletArc", {"start": v(2.54, 6) * mm, "mid": v(2.74, 6.05) * mm, "end": v(2.89, 6.2) * mm});
            skLineSegment(sketch, "E1078", {"start": v(-7.5, 2.6) * mm, "end": v(-7.04, 3.4) * mm});
            skLineSegment(sketch, "E1079", {"start": v(-6.7, 3.6) * mm, "end": v(-5.77, 3.6) * mm});
            skLineSegment(sketch, "E1080", {"start": v(-5.43, 3.4) * mm, "end": v(-4.97, 2.6) * mm});
            skLineSegment(sketch, "E1081", {"start": v(-7.04, 1.4) * mm, "end": v(-7.5, 2.2) * mm});
            skArc(sketch, "E1082.filletArc", {"start": v(-6.7, 3.6) * mm, "mid": v(-6.9, 3.55) * mm, "end": v(-7.04, 3.4) * mm});
            skArc(sketch, "E1083.filletArc", {"start": v(-5.43, 3.4) * mm, "mid": v(-5.57, 3.55) * mm, "end": v(-5.77, 3.6) * mm});
            skArc(sketch, "E1084.filletArc", {"start": v(-4.97, 2.2) * mm, "mid": v(-4.91, 2.4) * mm, "end": v(-4.97, 2.6) * mm});
            skArc(sketch, "E1085.filletArc", {"start": v(-7.5, 2.6) * mm, "mid": v(-7.56, 2.4) * mm, "end": v(-7.5, 2.2) * mm});
            skArc(sketch, "E1086.filletArc", {"start": v(-7.04, 1.4) * mm, "mid": v(-6.9, 1.25) * mm, "end": v(-6.7, 1.2) * mm});
            skArc(sketch, "E1087.filletArc", {"start": v(-5.77, 1.2) * mm, "mid": v(-5.57, 1.25) * mm, "end": v(-5.43, 1.4) * mm});
            skLineSegment(sketch, "E1088", {"start": v(-7.5, 5) * mm, "end": v(-7.04, 5.8) * mm});
            skLineSegment(sketch, "E1089", {"start": v(-6.7, 6) * mm, "end": v(-5.77, 6) * mm});
            skLineSegment(sketch, "E1090", {"start": v(-5.43, 5.8) * mm, "end": v(-4.97, 5) * mm});
            skLineSegment(sketch, "E1091", {"start": v(-7.04, 3.8) * mm, "end": v(-7.5, 4.6) * mm});
            skArc(sketch, "E1092.filletArc", {"start": v(-6.7, 6) * mm, "mid": v(-6.9, 5.95) * mm, "end": v(-7.04, 5.8) * mm});
            skArc(sketch, "E1093.filletArc", {"start": v(-5.43, 5.8) * mm, "mid": v(-5.57, 5.95) * mm, "end": v(-5.77, 6) * mm});
            skArc(sketch, "E1094.filletArc", {"start": v(-4.97, 4.6) * mm, "mid": v(-4.91, 4.8) * mm, "end": v(-4.97, 5) * mm});
            skArc(sketch, "E1095.filletArc", {"start": v(-7.5, 5) * mm, "mid": v(-7.56, 4.8) * mm, "end": v(-7.5, 4.6) * mm});
            skArc(sketch, "E1096.filletArc", {"start": v(-7.04, 3.8) * mm, "mid": v(-6.9, 3.65) * mm, "end": v(-6.7, 3.6) * mm});
            skArc(sketch, "E1097.filletArc", {"start": v(-5.77, 3.6) * mm, "mid": v(-5.57, 3.65) * mm, "end": v(-5.43, 3.8) * mm});
            skLineSegment(sketch, "E1098", {"start": v(-5.43, 6.2) * mm, "end": v(-4.97, 7) * mm});
            skLineSegment(sketch, "E1099", {"start": v(-4.62, 7.2) * mm, "end": v(-3.7, 7.2) * mm});
            skLineSegment(sketch, "E1100", {"start": v(-3.35, 7) * mm, "end": v(-2.89, 6.2) * mm});
            skLineSegment(sketch, "E1101", {"start": v(-4.97, 5) * mm, "end": v(-5.43, 5.8) * mm});
            skArc(sketch, "E1102.filletArc", {"start": v(-4.62, 7.2) * mm, "mid": v(-4.82, 7.15) * mm, "end": v(-4.97, 7) * mm});
            skArc(sketch, "E1103.filletArc", {"start": v(-3.35, 7) * mm, "mid": v(-3.5, 7.15) * mm, "end": v(-3.7, 7.2) * mm});
            skArc(sketch, "E1104.filletArc", {"start": v(-2.89, 5.8) * mm, "mid": v(-2.83, 6) * mm, "end": v(-2.89, 6.2) * mm});
            skArc(sketch, "E1105.filletArc", {"start": v(-5.43, 6.2) * mm, "mid": v(-5.48, 6) * mm, "end": v(-5.43, 5.8) * mm});
            skArc(sketch, "E1106.filletArc", {"start": v(-4.97, 5) * mm, "mid": v(-4.82, 4.85) * mm, "end": v(-4.62, 4.8) * mm});
            skArc(sketch, "E1107.filletArc", {"start": v(-3.7, 4.8) * mm, "mid": v(-3.5, 4.85) * mm, "end": v(-3.35, 5) * mm});
            skLineSegment(sketch, "E1108", {"start": v(-3.35, 7.4) * mm, "end": v(-2.89, 8.2) * mm});
            skLineSegment(sketch, "E1109", {"start": v(-2.54, 8.4) * mm, "end": v(-1.62, 8.4) * mm});
            skLineSegment(sketch, "E1110", {"start": v(-1.27, 8.2) * mm, "end": v(-0.8, 7.4) * mm});
            skLineSegment(sketch, "E1111", {"start": v(-2.89, 6.2) * mm, "end": v(-3.35, 7) * mm});
            skArc(sketch, "E1112.filletArc", {"start": v(-2.54, 8.4) * mm, "mid": v(-2.74, 8.35) * mm, "end": v(-2.89, 8.2) * mm});
            skArc(sketch, "E1113.filletArc", {"start": v(-1.27, 8.2) * mm, "mid": v(-1.42, 8.35) * mm, "end": v(-1.62, 8.4) * mm});
            skArc(sketch, "E1114.filletArc", {"start": v(-0.8, 7) * mm, "mid": v(-0.75, 7.2) * mm, "end": v(-0.8, 7.4) * mm});
            skArc(sketch, "E1115.filletArc", {"start": v(-3.35, 7.4) * mm, "mid": v(-3.4, 7.2) * mm, "end": v(-3.35, 7) * mm});
            skArc(sketch, "E1116.filletArc", {"start": v(-2.89, 6.2) * mm, "mid": v(-2.74, 6.05) * mm, "end": v(-2.54, 6) * mm});
            skArc(sketch, "E1117.filletArc", {"start": v(-1.62, 6) * mm, "mid": v(-1.42, 6.05) * mm, "end": v(-1.27, 6.2) * mm});
            skLineSegment(sketch, "E1118", {"start": v(-7.5, -4.6) * mm, "end": v(-7.04, -3.8) * mm});
            skLineSegment(sketch, "E1119", {"start": v(-5.43, -3.8) * mm, "end": v(-4.97, -4.6) * mm});
            skLineSegment(sketch, "E1120", {"start": v(-5.43, -5.8) * mm, "end": v(-4.97, -5) * mm});
            skLineSegment(sketch, "E1121", {"start": v(-7.04, -5.8) * mm, "end": v(-7.5, -5) * mm});
            skLineSegment(sketch, "E1122", {"start": v(-6.7, -6) * mm, "end": v(-5.77, -6) * mm});
            skArc(sketch, "E1123.filletArc", {"start": v(-6.7, -3.6) * mm, "mid": v(-6.9, -3.65) * mm, "end": v(-7.04, -3.8) * mm});
            skArc(sketch, "E1124.filletArc", {"start": v(-5.43, -3.8) * mm, "mid": v(-5.57, -3.65) * mm, "end": v(-5.77, -3.6) * mm});
            skArc(sketch, "E1125.filletArc", {"start": v(-4.97, -5) * mm, "mid": v(-4.91, -4.8) * mm, "end": v(-4.97, -4.6) * mm});
            skArc(sketch, "E1126.filletArc", {"start": v(-7.5, -4.6) * mm, "mid": v(-7.56, -4.8) * mm, "end": v(-7.5, -5) * mm});
            skArc(sketch, "E1127.filletArc", {"start": v(-7.04, -5.8) * mm, "mid": v(-6.9, -5.95) * mm, "end": v(-6.7, -6) * mm});
            skArc(sketch, "E1128.filletArc", {"start": v(-5.77, -6) * mm, "mid": v(-5.57, -5.95) * mm, "end": v(-5.43, -5.8) * mm});
            skLineSegment(sketch, "E1129", {"start": v(-3.35, -5) * mm, "end": v(-2.89, -5.8) * mm});
            skLineSegment(sketch, "E1130", {"start": v(-3.35, -7) * mm, "end": v(-2.89, -6.2) * mm});
            skLineSegment(sketch, "E1131", {"start": v(-4.97, -7) * mm, "end": v(-5.43, -6.2) * mm});
            skLineSegment(sketch, "E1132", {"start": v(-4.62, -7.2) * mm, "end": v(-3.7, -7.2) * mm});
            skArc(sketch, "E1133.filletArc", {"start": v(-4.62, -4.8) * mm, "mid": v(-4.82, -4.85) * mm, "end": v(-4.97, -5) * mm});
            skArc(sketch, "E1134.filletArc", {"start": v(-3.35, -5) * mm, "mid": v(-3.5, -4.85) * mm, "end": v(-3.7, -4.8) * mm});
            skArc(sketch, "E1135.filletArc", {"start": v(-2.89, -6.2) * mm, "mid": v(-2.83, -6) * mm, "end": v(-2.89, -5.8) * mm});
            skArc(sketch, "E1136.filletArc", {"start": v(-5.43, -5.8) * mm, "mid": v(-5.48, -6) * mm, "end": v(-5.43, -6.2) * mm});
            skArc(sketch, "E1137.filletArc", {"start": v(-4.97, -7) * mm, "mid": v(-4.82, -7.15) * mm, "end": v(-4.62, -7.2) * mm});
            skArc(sketch, "E1138.filletArc", {"start": v(-3.7, -7.2) * mm, "mid": v(-3.5, -7.15) * mm, "end": v(-3.35, -7) * mm});
            skLineSegment(sketch, "E1139", {"start": v(-1.27, -6.2) * mm, "end": v(-0.8, -7) * mm});
            skLineSegment(sketch, "E1140", {"start": v(-1.27, -8.2) * mm, "end": v(-0.8, -7.4) * mm});
            skLineSegment(sketch, "E1141", {"start": v(-2.89, -8.2) * mm, "end": v(-3.35, -7.4) * mm});
            skLineSegment(sketch, "E1142", {"start": v(-2.54, -8.4) * mm, "end": v(-1.62, -8.4) * mm});
            skArc(sketch, "E1143.filletArc", {"start": v(-2.54, -6) * mm, "mid": v(-2.74, -6.05) * mm, "end": v(-2.89, -6.2) * mm});
            skArc(sketch, "E1144.filletArc", {"start": v(-1.27, -6.2) * mm, "mid": v(-1.42, -6.05) * mm, "end": v(-1.62, -6) * mm});
            skArc(sketch, "E1145.filletArc", {"start": v(-0.8, -7.4) * mm, "mid": v(-0.75, -7.2) * mm, "end": v(-0.8, -7) * mm});
            skArc(sketch, "E1146.filletArc", {"start": v(-3.35, -7) * mm, "mid": v(-3.4, -7.2) * mm, "end": v(-3.35, -7.4) * mm});
            skArc(sketch, "E1147.filletArc", {"start": v(-2.89, -8.2) * mm, "mid": v(-2.74, -8.35) * mm, "end": v(-2.54, -8.4) * mm});
            skArc(sketch, "E1148.filletArc", {"start": v(-1.62, -8.4) * mm, "mid": v(-1.42, -8.35) * mm, "end": v(-1.27, -8.2) * mm});
            skLineSegment(sketch, "E1149", {"start": v(2.89, -6.2) * mm, "end": v(3.35, -7) * mm});
            skLineSegment(sketch, "E1150", {"start": v(2.89, -8.2) * mm, "end": v(3.35, -7.4) * mm});
            skLineSegment(sketch, "E1151", {"start": v(1.27, -8.2) * mm, "end": v(0.8, -7.4) * mm});
            skLineSegment(sketch, "E1152", {"start": v(1.62, -8.4) * mm, "end": v(2.54, -8.4) * mm});
            skArc(sketch, "E1153.filletArc", {"start": v(1.62, -6) * mm, "mid": v(1.42, -6.05) * mm, "end": v(1.27, -6.2) * mm});
            skArc(sketch, "E1154.filletArc", {"start": v(2.89, -6.2) * mm, "mid": v(2.74, -6.05) * mm, "end": v(2.54, -6) * mm});
            skArc(sketch, "E1155.filletArc", {"start": v(3.35, -7.4) * mm, "mid": v(3.4, -7.2) * mm, "end": v(3.35, -7) * mm});
            skArc(sketch, "E1156.filletArc", {"start": v(0.8, -7) * mm, "mid": v(0.75, -7.2) * mm, "end": v(0.8, -7.4) * mm});
            skArc(sketch, "E1157.filletArc", {"start": v(1.27, -8.2) * mm, "mid": v(1.42, -8.35) * mm, "end": v(1.62, -8.4) * mm});
            skArc(sketch, "E1158.filletArc", {"start": v(2.54, -8.4) * mm, "mid": v(2.74, -8.35) * mm, "end": v(2.89, -8.2) * mm});
            skLineSegment(sketch, "E1159", {"start": v(4.97, -5) * mm, "end": v(5.43, -5.8) * mm});
            skLineSegment(sketch, "E1160", {"start": v(4.97, -7) * mm, "end": v(5.43, -6.2) * mm});
            skLineSegment(sketch, "E1161", {"start": v(3.35, -7) * mm, "end": v(2.89, -6.2) * mm});
            skLineSegment(sketch, "E1162", {"start": v(3.7, -7.2) * mm, "end": v(4.62, -7.2) * mm});
            skArc(sketch, "E1163.filletArc", {"start": v(3.7, -4.8) * mm, "mid": v(3.5, -4.85) * mm, "end": v(3.35, -5) * mm});
            skArc(sketch, "E1164.filletArc", {"start": v(4.97, -5) * mm, "mid": v(4.82, -4.85) * mm, "end": v(4.62, -4.8) * mm});
            skArc(sketch, "E1165.filletArc", {"start": v(5.43, -6.2) * mm, "mid": v(5.48, -6) * mm, "end": v(5.43, -5.8) * mm});
            skArc(sketch, "E1166.filletArc", {"start": v(2.89, -5.8) * mm, "mid": v(2.83, -6) * mm, "end": v(2.89, -6.2) * mm});
            skArc(sketch, "E1167.filletArc", {"start": v(3.35, -7) * mm, "mid": v(3.5, -7.15) * mm, "end": v(3.7, -7.2) * mm});
            skArc(sketch, "E1168.filletArc", {"start": v(4.62, -7.2) * mm, "mid": v(4.82, -7.15) * mm, "end": v(4.97, -7) * mm});
            skLineSegment(sketch, "E1169", {"start": v(7.04, -3.8) * mm, "end": v(7.5, -4.6) * mm});
            skLineSegment(sketch, "E1170", {"start": v(7.04, -5.8) * mm, "end": v(7.5, -5) * mm});
            skLineSegment(sketch, "E1171", {"start": v(5.43, -5.8) * mm, "end": v(4.97, -5) * mm});
            skLineSegment(sketch, "E1172", {"start": v(5.77, -6) * mm, "end": v(6.7, -6) * mm});
            skArc(sketch, "E1173.filletArc", {"start": v(5.77, -3.6) * mm, "mid": v(5.57, -3.65) * mm, "end": v(5.43, -3.8) * mm});
            skArc(sketch, "E1174.filletArc", {"start": v(7.04, -3.8) * mm, "mid": v(6.9, -3.65) * mm, "end": v(6.7, -3.6) * mm});
            skArc(sketch, "E1175.filletArc", {"start": v(7.5, -5) * mm, "mid": v(7.56, -4.8) * mm, "end": v(7.5, -4.6) * mm});
            skArc(sketch, "E1176.filletArc", {"start": v(4.97, -4.6) * mm, "mid": v(4.91, -4.8) * mm, "end": v(4.97, -5) * mm});
            skArc(sketch, "E1177.filletArc", {"start": v(5.43, -5.8) * mm, "mid": v(5.57, -5.95) * mm, "end": v(5.77, -6) * mm});
            skArc(sketch, "E1178.filletArc", {"start": v(6.7, -6) * mm, "mid": v(6.9, -5.95) * mm, "end": v(7.04, -5.8) * mm});
            skLineSegment(sketch, "E1179", {"start": v(0.8, -7.4) * mm, "end": v(1.27, -8.2) * mm});
            skLineSegment(sketch, "E1180", {"start": v(0.8, -9.4) * mm, "end": v(1.27, -8.6) * mm});
            skLineSegment(sketch, "E1181", {"start": v(-0.8, -9.4) * mm, "end": v(-1.27, -8.6) * mm});
            skLineSegment(sketch, "E1182", {"start": v(-0.46, -9.6) * mm, "end": v(0.46, -9.6) * mm});
            skArc(sketch, "E1183.filletArc", {"start": v(-0.46, -7.2) * mm, "mid": v(-0.66, -7.25) * mm, "end": v(-0.8, -7.4) * mm});
            skArc(sketch, "E1184.filletArc", {"start": v(0.8, -7.4) * mm, "mid": v(0.66, -7.25) * mm, "end": v(0.46, -7.2) * mm});
            skArc(sketch, "E1185.filletArc", {"start": v(1.27, -8.6) * mm, "mid": v(1.32, -8.4) * mm, "end": v(1.27, -8.2) * mm});
            skArc(sketch, "E1186.filletArc", {"start": v(-1.27, -8.2) * mm, "mid": v(-1.32, -8.4) * mm, "end": v(-1.27, -8.6) * mm});
            skArc(sketch, "E1187.filletArc", {"start": v(-0.8, -9.4) * mm, "mid": v(-0.66, -9.55) * mm, "end": v(-0.46, -9.6) * mm});
            skArc(sketch, "E1188.filletArc", {"start": v(0.46, -9.6) * mm, "mid": v(0.66, -9.55) * mm, "end": v(0.8, -9.4) * mm});
            skSolve(sketch);
        }
        {
            var Q0;
            Q0=qCreatedBy(id+"F2.planeOp",FACE);
            cPlane(context, id + "F4", {"entities" : qUnion([Q0]), "cplaneType" : CPlaneType.OFFSET, "offset" : 0.4 * mm, "width" : 150 * mm, "height" : 150 * mm});
        }
        {
            var Q0;
            Q0=qCreatedBy(id+"F4.planeOp",FACE);
            var sketch = newSketch(context, id + "F5", { "sketchPlane" : qUnion([Q0])});
            skPoint(sketch, "E1189.middle", {"position": v(0, 0) * mm});
            skLineSegment(sketch, "E1190", {"start": v(-1.27, 0.2) * mm, "end": v(-0.8, 1) * mm});
            skLineSegment(sketch, "E1191", {"start": v(-0.46, 1.2) * mm, "end": v(0.46, 1.2) * mm});
            skLineSegment(sketch, "E1192", {"start": v(0.8, 1) * mm, "end": v(1.27, 0.2) * mm});
            skLineSegment(sketch, "E1193", {"start": v(1.27, -0.2) * mm, "end": v(0.8, -1) * mm});
            skLineSegment(sketch, "E1194", {"start": v(0.46, -1.2) * mm, "end": v(-0.46, -1.2) * mm});
            skLineSegment(sketch, "E1195", {"start": v(-0.8, -1) * mm, "end": v(-1.27, -0.2) * mm});
            skArc(sketch, "E1196.filletArc", {"start": v(-0.46, 1.2) * mm, "mid": v(-0.66, 1.15) * mm, "end": v(-0.8, 1) * mm});
            skArc(sketch, "E1197.filletArc", {"start": v(0.8, 1) * mm, "mid": v(0.66, 1.15) * mm, "end": v(0.46, 1.2) * mm});
            skArc(sketch, "E1198.filletArc", {"start": v(1.27, -0.2) * mm, "mid": v(1.32, 0) * mm, "end": v(1.27, 0.2) * mm});
            skArc(sketch, "E1199.filletArc", {"start": v(0.46, -1.2) * mm, "mid": v(0.66, -1.15) * mm, "end": v(0.8, -1) * mm});
            skArc(sketch, "E1200.filletArc", {"start": v(-0.8, -1) * mm, "mid": v(-0.66, -1.15) * mm, "end": v(-0.46, -1.2) * mm});
            skArc(sketch, "E1201.filletArc", {"start": v(-1.27, 0.2) * mm, "mid": v(-1.32, 0) * mm, "end": v(-1.27, -0.2) * mm});
            skLineSegment(sketch, "E1202", {"start": v(0.8, 1.4) * mm, "end": v(1.27, 2.2) * mm});
            skLineSegment(sketch, "E1203", {"start": v(1.62, 2.4) * mm, "end": v(2.54, 2.4) * mm});
            skLineSegment(sketch, "E1204", {"start": v(2.89, 2.2) * mm, "end": v(3.35, 1.4) * mm});
            skLineSegment(sketch, "E1205", {"start": v(3.35, 1) * mm, "end": v(2.89, 0.2) * mm});
            skLineSegment(sketch, "E1206", {"start": v(2.54, 0) * mm, "end": v(1.62, 0) * mm});
            skLineSegment(sketch, "E1207", {"start": v(1.27, 0.2) * mm, "end": v(0.8, 1) * mm});
            skArc(sketch, "E1208.filletArc", {"start": v(1.62, 2.4) * mm, "mid": v(1.42, 2.35) * mm, "end": v(1.27, 2.2) * mm});
            skArc(sketch, "E1209.filletArc", {"start": v(2.89, 2.2) * mm, "mid": v(2.74, 2.35) * mm, "end": v(2.54, 2.4) * mm});
            skArc(sketch, "E1210.filletArc", {"start": v(3.35, 1) * mm, "mid": v(3.4, 1.2) * mm, "end": v(3.35, 1.4) * mm});
            skArc(sketch, "E1211.filletArc", {"start": v(2.54, 0) * mm, "mid": v(2.74, 0.05) * mm, "end": v(2.89, 0.2) * mm});
            skArc(sketch, "E1212.filletArc", {"start": v(1.27, 0.2) * mm, "mid": v(1.42, 0.05) * mm, "end": v(1.62, 0) * mm});
            skArc(sketch, "E1213.filletArc", {"start": v(0.8, 1.4) * mm, "mid": v(0.75, 1.2) * mm, "end": v(0.8, 1) * mm});
            skLineSegment(sketch, "E1214", {"start": v(-1.27, 2.6) * mm, "end": v(-0.8, 3.4) * mm});
            skLineSegment(sketch, "E1215", {"start": v(-0.46, 3.6) * mm, "end": v(0.46, 3.6) * mm});
            skLineSegment(sketch, "E1216", {"start": v(0.8, 3.4) * mm, "end": v(1.27, 2.6) * mm});
            skLineSegment(sketch, "E1217", {"start": v(1.27, 2.2) * mm, "end": v(0.8, 1.4) * mm});
            skLineSegment(sketch, "E1218", {"start": v(0.46, 1.2) * mm, "end": v(-0.46, 1.2) * mm});
            skLineSegment(sketch, "E1219", {"start": v(-0.8, 1.4) * mm, "end": v(-1.27, 2.2) * mm});
            skArc(sketch, "E1220.filletArc", {"start": v(-0.46, 3.6) * mm, "mid": v(-0.66, 3.55) * mm, "end": v(-0.8, 3.4) * mm});
            skArc(sketch, "E1221.filletArc", {"start": v(0.8, 3.4) * mm, "mid": v(0.66, 3.55) * mm, "end": v(0.46, 3.6) * mm});
            skArc(sketch, "E1222.filletArc", {"start": v(1.27, 2.2) * mm, "mid": v(1.32, 2.4) * mm, "end": v(1.27, 2.6) * mm});
            skArc(sketch, "E1223.filletArc", {"start": v(0.46, 1.2) * mm, "mid": v(0.66, 1.25) * mm, "end": v(0.8, 1.4) * mm});
            skArc(sketch, "E1224.filletArc", {"start": v(-0.8, 1.4) * mm, "mid": v(-0.66, 1.25) * mm, "end": v(-0.46, 1.2) * mm});
            skArc(sketch, "E1225.filletArc", {"start": v(-1.27, 2.6) * mm, "mid": v(-1.32, 2.4) * mm, "end": v(-1.27, 2.2) * mm});
            skLineSegment(sketch, "E1226", {"start": v(-3.35, 1.4) * mm, "end": v(-2.89, 2.2) * mm});
            skLineSegment(sketch, "E1227", {"start": v(-2.54, 2.4) * mm, "end": v(-1.62, 2.4) * mm});
            skLineSegment(sketch, "E1228", {"start": v(-1.27, 2.2) * mm, "end": v(-0.8, 1.4) * mm});
            skLineSegment(sketch, "E1229", {"start": v(-0.8, 1) * mm, "end": v(-1.27, 0.2) * mm});
            skLineSegment(sketch, "E1230", {"start": v(-1.62, 0) * mm, "end": v(-2.54, 0) * mm});
            skLineSegment(sketch, "E1231", {"start": v(-2.89, 0.2) * mm, "end": v(-3.35, 1) * mm});
            skArc(sketch, "E1232.filletArc", {"start": v(-2.54, 2.4) * mm, "mid": v(-2.74, 2.35) * mm, "end": v(-2.89, 2.2) * mm});
            skArc(sketch, "E1233.filletArc", {"start": v(-1.27, 2.2) * mm, "mid": v(-1.42, 2.35) * mm, "end": v(-1.62, 2.4) * mm});
            skArc(sketch, "E1234.filletArc", {"start": v(-0.8, 1) * mm, "mid": v(-0.75, 1.2) * mm, "end": v(-0.8, 1.4) * mm});
            skArc(sketch, "E1235.filletArc", {"start": v(-1.62, 0) * mm, "mid": v(-1.42, 0.05) * mm, "end": v(-1.27, 0.2) * mm});
            skArc(sketch, "E1236.filletArc", {"start": v(-2.89, 0.2) * mm, "mid": v(-2.74, 0.05) * mm, "end": v(-2.54, 0) * mm});
            skArc(sketch, "E1237.filletArc", {"start": v(-3.35, 1.4) * mm, "mid": v(-3.4, 1.2) * mm, "end": v(-3.35, 1) * mm});
            skLineSegment(sketch, "E1238", {"start": v(-3.35, -1) * mm, "end": v(-2.89, -0.2) * mm});
            skLineSegment(sketch, "E1239", {"start": v(-2.54, 0) * mm, "end": v(-1.62, 0) * mm});
            skLineSegment(sketch, "E1240", {"start": v(-1.27, -0.2) * mm, "end": v(-0.8, -1) * mm});
            skLineSegment(sketch, "E1241", {"start": v(-0.8, -1.4) * mm, "end": v(-1.27, -2.2) * mm});
            skLineSegment(sketch, "E1242", {"start": v(-1.62, -2.4) * mm, "end": v(-2.54, -2.4) * mm});
            skLineSegment(sketch, "E1243", {"start": v(-2.89, -2.2) * mm, "end": v(-3.35, -1.4) * mm});
            skArc(sketch, "E1244.filletArc", {"start": v(-2.54, 0) * mm, "mid": v(-2.74, -0.05) * mm, "end": v(-2.89, -0.2) * mm});
            skArc(sketch, "E1245.filletArc", {"start": v(-1.27, -0.2) * mm, "mid": v(-1.42, -0.05) * mm, "end": v(-1.62, 0) * mm});
            skArc(sketch, "E1246.filletArc", {"start": v(-0.8, -1.4) * mm, "mid": v(-0.75, -1.2) * mm, "end": v(-0.8, -1) * mm});
            skArc(sketch, "E1247.filletArc", {"start": v(-1.62, -2.4) * mm, "mid": v(-1.42, -2.35) * mm, "end": v(-1.27, -2.2) * mm});
            skArc(sketch, "E1248.filletArc", {"start": v(-2.89, -2.2) * mm, "mid": v(-2.74, -2.35) * mm, "end": v(-2.54, -2.4) * mm});
            skArc(sketch, "E1249.filletArc", {"start": v(-3.35, -1) * mm, "mid": v(-3.4, -1.2) * mm, "end": v(-3.35, -1.4) * mm});
            skLineSegment(sketch, "E1250", {"start": v(-1.27, -2.2) * mm, "end": v(-0.8, -1.4) * mm});
            skLineSegment(sketch, "E1251", {"start": v(-0.46, -1.2) * mm, "end": v(0.46, -1.2) * mm});
            skLineSegment(sketch, "E1252", {"start": v(0.8, -1.4) * mm, "end": v(1.27, -2.2) * mm});
            skLineSegment(sketch, "E1253", {"start": v(1.27, -2.6) * mm, "end": v(0.8, -3.4) * mm});
            skLineSegment(sketch, "E1254", {"start": v(0.46, -3.6) * mm, "end": v(-0.46, -3.6) * mm});
            skLineSegment(sketch, "E1255", {"start": v(-0.8, -3.4) * mm, "end": v(-1.27, -2.6) * mm});
            skArc(sketch, "E1256.filletArc", {"start": v(-0.46, -1.2) * mm, "mid": v(-0.66, -1.25) * mm, "end": v(-0.8, -1.4) * mm});
            skArc(sketch, "E1257.filletArc", {"start": v(0.8, -1.4) * mm, "mid": v(0.66, -1.25) * mm, "end": v(0.46, -1.2) * mm});
            skArc(sketch, "E1258.filletArc", {"start": v(1.27, -2.6) * mm, "mid": v(1.32, -2.4) * mm, "end": v(1.27, -2.2) * mm});
            skArc(sketch, "E1259.filletArc", {"start": v(0.46, -3.6) * mm, "mid": v(0.66, -3.55) * mm, "end": v(0.8, -3.4) * mm});
            skArc(sketch, "E1260.filletArc", {"start": v(-0.8, -3.4) * mm, "mid": v(-0.66, -3.55) * mm, "end": v(-0.46, -3.6) * mm});
            skArc(sketch, "E1261.filletArc", {"start": v(-1.27, -2.2) * mm, "mid": v(-1.32, -2.4) * mm, "end": v(-1.27, -2.6) * mm});
            skLineSegment(sketch, "E1262", {"start": v(0.8, -1) * mm, "end": v(1.27, -0.2) * mm});
            skLineSegment(sketch, "E1263", {"start": v(1.62, 0) * mm, "end": v(2.54, 0) * mm});
            skLineSegment(sketch, "E1264", {"start": v(2.89, -0.2) * mm, "end": v(3.35, -1) * mm});
            skLineSegment(sketch, "E1265", {"start": v(3.35, -1.4) * mm, "end": v(2.89, -2.2) * mm});
            skLineSegment(sketch, "E1266", {"start": v(2.54, -2.4) * mm, "end": v(1.62, -2.4) * mm});
            skLineSegment(sketch, "E1267", {"start": v(1.27, -2.2) * mm, "end": v(0.8, -1.4) * mm});
            skArc(sketch, "E1268.filletArc", {"start": v(1.62, 0) * mm, "mid": v(1.42, -0.05) * mm, "end": v(1.27, -0.2) * mm});
            skArc(sketch, "E1269.filletArc", {"start": v(2.89, -0.2) * mm, "mid": v(2.74, -0.05) * mm, "end": v(2.54, 0) * mm});
            skArc(sketch, "E1270.filletArc", {"start": v(3.35, -1.4) * mm, "mid": v(3.4, -1.2) * mm, "end": v(3.35, -1) * mm});
            skArc(sketch, "E1271.filletArc", {"start": v(2.54, -2.4) * mm, "mid": v(2.74, -2.35) * mm, "end": v(2.89, -2.2) * mm});
            skArc(sketch, "E1272.filletArc", {"start": v(1.27, -2.2) * mm, "mid": v(1.42, -2.35) * mm, "end": v(1.62, -2.4) * mm});
            skArc(sketch, "E1273.filletArc", {"start": v(0.8, -1) * mm, "mid": v(0.75, -1.2) * mm, "end": v(0.8, -1.4) * mm});
            skLineSegment(sketch, "E1274", {"start": v(-3.35, 3.8) * mm, "end": v(-2.89, 4.6) * mm});
            skLineSegment(sketch, "E1275", {"start": v(-2.54, 4.8) * mm, "end": v(-1.62, 4.8) * mm});
            skLineSegment(sketch, "E1276", {"start": v(-1.27, 4.6) * mm, "end": v(-0.8, 3.8) * mm});
            skLineSegment(sketch, "E1277", {"start": v(-0.8, 3.4) * mm, "end": v(-1.27, 2.6) * mm});
            skLineSegment(sketch, "E1278", {"start": v(-1.62, 2.4) * mm, "end": v(-2.54, 2.4) * mm});
            skLineSegment(sketch, "E1279", {"start": v(-2.89, 2.6) * mm, "end": v(-3.35, 3.4) * mm});
            skArc(sketch, "E1280.filletArc", {"start": v(-2.54, 4.8) * mm, "mid": v(-2.74, 4.75) * mm, "end": v(-2.89, 4.6) * mm});
            skArc(sketch, "E1281.filletArc", {"start": v(-1.27, 4.6) * mm, "mid": v(-1.42, 4.75) * mm, "end": v(-1.62, 4.8) * mm});
            skArc(sketch, "E1282.filletArc", {"start": v(-0.8, 3.4) * mm, "mid": v(-0.75, 3.6) * mm, "end": v(-0.8, 3.8) * mm});
            skArc(sketch, "E1283.filletArc", {"start": v(-1.62, 2.4) * mm, "mid": v(-1.42, 2.45) * mm, "end": v(-1.27, 2.6) * mm});
            skArc(sketch, "E1284.filletArc", {"start": v(-2.89, 2.6) * mm, "mid": v(-2.74, 2.45) * mm, "end": v(-2.54, 2.4) * mm});
            skArc(sketch, "E1285.filletArc", {"start": v(-3.35, 3.8) * mm, "mid": v(-3.4, 3.6) * mm, "end": v(-3.35, 3.4) * mm});
            skLineSegment(sketch, "E1286", {"start": v(-1.27, 5) * mm, "end": v(-0.8, 5.8) * mm});
            skLineSegment(sketch, "E1287", {"start": v(-0.46, 6) * mm, "end": v(0.46, 6) * mm});
            skLineSegment(sketch, "E1288", {"start": v(0.8, 5.8) * mm, "end": v(1.27, 5) * mm});
            skLineSegment(sketch, "E1289", {"start": v(1.27, 4.6) * mm, "end": v(0.8, 3.8) * mm});
            skLineSegment(sketch, "E1290", {"start": v(0.46, 3.6) * mm, "end": v(-0.46, 3.6) * mm});
            skLineSegment(sketch, "E1291", {"start": v(-0.8, 3.8) * mm, "end": v(-1.27, 4.6) * mm});
            skArc(sketch, "E1292.filletArc", {"start": v(-0.46, 6) * mm, "mid": v(-0.66, 5.95) * mm, "end": v(-0.8, 5.8) * mm});
            skArc(sketch, "E1293.filletArc", {"start": v(0.8, 5.8) * mm, "mid": v(0.66, 5.95) * mm, "end": v(0.46, 6) * mm});
            skArc(sketch, "E1294.filletArc", {"start": v(1.27, 4.6) * mm, "mid": v(1.32, 4.8) * mm, "end": v(1.27, 5) * mm});
            skArc(sketch, "E1295.filletArc", {"start": v(0.46, 3.6) * mm, "mid": v(0.66, 3.65) * mm, "end": v(0.8, 3.8) * mm});
            skArc(sketch, "E1296.filletArc", {"start": v(-0.8, 3.8) * mm, "mid": v(-0.66, 3.65) * mm, "end": v(-0.46, 3.6) * mm});
            skArc(sketch, "E1297.filletArc", {"start": v(-1.27, 5) * mm, "mid": v(-1.32, 4.8) * mm, "end": v(-1.27, 4.6) * mm});
            skLineSegment(sketch, "E1298", {"start": v(0.8, 3.8) * mm, "end": v(1.27, 4.6) * mm});
            skLineSegment(sketch, "E1299", {"start": v(1.62, 4.8) * mm, "end": v(2.54, 4.8) * mm});
            skLineSegment(sketch, "E1300", {"start": v(2.89, 4.6) * mm, "end": v(3.35, 3.8) * mm});
            skLineSegment(sketch, "E1301", {"start": v(3.35, 3.4) * mm, "end": v(2.89, 2.6) * mm});
            skLineSegment(sketch, "E1302", {"start": v(2.54, 2.4) * mm, "end": v(1.62, 2.4) * mm});
            skLineSegment(sketch, "E1303", {"start": v(1.27, 2.6) * mm, "end": v(0.8, 3.4) * mm});
            skArc(sketch, "E1304.filletArc", {"start": v(1.62, 4.8) * mm, "mid": v(1.42, 4.75) * mm, "end": v(1.27, 4.6) * mm});
            skArc(sketch, "E1305.filletArc", {"start": v(2.89, 4.6) * mm, "mid": v(2.74, 4.75) * mm, "end": v(2.54, 4.8) * mm});
            skArc(sketch, "E1306.filletArc", {"start": v(3.35, 3.4) * mm, "mid": v(3.4, 3.6) * mm, "end": v(3.35, 3.8) * mm});
            skArc(sketch, "E1307.filletArc", {"start": v(2.54, 2.4) * mm, "mid": v(2.74, 2.45) * mm, "end": v(2.89, 2.6) * mm});
            skArc(sketch, "E1308.filletArc", {"start": v(1.27, 2.6) * mm, "mid": v(1.42, 2.45) * mm, "end": v(1.62, 2.4) * mm});
            skArc(sketch, "E1309.filletArc", {"start": v(0.8, 3.8) * mm, "mid": v(0.75, 3.6) * mm, "end": v(0.8, 3.4) * mm});
            skLineSegment(sketch, "E1310", {"start": v(2.89, 2.6) * mm, "end": v(3.35, 3.4) * mm});
            skLineSegment(sketch, "E1311", {"start": v(3.7, 3.6) * mm, "end": v(4.62, 3.6) * mm});
            skLineSegment(sketch, "E1312", {"start": v(4.97, 3.4) * mm, "end": v(5.43, 2.6) * mm});
            skLineSegment(sketch, "E1313", {"start": v(5.43, 2.2) * mm, "end": v(4.97, 1.4) * mm});
            skLineSegment(sketch, "E1314", {"start": v(4.62, 1.2) * mm, "end": v(3.7, 1.2) * mm});
            skLineSegment(sketch, "E1315", {"start": v(3.35, 1.4) * mm, "end": v(2.89, 2.2) * mm});
            skArc(sketch, "E1316.filletArc", {"start": v(3.7, 3.6) * mm, "mid": v(3.5, 3.55) * mm, "end": v(3.35, 3.4) * mm});
            skArc(sketch, "E1317.filletArc", {"start": v(4.97, 3.4) * mm, "mid": v(4.82, 3.55) * mm, "end": v(4.62, 3.6) * mm});
            skArc(sketch, "E1318.filletArc", {"start": v(5.43, 2.2) * mm, "mid": v(5.48, 2.4) * mm, "end": v(5.43, 2.6) * mm});
            skArc(sketch, "E1319.filletArc", {"start": v(4.62, 1.2) * mm, "mid": v(4.82, 1.25) * mm, "end": v(4.97, 1.4) * mm});
            skArc(sketch, "E1320.filletArc", {"start": v(3.35, 1.4) * mm, "mid": v(3.5, 1.25) * mm, "end": v(3.7, 1.2) * mm});
            skArc(sketch, "E1321.filletArc", {"start": v(2.89, 2.6) * mm, "mid": v(2.83, 2.4) * mm, "end": v(2.89, 2.2) * mm});
            skLineSegment(sketch, "E1322", {"start": v(2.89, 0.2) * mm, "end": v(3.35, 1) * mm});
            skLineSegment(sketch, "E1323", {"start": v(3.7, 1.2) * mm, "end": v(4.62, 1.2) * mm});
            skLineSegment(sketch, "E1324", {"start": v(4.97, 1) * mm, "end": v(5.43, 0.2) * mm});
            skLineSegment(sketch, "E1325", {"start": v(5.43, -0.2) * mm, "end": v(4.97, -1) * mm});
            skLineSegment(sketch, "E1326", {"start": v(4.62, -1.2) * mm, "end": v(3.7, -1.2) * mm});
            skLineSegment(sketch, "E1327", {"start": v(3.35, -1) * mm, "end": v(2.89, -0.2) * mm});
            skArc(sketch, "E1328.filletArc", {"start": v(3.7, 1.2) * mm, "mid": v(3.5, 1.15) * mm, "end": v(3.35, 1) * mm});
            skArc(sketch, "E1329.filletArc", {"start": v(4.97, 1) * mm, "mid": v(4.82, 1.15) * mm, "end": v(4.62, 1.2) * mm});
            skArc(sketch, "E1330.filletArc", {"start": v(5.43, -0.2) * mm, "mid": v(5.48, 0) * mm, "end": v(5.43, 0.2) * mm});
            skArc(sketch, "E1331.filletArc", {"start": v(4.62, -1.2) * mm, "mid": v(4.82, -1.15) * mm, "end": v(4.97, -1) * mm});
            skArc(sketch, "E1332.filletArc", {"start": v(3.35, -1) * mm, "mid": v(3.5, -1.15) * mm, "end": v(3.7, -1.2) * mm});
            skArc(sketch, "E1333.filletArc", {"start": v(2.89, 0.2) * mm, "mid": v(2.83, 0) * mm, "end": v(2.89, -0.2) * mm});
            skLineSegment(sketch, "E1334", {"start": v(2.89, -2.2) * mm, "end": v(3.35, -1.4) * mm});
            skLineSegment(sketch, "E1335", {"start": v(3.7, -1.2) * mm, "end": v(4.62, -1.2) * mm});
            skLineSegment(sketch, "E1336", {"start": v(4.97, -1.4) * mm, "end": v(5.43, -2.2) * mm});
            skLineSegment(sketch, "E1337", {"start": v(5.43, -2.6) * mm, "end": v(4.97, -3.4) * mm});
            skLineSegment(sketch, "E1338", {"start": v(4.62, -3.6) * mm, "end": v(3.7, -3.6) * mm});
            skLineSegment(sketch, "E1339", {"start": v(3.35, -3.4) * mm, "end": v(2.89, -2.6) * mm});
            skArc(sketch, "E1340.filletArc", {"start": v(3.7, -1.2) * mm, "mid": v(3.5, -1.25) * mm, "end": v(3.35, -1.4) * mm});
            skArc(sketch, "E1341.filletArc", {"start": v(4.97, -1.4) * mm, "mid": v(4.82, -1.25) * mm, "end": v(4.62, -1.2) * mm});
            skArc(sketch, "E1342.filletArc", {"start": v(5.43, -2.6) * mm, "mid": v(5.48, -2.4) * mm, "end": v(5.43, -2.2) * mm});
            skArc(sketch, "E1343.filletArc", {"start": v(4.62, -3.6) * mm, "mid": v(4.82, -3.55) * mm, "end": v(4.97, -3.4) * mm});
            skArc(sketch, "E1344.filletArc", {"start": v(3.35, -3.4) * mm, "mid": v(3.5, -3.55) * mm, "end": v(3.7, -3.6) * mm});
            skArc(sketch, "E1345.filletArc", {"start": v(2.89, -2.2) * mm, "mid": v(2.83, -2.4) * mm, "end": v(2.89, -2.6) * mm});
            skLineSegment(sketch, "E1346", {"start": v(0.8, -3.4) * mm, "end": v(1.27, -2.6) * mm});
            skLineSegment(sketch, "E1347", {"start": v(1.62, -2.4) * mm, "end": v(2.54, -2.4) * mm});
            skLineSegment(sketch, "E1348", {"start": v(2.89, -2.6) * mm, "end": v(3.35, -3.4) * mm});
            skLineSegment(sketch, "E1349", {"start": v(3.35, -3.8) * mm, "end": v(2.89, -4.6) * mm});
            skLineSegment(sketch, "E1350", {"start": v(2.54, -4.8) * mm, "end": v(1.62, -4.8) * mm});
            skLineSegment(sketch, "E1351", {"start": v(1.27, -4.6) * mm, "end": v(0.8, -3.8) * mm});
            skArc(sketch, "E1352.filletArc", {"start": v(1.62, -2.4) * mm, "mid": v(1.42, -2.45) * mm, "end": v(1.27, -2.6) * mm});
            skArc(sketch, "E1353.filletArc", {"start": v(2.89, -2.6) * mm, "mid": v(2.74, -2.45) * mm, "end": v(2.54, -2.4) * mm});
            skArc(sketch, "E1354.filletArc", {"start": v(3.35, -3.8) * mm, "mid": v(3.4, -3.6) * mm, "end": v(3.35, -3.4) * mm});
            skArc(sketch, "E1355.filletArc", {"start": v(2.54, -4.8) * mm, "mid": v(2.74, -4.75) * mm, "end": v(2.89, -4.6) * mm});
            skArc(sketch, "E1356.filletArc", {"start": v(1.27, -4.6) * mm, "mid": v(1.42, -4.75) * mm, "end": v(1.62, -4.8) * mm});
            skArc(sketch, "E1357.filletArc", {"start": v(0.8, -3.4) * mm, "mid": v(0.75, -3.6) * mm, "end": v(0.8, -3.8) * mm});
            skLineSegment(sketch, "E1358", {"start": v(-1.27, -4.6) * mm, "end": v(-0.8, -3.8) * mm});
            skLineSegment(sketch, "E1359", {"start": v(-0.46, -3.6) * mm, "end": v(0.46, -3.6) * mm});
            skLineSegment(sketch, "E1360", {"start": v(0.8, -3.8) * mm, "end": v(1.27, -4.6) * mm});
            skLineSegment(sketch, "E1361", {"start": v(1.27, -5) * mm, "end": v(0.8, -5.8) * mm});
            skLineSegment(sketch, "E1362", {"start": v(0.46, -6) * mm, "end": v(-0.46, -6) * mm});
            skLineSegment(sketch, "E1363", {"start": v(-0.8, -5.8) * mm, "end": v(-1.27, -5) * mm});
            skArc(sketch, "E1364.filletArc", {"start": v(-0.46, -3.6) * mm, "mid": v(-0.66, -3.65) * mm, "end": v(-0.8, -3.8) * mm});
            skArc(sketch, "E1365.filletArc", {"start": v(0.8, -3.8) * mm, "mid": v(0.66, -3.65) * mm, "end": v(0.46, -3.6) * mm});
            skArc(sketch, "E1366.filletArc", {"start": v(1.27, -5) * mm, "mid": v(1.32, -4.8) * mm, "end": v(1.27, -4.6) * mm});
            skArc(sketch, "E1367.filletArc", {"start": v(0.46, -6) * mm, "mid": v(0.66, -5.95) * mm, "end": v(0.8, -5.8) * mm});
            skArc(sketch, "E1368.filletArc", {"start": v(-0.8, -5.8) * mm, "mid": v(-0.66, -5.95) * mm, "end": v(-0.46, -6) * mm});
            skArc(sketch, "E1369.filletArc", {"start": v(-1.27, -4.6) * mm, "mid": v(-1.32, -4.8) * mm, "end": v(-1.27, -5) * mm});
            skLineSegment(sketch, "E1370", {"start": v(-3.35, -3.4) * mm, "end": v(-2.89, -2.6) * mm});
            skLineSegment(sketch, "E1371", {"start": v(-2.54, -2.4) * mm, "end": v(-1.62, -2.4) * mm});
            skLineSegment(sketch, "E1372", {"start": v(-1.27, -2.6) * mm, "end": v(-0.8, -3.4) * mm});
            skLineSegment(sketch, "E1373", {"start": v(-0.8, -3.8) * mm, "end": v(-1.27, -4.6) * mm});
            skLineSegment(sketch, "E1374", {"start": v(-1.62, -4.8) * mm, "end": v(-2.54, -4.8) * mm});
            skLineSegment(sketch, "E1375", {"start": v(-2.89, -4.6) * mm, "end": v(-3.35, -3.8) * mm});
            skArc(sketch, "E1376.filletArc", {"start": v(-2.54, -2.4) * mm, "mid": v(-2.74, -2.45) * mm, "end": v(-2.89, -2.6) * mm});
            skArc(sketch, "E1377.filletArc", {"start": v(-1.27, -2.6) * mm, "mid": v(-1.42, -2.45) * mm, "end": v(-1.62, -2.4) * mm});
            skArc(sketch, "E1378.filletArc", {"start": v(-0.8, -3.8) * mm, "mid": v(-0.75, -3.6) * mm, "end": v(-0.8, -3.4) * mm});
            skArc(sketch, "E1379.filletArc", {"start": v(-1.62, -4.8) * mm, "mid": v(-1.42, -4.75) * mm, "end": v(-1.27, -4.6) * mm});
            skArc(sketch, "E1380.filletArc", {"start": v(-2.89, -4.6) * mm, "mid": v(-2.74, -4.75) * mm, "end": v(-2.54, -4.8) * mm});
            skArc(sketch, "E1381.filletArc", {"start": v(-3.35, -3.4) * mm, "mid": v(-3.4, -3.6) * mm, "end": v(-3.35, -3.8) * mm});
            skLineSegment(sketch, "E1382", {"start": v(-5.43, -2.2) * mm, "end": v(-4.97, -1.4) * mm});
            skLineSegment(sketch, "E1383", {"start": v(-4.62, -1.2) * mm, "end": v(-3.7, -1.2) * mm});
            skLineSegment(sketch, "E1384", {"start": v(-3.35, -1.4) * mm, "end": v(-2.89, -2.2) * mm});
            skLineSegment(sketch, "E1385", {"start": v(-2.89, -2.6) * mm, "end": v(-3.35, -3.4) * mm});
            skLineSegment(sketch, "E1386", {"start": v(-3.7, -3.6) * mm, "end": v(-4.62, -3.6) * mm});
            skLineSegment(sketch, "E1387", {"start": v(-4.97, -3.4) * mm, "end": v(-5.43, -2.6) * mm});
            skArc(sketch, "E1388.filletArc", {"start": v(-4.62, -1.2) * mm, "mid": v(-4.82, -1.25) * mm, "end": v(-4.97, -1.4) * mm});
            skArc(sketch, "E1389.filletArc", {"start": v(-3.35, -1.4) * mm, "mid": v(-3.5, -1.25) * mm, "end": v(-3.7, -1.2) * mm});
            skArc(sketch, "E1390.filletArc", {"start": v(-2.89, -2.6) * mm, "mid": v(-2.83, -2.4) * mm, "end": v(-2.89, -2.2) * mm});
            skArc(sketch, "E1391.filletArc", {"start": v(-3.7, -3.6) * mm, "mid": v(-3.5, -3.55) * mm, "end": v(-3.35, -3.4) * mm});
            skArc(sketch, "E1392.filletArc", {"start": v(-4.97, -3.4) * mm, "mid": v(-4.82, -3.55) * mm, "end": v(-4.62, -3.6) * mm});
            skArc(sketch, "E1393.filletArc", {"start": v(-5.43, -2.2) * mm, "mid": v(-5.48, -2.4) * mm, "end": v(-5.43, -2.6) * mm});
            skLineSegment(sketch, "E1394", {"start": v(-5.43, 0.2) * mm, "end": v(-4.97, 1) * mm});
            skLineSegment(sketch, "E1395", {"start": v(-4.62, 1.2) * mm, "end": v(-3.7, 1.2) * mm});
            skLineSegment(sketch, "E1396", {"start": v(-3.35, 1) * mm, "end": v(-2.89, 0.2) * mm});
            skLineSegment(sketch, "E1397", {"start": v(-2.89, -0.2) * mm, "end": v(-3.35, -1) * mm});
            skLineSegment(sketch, "E1398", {"start": v(-3.7, -1.2) * mm, "end": v(-4.62, -1.2) * mm});
            skLineSegment(sketch, "E1399", {"start": v(-4.97, -1) * mm, "end": v(-5.43, -0.2) * mm});
            skArc(sketch, "E1400.filletArc", {"start": v(-4.62, 1.2) * mm, "mid": v(-4.82, 1.15) * mm, "end": v(-4.97, 1) * mm});
            skArc(sketch, "E1401.filletArc", {"start": v(-3.35, 1) * mm, "mid": v(-3.5, 1.15) * mm, "end": v(-3.7, 1.2) * mm});
            skArc(sketch, "E1402.filletArc", {"start": v(-2.89, -0.2) * mm, "mid": v(-2.83, 0) * mm, "end": v(-2.89, 0.2) * mm});
            skArc(sketch, "E1403.filletArc", {"start": v(-3.7, -1.2) * mm, "mid": v(-3.5, -1.15) * mm, "end": v(-3.35, -1) * mm});
            skArc(sketch, "E1404.filletArc", {"start": v(-4.97, -1) * mm, "mid": v(-4.82, -1.15) * mm, "end": v(-4.62, -1.2) * mm});
            skArc(sketch, "E1405.filletArc", {"start": v(-5.43, 0.2) * mm, "mid": v(-5.48, 0) * mm, "end": v(-5.43, -0.2) * mm});
            skLineSegment(sketch, "E1406", {"start": v(-5.43, 2.6) * mm, "end": v(-4.97, 3.4) * mm});
            skLineSegment(sketch, "E1407", {"start": v(-4.62, 3.6) * mm, "end": v(-3.7, 3.6) * mm});
            skLineSegment(sketch, "E1408", {"start": v(-3.35, 3.4) * mm, "end": v(-2.89, 2.6) * mm});
            skLineSegment(sketch, "E1409", {"start": v(-2.89, 2.2) * mm, "end": v(-3.35, 1.4) * mm});
            skLineSegment(sketch, "E1410", {"start": v(-3.7, 1.2) * mm, "end": v(-4.62, 1.2) * mm});
            skLineSegment(sketch, "E1411", {"start": v(-4.97, 1.4) * mm, "end": v(-5.43, 2.2) * mm});
            skArc(sketch, "E1412.filletArc", {"start": v(-4.62, 3.6) * mm, "mid": v(-4.82, 3.55) * mm, "end": v(-4.97, 3.4) * mm});
            skArc(sketch, "E1413.filletArc", {"start": v(-3.35, 3.4) * mm, "mid": v(-3.5, 3.55) * mm, "end": v(-3.7, 3.6) * mm});
            skArc(sketch, "E1414.filletArc", {"start": v(-2.89, 2.2) * mm, "mid": v(-2.83, 2.4) * mm, "end": v(-2.89, 2.6) * mm});
            skArc(sketch, "E1415.filletArc", {"start": v(-3.7, 1.2) * mm, "mid": v(-3.5, 1.25) * mm, "end": v(-3.35, 1.4) * mm});
            skArc(sketch, "E1416.filletArc", {"start": v(-4.97, 1.4) * mm, "mid": v(-4.82, 1.25) * mm, "end": v(-4.62, 1.2) * mm});
            skArc(sketch, "E1417.filletArc", {"start": v(-5.43, 2.6) * mm, "mid": v(-5.48, 2.4) * mm, "end": v(-5.43, 2.2) * mm});
            skLineSegment(sketch, "E1418", {"start": v(-5.43, 5) * mm, "end": v(-4.97, 5.8) * mm});
            skLineSegment(sketch, "E1419", {"start": v(-4.62, 6) * mm, "end": v(-3.7, 6) * mm});
            skLineSegment(sketch, "E1420", {"start": v(-3.35, 5.8) * mm, "end": v(-2.89, 5) * mm});
            skLineSegment(sketch, "E1421", {"start": v(-2.89, 4.6) * mm, "end": v(-3.35, 3.8) * mm});
            skLineSegment(sketch, "E1422", {"start": v(-3.7, 3.6) * mm, "end": v(-4.62, 3.6) * mm});
            skLineSegment(sketch, "E1423", {"start": v(-4.97, 3.8) * mm, "end": v(-5.43, 4.6) * mm});
            skArc(sketch, "E1424.filletArc", {"start": v(-4.62, 6) * mm, "mid": v(-4.82, 5.95) * mm, "end": v(-4.97, 5.8) * mm});
            skArc(sketch, "E1425.filletArc", {"start": v(-3.35, 5.8) * mm, "mid": v(-3.5, 5.95) * mm, "end": v(-3.7, 6) * mm});
            skArc(sketch, "E1426.filletArc", {"start": v(-2.89, 4.6) * mm, "mid": v(-2.83, 4.8) * mm, "end": v(-2.89, 5) * mm});
            skArc(sketch, "E1427.filletArc", {"start": v(-3.7, 3.6) * mm, "mid": v(-3.5, 3.65) * mm, "end": v(-3.35, 3.8) * mm});
            skArc(sketch, "E1428.filletArc", {"start": v(-4.97, 3.8) * mm, "mid": v(-4.82, 3.65) * mm, "end": v(-4.62, 3.6) * mm});
            skArc(sketch, "E1429.filletArc", {"start": v(-5.43, 5) * mm, "mid": v(-5.48, 4.8) * mm, "end": v(-5.43, 4.6) * mm});
            skLineSegment(sketch, "E1430", {"start": v(-3.35, 6.2) * mm, "end": v(-2.89, 7) * mm});
            skLineSegment(sketch, "E1431", {"start": v(-2.54, 7.2) * mm, "end": v(-1.62, 7.2) * mm});
            skLineSegment(sketch, "E1432", {"start": v(-1.27, 7) * mm, "end": v(-0.8, 6.2) * mm});
            skLineSegment(sketch, "E1433", {"start": v(-0.8, 5.8) * mm, "end": v(-1.27, 5) * mm});
            skLineSegment(sketch, "E1434", {"start": v(-1.62, 4.8) * mm, "end": v(-2.54, 4.8) * mm});
            skLineSegment(sketch, "E1435", {"start": v(-2.89, 5) * mm, "end": v(-3.35, 5.8) * mm});
            skArc(sketch, "E1436.filletArc", {"start": v(-2.54, 7.2) * mm, "mid": v(-2.74, 7.15) * mm, "end": v(-2.89, 7) * mm});
            skArc(sketch, "E1437.filletArc", {"start": v(-1.27, 7) * mm, "mid": v(-1.42, 7.15) * mm, "end": v(-1.62, 7.2) * mm});
            skArc(sketch, "E1438.filletArc", {"start": v(-0.8, 5.8) * mm, "mid": v(-0.75, 6) * mm, "end": v(-0.8, 6.2) * mm});
            skArc(sketch, "E1439.filletArc", {"start": v(-1.62, 4.8) * mm, "mid": v(-1.42, 4.85) * mm, "end": v(-1.27, 5) * mm});
            skArc(sketch, "E1440.filletArc", {"start": v(-2.89, 5) * mm, "mid": v(-2.74, 4.85) * mm, "end": v(-2.54, 4.8) * mm});
            skArc(sketch, "E1441.filletArc", {"start": v(-3.35, 6.2) * mm, "mid": v(-3.4, 6) * mm, "end": v(-3.35, 5.8) * mm});
            skLineSegment(sketch, "E1442", {"start": v(-1.27, 7.4) * mm, "end": v(-0.8, 8.2) * mm});
            skLineSegment(sketch, "E1443", {"start": v(-0.46, 8.4) * mm, "end": v(0.46, 8.4) * mm});
            skLineSegment(sketch, "E1444", {"start": v(0.8, 8.2) * mm, "end": v(1.27, 7.4) * mm});
            skLineSegment(sketch, "E1445", {"start": v(1.27, 7) * mm, "end": v(0.8, 6.2) * mm});
            skLineSegment(sketch, "E1446", {"start": v(0.46, 6) * mm, "end": v(-0.46, 6) * mm});
            skLineSegment(sketch, "E1447", {"start": v(-0.8, 6.2) * mm, "end": v(-1.27, 7) * mm});
            skArc(sketch, "E1448.filletArc", {"start": v(-0.46, 8.4) * mm, "mid": v(-0.66, 8.35) * mm, "end": v(-0.8, 8.2) * mm});
            skArc(sketch, "E1449.filletArc", {"start": v(0.8, 8.2) * mm, "mid": v(0.66, 8.35) * mm, "end": v(0.46, 8.4) * mm});
            skArc(sketch, "E1450.filletArc", {"start": v(1.27, 7) * mm, "mid": v(1.32, 7.2) * mm, "end": v(1.27, 7.4) * mm});
            skArc(sketch, "E1451.filletArc", {"start": v(0.46, 6) * mm, "mid": v(0.66, 6.05) * mm, "end": v(0.8, 6.2) * mm});
            skArc(sketch, "E1452.filletArc", {"start": v(-0.8, 6.2) * mm, "mid": v(-0.66, 6.05) * mm, "end": v(-0.46, 6) * mm});
            skArc(sketch, "E1453.filletArc", {"start": v(-1.27, 7.4) * mm, "mid": v(-1.32, 7.2) * mm, "end": v(-1.27, 7) * mm});
            skLineSegment(sketch, "E1454", {"start": v(0.8, 6.2) * mm, "end": v(1.27, 7) * mm});
            skLineSegment(sketch, "E1455", {"start": v(1.62, 7.2) * mm, "end": v(2.54, 7.2) * mm});
            skLineSegment(sketch, "E1456", {"start": v(2.89, 7) * mm, "end": v(3.35, 6.2) * mm});
            skLineSegment(sketch, "E1457", {"start": v(3.35, 5.8) * mm, "end": v(2.89, 5) * mm});
            skLineSegment(sketch, "E1458", {"start": v(2.54, 4.8) * mm, "end": v(1.62, 4.8) * mm});
            skLineSegment(sketch, "E1459", {"start": v(1.27, 5) * mm, "end": v(0.8, 5.8) * mm});
            skArc(sketch, "E1460.filletArc", {"start": v(1.62, 7.2) * mm, "mid": v(1.42, 7.15) * mm, "end": v(1.27, 7) * mm});
            skArc(sketch, "E1461.filletArc", {"start": v(2.89, 7) * mm, "mid": v(2.74, 7.15) * mm, "end": v(2.54, 7.2) * mm});
            skArc(sketch, "E1462.filletArc", {"start": v(3.35, 5.8) * mm, "mid": v(3.4, 6) * mm, "end": v(3.35, 6.2) * mm});
            skArc(sketch, "E1463.filletArc", {"start": v(2.54, 4.8) * mm, "mid": v(2.74, 4.85) * mm, "end": v(2.89, 5) * mm});
            skArc(sketch, "E1464.filletArc", {"start": v(1.27, 5) * mm, "mid": v(1.42, 4.85) * mm, "end": v(1.62, 4.8) * mm});
            skArc(sketch, "E1465.filletArc", {"start": v(0.8, 6.2) * mm, "mid": v(0.75, 6) * mm, "end": v(0.8, 5.8) * mm});
            skLineSegment(sketch, "E1466", {"start": v(2.89, 5) * mm, "end": v(3.35, 5.8) * mm});
            skLineSegment(sketch, "E1467", {"start": v(3.7, 6) * mm, "end": v(4.62, 6) * mm});
            skLineSegment(sketch, "E1468", {"start": v(4.97, 5.8) * mm, "end": v(5.43, 5) * mm});
            skLineSegment(sketch, "E1469", {"start": v(5.43, 4.6) * mm, "end": v(4.97, 3.8) * mm});
            skLineSegment(sketch, "E1470", {"start": v(4.62, 3.6) * mm, "end": v(3.7, 3.6) * mm});
            skLineSegment(sketch, "E1471", {"start": v(3.35, 3.8) * mm, "end": v(2.89, 4.6) * mm});
            skArc(sketch, "E1472.filletArc", {"start": v(3.7, 6) * mm, "mid": v(3.5, 5.95) * mm, "end": v(3.35, 5.8) * mm});
            skArc(sketch, "E1473.filletArc", {"start": v(4.97, 5.8) * mm, "mid": v(4.82, 5.95) * mm, "end": v(4.62, 6) * mm});
            skArc(sketch, "E1474.filletArc", {"start": v(5.43, 4.6) * mm, "mid": v(5.48, 4.8) * mm, "end": v(5.43, 5) * mm});
            skArc(sketch, "E1475.filletArc", {"start": v(4.62, 3.6) * mm, "mid": v(4.82, 3.65) * mm, "end": v(4.97, 3.8) * mm});
            skArc(sketch, "E1476.filletArc", {"start": v(3.35, 3.8) * mm, "mid": v(3.5, 3.65) * mm, "end": v(3.7, 3.6) * mm});
            skArc(sketch, "E1477.filletArc", {"start": v(2.89, 5) * mm, "mid": v(2.83, 4.8) * mm, "end": v(2.89, 4.6) * mm});
            skLineSegment(sketch, "E1478", {"start": v(2.89, -4.6) * mm, "end": v(3.35, -3.8) * mm});
            skLineSegment(sketch, "E1479", {"start": v(3.7, -3.6) * mm, "end": v(4.62, -3.6) * mm});
            skLineSegment(sketch, "E1480", {"start": v(4.97, -3.8) * mm, "end": v(5.43, -4.6) * mm});
            skLineSegment(sketch, "E1481", {"start": v(5.43, -5) * mm, "end": v(4.97, -5.8) * mm});
            skLineSegment(sketch, "E1482", {"start": v(4.62, -6) * mm, "end": v(3.7, -6) * mm});
            skLineSegment(sketch, "E1483", {"start": v(3.35, -5.8) * mm, "end": v(2.89, -5) * mm});
            skArc(sketch, "E1484.filletArc", {"start": v(3.7, -3.6) * mm, "mid": v(3.5, -3.65) * mm, "end": v(3.35, -3.8) * mm});
            skArc(sketch, "E1485.filletArc", {"start": v(4.97, -3.8) * mm, "mid": v(4.82, -3.65) * mm, "end": v(4.62, -3.6) * mm});
            skArc(sketch, "E1486.filletArc", {"start": v(5.43, -5) * mm, "mid": v(5.48, -4.8) * mm, "end": v(5.43, -4.6) * mm});
            skArc(sketch, "E1487.filletArc", {"start": v(4.62, -6) * mm, "mid": v(4.82, -5.95) * mm, "end": v(4.97, -5.8) * mm});
            skArc(sketch, "E1488.filletArc", {"start": v(3.35, -5.8) * mm, "mid": v(3.5, -5.95) * mm, "end": v(3.7, -6) * mm});
            skArc(sketch, "E1489.filletArc", {"start": v(2.89, -4.6) * mm, "mid": v(2.83, -4.8) * mm, "end": v(2.89, -5) * mm});
            skLineSegment(sketch, "E1490", {"start": v(0.8, -5.8) * mm, "end": v(1.27, -5) * mm});
            skLineSegment(sketch, "E1491", {"start": v(1.62, -4.8) * mm, "end": v(2.54, -4.8) * mm});
            skLineSegment(sketch, "E1492", {"start": v(2.89, -5) * mm, "end": v(3.35, -5.8) * mm});
            skLineSegment(sketch, "E1493", {"start": v(3.35, -6.2) * mm, "end": v(2.89, -7) * mm});
            skLineSegment(sketch, "E1494", {"start": v(2.54, -7.2) * mm, "end": v(1.62, -7.2) * mm});
            skLineSegment(sketch, "E1495", {"start": v(1.27, -7) * mm, "end": v(0.8, -6.2) * mm});
            skArc(sketch, "E1496.filletArc", {"start": v(1.62, -4.8) * mm, "mid": v(1.42, -4.85) * mm, "end": v(1.27, -5) * mm});
            skArc(sketch, "E1497.filletArc", {"start": v(2.89, -5) * mm, "mid": v(2.74, -4.85) * mm, "end": v(2.54, -4.8) * mm});
            skArc(sketch, "E1498.filletArc", {"start": v(3.35, -6.2) * mm, "mid": v(3.4, -6) * mm, "end": v(3.35, -5.8) * mm});
            skArc(sketch, "E1499.filletArc", {"start": v(2.54, -7.2) * mm, "mid": v(2.74, -7.15) * mm, "end": v(2.89, -7) * mm});
            skArc(sketch, "E1500.filletArc", {"start": v(1.27, -7) * mm, "mid": v(1.42, -7.15) * mm, "end": v(1.62, -7.2) * mm});
            skArc(sketch, "E1501.filletArc", {"start": v(0.8, -5.8) * mm, "mid": v(0.75, -6) * mm, "end": v(0.8, -6.2) * mm});
            skLineSegment(sketch, "E1502", {"start": v(-1.27, -7) * mm, "end": v(-0.8, -6.2) * mm});
            skLineSegment(sketch, "E1503", {"start": v(-0.46, -6) * mm, "end": v(0.46, -6) * mm});
            skLineSegment(sketch, "E1504", {"start": v(0.8, -6.2) * mm, "end": v(1.27, -7) * mm});
            skLineSegment(sketch, "E1505", {"start": v(1.27, -7.4) * mm, "end": v(0.8, -8.2) * mm});
            skLineSegment(sketch, "E1506", {"start": v(0.46, -8.4) * mm, "end": v(-0.46, -8.4) * mm});
            skLineSegment(sketch, "E1507", {"start": v(-0.8, -8.2) * mm, "end": v(-1.27, -7.4) * mm});
            skArc(sketch, "E1508.filletArc", {"start": v(-0.46, -6) * mm, "mid": v(-0.66, -6.05) * mm, "end": v(-0.8, -6.2) * mm});
            skArc(sketch, "E1509.filletArc", {"start": v(0.8, -6.2) * mm, "mid": v(0.66, -6.05) * mm, "end": v(0.46, -6) * mm});
            skArc(sketch, "E1510.filletArc", {"start": v(1.27, -7.4) * mm, "mid": v(1.32, -7.2) * mm, "end": v(1.27, -7) * mm});
            skArc(sketch, "E1511.filletArc", {"start": v(0.46, -8.4) * mm, "mid": v(0.66, -8.35) * mm, "end": v(0.8, -8.2) * mm});
            skArc(sketch, "E1512.filletArc", {"start": v(-0.8, -8.2) * mm, "mid": v(-0.66, -8.35) * mm, "end": v(-0.46, -8.4) * mm});
            skArc(sketch, "E1513.filletArc", {"start": v(-1.27, -7) * mm, "mid": v(-1.32, -7.2) * mm, "end": v(-1.27, -7.4) * mm});
            skLineSegment(sketch, "E1514", {"start": v(-3.35, -5.8) * mm, "end": v(-2.89, -5) * mm});
            skLineSegment(sketch, "E1515", {"start": v(-2.54, -4.8) * mm, "end": v(-1.62, -4.8) * mm});
            skLineSegment(sketch, "E1516", {"start": v(-1.27, -5) * mm, "end": v(-0.8, -5.8) * mm});
            skLineSegment(sketch, "E1517", {"start": v(-0.8, -6.2) * mm, "end": v(-1.27, -7) * mm});
            skLineSegment(sketch, "E1518", {"start": v(-1.62, -7.2) * mm, "end": v(-2.54, -7.2) * mm});
            skLineSegment(sketch, "E1519", {"start": v(-2.89, -7) * mm, "end": v(-3.35, -6.2) * mm});
            skArc(sketch, "E1520.filletArc", {"start": v(-2.54, -4.8) * mm, "mid": v(-2.74, -4.85) * mm, "end": v(-2.89, -5) * mm});
            skArc(sketch, "E1521.filletArc", {"start": v(-1.27, -5) * mm, "mid": v(-1.42, -4.85) * mm, "end": v(-1.62, -4.8) * mm});
            skArc(sketch, "E1522.filletArc", {"start": v(-0.8, -6.2) * mm, "mid": v(-0.75, -6) * mm, "end": v(-0.8, -5.8) * mm});
            skArc(sketch, "E1523.filletArc", {"start": v(-1.62, -7.2) * mm, "mid": v(-1.42, -7.15) * mm, "end": v(-1.27, -7) * mm});
            skArc(sketch, "E1524.filletArc", {"start": v(-2.89, -7) * mm, "mid": v(-2.74, -7.15) * mm, "end": v(-2.54, -7.2) * mm});
            skArc(sketch, "E1525.filletArc", {"start": v(-3.35, -5.8) * mm, "mid": v(-3.4, -6) * mm, "end": v(-3.35, -6.2) * mm});
            skLineSegment(sketch, "E1526", {"start": v(-5.43, -4.6) * mm, "end": v(-4.97, -3.8) * mm});
            skLineSegment(sketch, "E1527", {"start": v(-4.62, -3.6) * mm, "end": v(-3.7, -3.6) * mm});
            skLineSegment(sketch, "E1528", {"start": v(-3.35, -3.8) * mm, "end": v(-2.89, -4.6) * mm});
            skLineSegment(sketch, "E1529", {"start": v(-2.89, -5) * mm, "end": v(-3.35, -5.8) * mm});
            skLineSegment(sketch, "E1530", {"start": v(-3.7, -6) * mm, "end": v(-4.62, -6) * mm});
            skLineSegment(sketch, "E1531", {"start": v(-4.97, -5.8) * mm, "end": v(-5.43, -5) * mm});
            skArc(sketch, "E1532.filletArc", {"start": v(-4.62, -3.6) * mm, "mid": v(-4.82, -3.65) * mm, "end": v(-4.97, -3.8) * mm});
            skArc(sketch, "E1533.filletArc", {"start": v(-3.35, -3.8) * mm, "mid": v(-3.5, -3.65) * mm, "end": v(-3.7, -3.6) * mm});
            skArc(sketch, "E1534.filletArc", {"start": v(-2.89, -5) * mm, "mid": v(-2.83, -4.8) * mm, "end": v(-2.89, -4.6) * mm});
            skArc(sketch, "E1535.filletArc", {"start": v(-3.7, -6) * mm, "mid": v(-3.5, -5.95) * mm, "end": v(-3.35, -5.8) * mm});
            skArc(sketch, "E1536.filletArc", {"start": v(-4.97, -5.8) * mm, "mid": v(-4.82, -5.95) * mm, "end": v(-4.62, -6) * mm});
            skArc(sketch, "E1537.filletArc", {"start": v(-5.43, -4.6) * mm, "mid": v(-5.48, -4.8) * mm, "end": v(-5.43, -5) * mm});
            skSolve(sketch);
        }
        {
            var Q0;
            Q0=qCreatedBy(id+"F4.planeOp",FACE);
            cPlane(context, id + "F6", {"entities" : qUnion([Q0]), "cplaneType" : CPlaneType.OFFSET, "offset" : 0.4 * mm, "width" : 150 * mm, "height" : 150 * mm});
        }
        {
            var Q0;
            Q0=qCreatedBy(id+"F6.planeOp",FACE);
            cPlane(context, id + "F7", {"entities" : qUnion([Q0]), "cplaneType" : CPlaneType.OFFSET, "offset" : 0.4 * mm, "width" : 150 * mm, "height" : 150 * mm});
        }
        {
            var Q0;
            Q0=sQuery(id+"F1.wireOp",EDGE,"E483");
            var Q1;
            Q1=sQuery(id+"F1.wireOp",VERTEX,"E483.end");
            cPlane(context, id + "F8", {"entities" : qUnion([Q0, Q1]), "cplaneType" : CPlaneType.LINE_POINT, "offset" : 25 * mm, "width" : 150 * mm, "height" : 150 * mm});
        }
        {
            var Q0;
            Q0=qCreatedBy(id+"F8.planeOp",FACE);
            var sketch = newSketch(context, id + "F9", { "sketchPlane" : qUnion([Q0])});
            skCircle(sketch, "E1538", {"center": v(10.8, 0.21) * mm, "radius": 0.2 * mm});
            skSolve(sketch);
        }
        {
            var Q0;
            Q0=makeQuery(id+"F9.imprint","IMPRINT",FACE,{"disambiguationData":[TD([[makeQuery(id+"F9.imprint","IMPRINT",EDGE,{"derivedFrom":sQuery(id+"F9.wireOp",EDGE,"E1538")}),1.0]])]});
            var Q1;
            Q1=sQuery(id+"F1.wireOp",EDGE,"E483");
            var Q2;
            Q2=sQuery(id+"F1.wireOp",EDGE,"E488.filletArc");
            var Q3;
            Q3=sQuery(id+"F1.wireOp",EDGE,"E482");
            var Q4;
            Q4=sQuery(id+"F1.wireOp",EDGE,"E487.filletArc");
            var Q5;
            Q5=sQuery(id+"F1.wireOp",EDGE,"E472");
            var Q6;
            Q6=sQuery(id+"F1.wireOp",EDGE,"E492.filletArc");
            var Q7;
            Q7=sQuery(id+"F1.wireOp",EDGE,"E486");
            var Q8;
            Q8=sQuery(id+"F1.wireOp",EDGE,"E491.filletArc");
            var Q9;
            Q9=sQuery(id+"F1.wireOp",EDGE,"E485");
            var Q10;
            Q10=sQuery(id+"F1.wireOp",EDGE,"E500.filletArc");
            var Q11;
            Q11=sQuery(id+"F1.wireOp",EDGE,"E495");
            var Q12;
            Q12=sQuery(id+"F1.wireOp",EDGE,"E501.filletArc");
            var Q13;
            Q13=sQuery(id+"F1.wireOp",EDGE,"E496");
            var Q14;
            Q14=sQuery(id+"F1.wireOp",EDGE,"E502.filletArc");
            var Q15;
            Q15=sQuery(id+"F1.wireOp",EDGE,"E506");
            var Q16;
            Q16=sQuery(id+"F1.wireOp",EDGE,"E511.filletArc");
            var Q17;
            Q17=sQuery(id+"F1.wireOp",EDGE,"E505");
            var Q18;
            Q18=sQuery(id+"F1.wireOp",EDGE,"E516.filletArc");
            var Q19;
            Q19=sQuery(id+"F1.wireOp",EDGE,"E411");
            var Q20;
            Q20=sQuery(id+"F1.wireOp",EDGE,"E515.filletArc");
            var Q21;
            Q21=sQuery(id+"F1.wireOp",EDGE,"E509");
            var Q22;
            Q22=sQuery(id+"F1.wireOp",EDGE,"E524.filletArc");
            var Q23;
            Q23=sQuery(id+"F1.wireOp",EDGE,"E519");
            var Q24;
            Q24=sQuery(id+"F1.wireOp",EDGE,"E525.filletArc");
            var Q25;
            Q25=sQuery(id+"F1.wireOp",EDGE,"E520");
            var Q26;
            Q26=sQuery(id+"F1.wireOp",EDGE,"E526.filletArc");
            var Q27;
            Q27=sQuery(id+"F1.wireOp",EDGE,"E521");
            var Q28;
            Q28=sQuery(id+"F1.wireOp",EDGE,"E535.filletArc");
            var Q29;
            Q29=sQuery(id+"F1.wireOp",EDGE,"E529");
            var Q30;
            Q30=sQuery(id+"F1.wireOp",EDGE,"E540.filletArc");
            var Q31;
            Q31=sQuery(id+"F1.wireOp",EDGE,"E555");
            var Q32;
            Q32=sQuery(id+"F1.wireOp",EDGE,"E561.filletArc");
            var Q33;
            Q33=sQuery(id+"F1.wireOp",EDGE,"E556");
            var Q34;
            Q34=sQuery(id+"F1.wireOp",EDGE,"E562.filletArc");
            var Q35;
            Q35=sQuery(id+"F1.wireOp",EDGE,"E557");
            var Q36;
            Q36=sQuery(id+"F1.wireOp",EDGE,"E563.filletArc");
            var Q37;
            Q37=sQuery(id+"F1.wireOp",EDGE,"E558");
            var Q38;
            Q38=sQuery(id+"F1.wireOp",EDGE,"E564.filletArc");
            var Q39;
            Q39=sQuery(id+"F1.wireOp",EDGE,"E553");
            var Q40;
            Q40=sQuery(id+"F1.wireOp",EDGE,"E393.filletArc");
            var Q41;
            Q41=sQuery(id+"F1.wireOp",EDGE,"E387");
            var Q42;
            Q42=sQuery(id+"F1.wireOp",EDGE,"E408.filletArc");
            var Q43;
            Q43=sQuery(id+"F1.wireOp",EDGE,"E397");
            var Q44;
            Q44=sQuery(id+"F1.wireOp",EDGE,"E129.filletArc");
            var Q45;
            Q45=sQuery(id+"F1.wireOp",EDGE,"E123");
            var Q46;
            Q46=sQuery(id+"F1.wireOp",EDGE,"E420.filletArc");
            var Q47;
            Q47=sQuery(id+"F1.wireOp",EDGE,"E409");
            var Q48;
            Q48=sQuery(id+"F1.wireOp",EDGE,"E117.filletArc");
            var Q49;
            Q49=sQuery(id+"F1.wireOp",EDGE,"E426");
            var Q50;
            Q50=sQuery(id+"F1.wireOp",EDGE,"E432.filletArc");
            var Q51;
            Q51=sQuery(id+"F1.wireOp",EDGE,"E88");
            var Q52;
            Q52=sQuery(id+"F1.wireOp",EDGE,"E93.filletArc");
            var Q53;
            Q53=sQuery(id+"F1.wireOp",EDGE,"E87");
            var Q54;
            Q54=sQuery(id+"F1.wireOp",EDGE,"E444.filletArc");
            var Q55;
            Q55=sQuery(id+"F1.wireOp",EDGE,"E232");
            var Q56;
            Q56=sQuery(id+"F1.wireOp",EDGE,"E237.filletArc");
            var Q57;
            Q57=sQuery(id+"F1.wireOp",EDGE,"E474");
            var Q58;
            Q58=sQuery(id+"F1.wireOp",EDGE,"E480.filletArc");
            var Q59;
            Q59=sQuery(id+"F1.wireOp",EDGE,"E460");
            var Q60;
            Q60=sQuery(id+"F1.wireOp",EDGE,"E465.filletArc");
            var Q61;
            Q61=sQuery(id+"F1.wireOp",EDGE,"E459");
            var Q62;
            Q62=sQuery(id+"F1.wireOp",EDGE,"E464.filletArc");
            var Q63;
            Q63=sQuery(id+"F1.wireOp",EDGE,"E458");
            var Q64;
            Q64=sQuery(id+"F1.wireOp",EDGE,"E463.filletArc");
            var Q65;
            Q65=sQuery(id+"F1.wireOp",EDGE,"E457");
            var Q66;
            Q66=sQuery(id+"F1.wireOp",EDGE,"E468.filletArc");
            var Q67;
            Q67=sQuery(id+"F1.wireOp",EDGE,"E243");
            var Q68;
            Q68=sQuery(id+"F1.wireOp",EDGE,"E249.filletArc");
            var Q69;
            Q69=sQuery(id+"F1.wireOp",EDGE,"E229");
            var Q70;
            Q70=sQuery(id+"F1.wireOp",EDGE,"E240.filletArc");
            var Q71;
            Q71=sQuery(id+"F1.wireOp",EDGE,"E234");
            var Q72;
            Q72=sQuery(id+"F1.wireOp",EDGE,"E105.filletArc");
            var Q73;
            Q73=sQuery(id+"F1.wireOp",EDGE,"E85");
            var Q74;
            Q74=sQuery(id+"F1.wireOp",EDGE,"E96.filletArc");
            var Q75;
            Q75=sQuery(id+"F1.wireOp",EDGE,"E90");
            var Q76;
            Q76=sQuery(id+"F1.wireOp",EDGE,"E21.filletArc");
            var Q77;
            Q77=sQuery(id+"F1.wireOp",EDGE,"E109");
            var Q78;
            Q78=sQuery(id+"F1.wireOp",EDGE,"E120.filletArc");
            var Q79;
            Q79=sQuery(id+"F1.wireOp",EDGE,"E81.filletArc");
            var Q80;
            Q80=sQuery(id+"F1.wireOp",EDGE,"E75");
            var Q81;
            Q81=sQuery(id+"F1.wireOp",EDGE,"E76");
            var Q82;
            Q82=sQuery(id+"F1.wireOp",EDGE,"E132.filletArc");
            var Q83;
            Q83=sQuery(id+"F1.wireOp",EDGE,"E135");
            var Q84;
            Q84=sQuery(id+"F1.wireOp",EDGE,"E141.filletArc");
            var Q85;
            Q85=sQuery(id+"F1.wireOp",EDGE,"E136");
            var Q86;
            Q86=sQuery(id+"F1.wireOp",EDGE,"E396.filletArc");
            var Q87;
            Q87=sQuery(id+"F1.wireOp",EDGE,"E375");
            var Q88;
            Q88=sQuery(id+"F1.wireOp",EDGE,"E381.filletArc");
            var Q89;
            Q89=sQuery(id+"F1.wireOp",EDGE,"E541");
            var Q90;
            Q90=sQuery(id+"F1.wireOp",EDGE,"E552.filletArc");
            var Q91;
            Q91=sQuery(id+"F1.wireOp",EDGE,"E567");
            var Q92;
            Q92=sQuery(id+"F1.wireOp",EDGE,"E573.filletArc");
            var Q93;
            Q93=sQuery(id+"F1.wireOp",EDGE,"E568");
            var Q94;
            Q94=sQuery(id+"F1.wireOp",EDGE,"E574.filletArc");
            var Q95;
            Q95=sQuery(id+"F1.wireOp",EDGE,"E569");
            var Q96;
            Q96=sQuery(id+"F1.wireOp",EDGE,"E575.filletArc");
            var Q97;
            Q97=sQuery(id+"F1.wireOp",EDGE,"E570");
            var Q98;
            Q98=sQuery(id+"F1.wireOp",EDGE,"E576.filletArc");
            var Q99;
            Q99=sQuery(id+"F1.wireOp",EDGE,"E364");
            var Q100;
            Q100=sQuery(id+"F1.wireOp",EDGE,"E369.filletArc");
            var Q101;
            Q101=sQuery(id+"F1.wireOp",EDGE,"E384.filletArc");
            var Q102;
            Q102=sQuery(id+"F1.wireOp",EDGE,"E373");
            var Q103;
            Q103=sQuery(id+"F1.wireOp",EDGE,"E363");
            var Q104;
            Q104=sQuery(id+"F1.wireOp",EDGE,"E153.filletArc");
            var Q105;
            Q105=sQuery(id+"F1.wireOp",EDGE,"E138");
            var Q106;
            Q106=sQuery(id+"F1.wireOp",EDGE,"E144.filletArc");
            var Q107;
            Q107=sQuery(id+"F1.wireOp",EDGE,"E133");
            var Q108;
            Q108=sQuery(id+"F1.wireOp",EDGE,"E69.filletArc");
            var Q109;
            Q109=sQuery(id+"F1.wireOp",EDGE,"E84.filletArc");
            var Q110;
            Q110=sQuery(id+"F1.wireOp",EDGE,"E73");
            var Q111;
            Q111=sQuery(id+"F1.wireOp",EDGE,"E63");
            var Q112;
            Q112=sQuery(id+"F1.wireOp",EDGE,"E9.filletArc");
            var Q113;
            Q113=sQuery(id+"F1.wireOp",EDGE,"E18");
            var Q114;
            Q114=sQuery(id+"F1.wireOp",EDGE,"E24.filletArc");
            var Q115;
            Q115=sQuery(id+"F1.wireOp",EDGE,"E28");
            var Q116;
            Q116=sQuery(id+"F1.wireOp",EDGE,"E33.filletArc");
            var Q117;
            Q117=sQuery(id+"F1.wireOp",EDGE,"E27");
            var Q118;
            Q118=sQuery(id+"F1.wireOp",EDGE,"E108.filletArc");
            var Q119;
            Q119=sQuery(id+"F1.wireOp",EDGE,"E220");
            var Q120;
            Q120=sQuery(id+"F1.wireOp",EDGE,"E225.filletArc");
            var Q121;
            Q121=sQuery(id+"F1.wireOp",EDGE,"E219");
            var Q122;
            Q122=sQuery(id+"F1.wireOp",EDGE,"E252.filletArc");
            var Q123;
            Q123=sQuery(id+"F1.wireOp",EDGE,"E241");
            var Q124;
            Q124=sQuery(id+"F1.wireOp",EDGE,"E261.filletArc");
            var Q125;
            Q125=sQuery(id+"F1.wireOp",EDGE,"E450");
            var Q126;
            Q126=sQuery(id+"F1.wireOp",EDGE,"E456.filletArc");
            var Q127;
            Q127=sQuery(id+"F1.wireOp",EDGE,"E445");
            var Q128;
            Q128=sQuery(id+"F1.wireOp",EDGE,"E717.filletArc");
            var Q129;
            Q129=sQuery(id+"F1.wireOp",EDGE,"E711");
            var Q130;
            Q130=sQuery(id+"F1.wireOp",EDGE,"E716.filletArc");
            var Q131;
            Q131=sQuery(id+"F1.wireOp",EDGE,"E710");
            var Q132;
            Q132=sQuery(id+"F1.wireOp",EDGE,"E715.filletArc");
            var Q133;
            Q133=sQuery(id+"F1.wireOp",EDGE,"E709");
            var Q134;
            Q134=sQuery(id+"F1.wireOp",EDGE,"E720.filletArc");
            var Q135;
            Q135=sQuery(id+"F1.wireOp",EDGE,"E699");
            var Q136;
            Q136=sQuery(id+"F1.wireOp",EDGE,"E705.filletArc");
            var Q137;
            Q137=sQuery(id+"F1.wireOp",EDGE,"E253");
            var Q138;
            Q138=sQuery(id+"F1.wireOp",EDGE,"E264.filletArc");
            var Q139;
            Q139=sQuery(id+"F1.wireOp",EDGE,"E267");
            var Q140;
            Q140=sQuery(id+"F1.wireOp",EDGE,"E273.filletArc");
            var Q141;
            Q141=sQuery(id+"F1.wireOp",EDGE,"E268");
            var Q142;
            Q142=sQuery(id+"F1.wireOp",EDGE,"E228.filletArc");
            var Q143;
            Q143=sQuery(id+"F1.wireOp",EDGE,"E207");
            var Q144;
            Q144=sQuery(id+"F1.wireOp",EDGE,"E213.filletArc");
            var Q145;
            Q145=sQuery(id+"F1.wireOp",EDGE,"E25");
            var Q146;
            Q146=sQuery(id+"F1.wireOp",EDGE,"E39");
            var Q147;
            Q147=sQuery(id+"F1.wireOp",EDGE,"E36.filletArc");
            var Q148;
            Q148=sQuery(id+"F1.wireOp",EDGE,"E45.filletArc");
            var Q149;
            Q149=sQuery(id+"F1.wireOp",EDGE,"E40");
            var Q150;
            Q150=sQuery(id+"F1.wireOp",EDGE,"E12.filletArc");
            var Q151;
            Q151=sQuery(id+"F1.wireOp",EDGE,"E51");
            var Q152;
            Q152=sQuery(id+"F1.wireOp",EDGE,"E57.filletArc");
            var Q153;
            Q153=sQuery(id+"F1.wireOp",EDGE,"E61");
            var Q154;
            Q154=sQuery(id+"F1.wireOp",EDGE,"E72.filletArc");
            var Q155;
            Q155=sQuery(id+"F1.wireOp",EDGE,"E66");
            var Q156;
            Q156=sQuery(id+"F1.wireOp",EDGE,"E165.filletArc");
            var Q157;
            Q157=sQuery(id+"F1.wireOp",EDGE,"E145");
            var Q158;
            Q158=sQuery(id+"F1.wireOp",EDGE,"E156.filletArc");
            var Q159;
            Q159=sQuery(id+"F1.wireOp",EDGE,"E150");
            var Q160;
            Q160=sQuery(id+"F1.wireOp",EDGE,"E345.filletArc");
            var Q161;
            Q161=sQuery(id+"F1.wireOp",EDGE,"E361");
            var Q162;
            Q162=sQuery(id+"F1.wireOp",EDGE,"E372.filletArc");
            var Q163;
            Q163=sQuery(id+"F1.wireOp",EDGE,"E591");
            var Q164;
            Q164=sQuery(id+"F1.wireOp",EDGE,"E597.filletArc");
            var Q165;
            Q165=sQuery(id+"F1.wireOp",EDGE,"E577");
            var Q166;
            Q166=sQuery(id+"F1.wireOp",EDGE,"E598.filletArc");
            var Q167;
            Q167=sQuery(id+"F1.wireOp",EDGE,"E593");
            var Q168;
            Q168=sQuery(id+"F1.wireOp",EDGE,"E599.filletArc");
            var Q169;
            Q169=sQuery(id+"F1.wireOp",EDGE,"E594");
            var Q170;
            Q170=sQuery(id+"F1.wireOp",EDGE,"E600.filletArc");
            var Q171;
            Q171=sQuery(id+"F1.wireOp",EDGE,"E589");
            var Q172;
            Q172=sQuery(id+"F1.wireOp",EDGE,"E609.filletArc");
            var Q173;
            Q173=sQuery(id+"F1.wireOp",EDGE,"E603");
            var Q174;
            Q174=sQuery(id+"F1.wireOp",EDGE,"E348.filletArc");
            var Q175;
            Q175=sQuery(id+"F1.wireOp",EDGE,"E337");
            var Q176;
            Q176=sQuery(id+"F1.wireOp",EDGE,"E357.filletArc");
            var Q177;
            Q177=sQuery(id+"F1.wireOp",EDGE,"E162");
            var Q178;
            Q178=sQuery(id+"F1.wireOp",EDGE,"E168.filletArc");
            var Q179;
            Q179=sQuery(id+"F1.wireOp",EDGE,"E157");
            var Q180;
            Q180=sQuery(id+"F1.wireOp",EDGE,"E177.filletArc");
            var Q181;
            Q181=sQuery(id+"F1.wireOp",EDGE,"E171");
            var Q182;
            Q182=sQuery(id+"F1.wireOp",EDGE,"E60.filletArc");
            var Q183;
            Q183=sQuery(id+"F1.wireOp",EDGE,"E184");
            var Q184;
            Q184=sQuery(id+"F1.wireOp",EDGE,"E189.filletArc");
            var Q185;
            Q185=sQuery(id+"F1.wireOp",EDGE,"E42");
            var Q186;
            Q186=sQuery(id+"F1.wireOp",EDGE,"E48.filletArc");
            var Q187;
            Q187=sQuery(id+"F1.wireOp",EDGE,"E37");
            var Q188;
            Q188=sQuery(id+"F1.wireOp",EDGE,"E201.filletArc");
            var Q189;
            Q189=sQuery(id+"F1.wireOp",EDGE,"E195");
            var Q190;
            Q190=sQuery(id+"F1.wireOp",EDGE,"E216.filletArc");
            var Q191;
            Q191=sQuery(id+"F1.wireOp",EDGE,"E205");
            var Q192;
            Q192=sQuery(id+"F1.wireOp",EDGE,"E285.filletArc");
            var Q193;
            Q193=sQuery(id+"F1.wireOp",EDGE,"E279");
            var Q194;
            Q194=sQuery(id+"F1.wireOp",EDGE,"E276.filletArc");
            var Q195;
            Q195=sQuery(id+"F1.wireOp",EDGE,"E688");
            var Q196;
            Q196=sQuery(id+"F1.wireOp",EDGE,"E693.filletArc");
            var Q197;
            Q197=sQuery(id+"F1.wireOp",EDGE,"E687");
            var Q198;
            Q198=sQuery(id+"F1.wireOp",EDGE,"E692.filletArc");
            var Q199;
            Q199=sQuery(id+"F1.wireOp",EDGE,"E686");
            var Q200;
            Q200=sQuery(id+"F1.wireOp",EDGE,"E691.filletArc");
            var Q201;
            Q201=sQuery(id+"F1.wireOp",EDGE,"E685");
            var Q202;
            Q202=sQuery(id+"F1.wireOp",EDGE,"E696.filletArc");
            var Q203;
            Q203=sQuery(id+"F1.wireOp",EDGE,"E675");
            var Q204;
            Q204=sQuery(id+"F1.wireOp",EDGE,"E681.filletArc");
            var Q205;
            Q205=sQuery(id+"F1.wireOp",EDGE,"E277");
            var Q206;
            Q206=sQuery(id+"F1.wireOp",EDGE,"E288.filletArc");
            var Q207;
            Q207=sQuery(id+"F1.wireOp",EDGE,"E282");
            var Q208;
            Q208=sQuery(id+"F1.wireOp",EDGE,"E297.filletArc");
            var Q209;
            Q209=sQuery(id+"F1.wireOp",EDGE,"E292");
            var Q210;
            Q210=sQuery(id+"F1.wireOp",EDGE,"E204.filletArc");
            var Q211;
            Q211=sQuery(id+"F1.wireOp",EDGE,"E198");
            var Q212;
            Q212=sQuery(id+"F1.wireOp",EDGE,"E309.filletArc");
            var Q213;
            Q213=sQuery(id+"F1.wireOp",EDGE,"E181");
            var Q214;
            Q214=sQuery(id+"F1.wireOp",EDGE,"E192.filletArc");
            var Q215;
            Q215=sQuery(id+"F1.wireOp",EDGE,"E315");
            var Q216;
            Q216=sQuery(id+"F1.wireOp",EDGE,"E321.filletArc");
            var Q217;
            Q217=sQuery(id+"F1.wireOp",EDGE,"E316");
            var Q218;
            Q218=sQuery(id+"F1.wireOp",EDGE,"E180.filletArc");
            var Q219;
            Q219=sQuery(id+"F1.wireOp",EDGE,"E327");
            var Q220;
            Q220=sQuery(id+"F1.wireOp",EDGE,"E333.filletArc");
            var Q221;
            Q221=sQuery(id+"F1.wireOp",EDGE,"E349");
            var Q222;
            Q222=sQuery(id+"F1.wireOp",EDGE,"E360.filletArc");
            var Q223;
            Q223=sQuery(id+"F1.wireOp",EDGE,"E615");
            var Q224;
            Q224=sQuery(id+"F1.wireOp",EDGE,"E621.filletArc");
            var Q225;
            Q225=sQuery(id+"F1.wireOp",EDGE,"E601");
            var Q226;
            Q226=sQuery(id+"F1.wireOp",EDGE,"E622.filletArc");
            var Q227;
            Q227=sQuery(id+"F1.wireOp",EDGE,"E617");
            var Q228;
            Q228=sQuery(id+"F1.wireOp",EDGE,"E623.filletArc");
            var Q229;
            Q229=sQuery(id+"F1.wireOp",EDGE,"E618");
            var Q230;
            Q230=sQuery(id+"F1.wireOp",EDGE,"E624.filletArc");
            var Q231;
            Q231=sQuery(id+"F1.wireOp",EDGE,"E613");
            var Q232;
            Q232=sQuery(id+"F1.wireOp",EDGE,"E330");
            var Q233;
            Q233=sQuery(id+"F1.wireOp",EDGE,"E729.filletArc");
            var Q234;
            Q234=sQuery(id+"F1.wireOp",EDGE,"E336.filletArc");
            var Q235;
            Q235=sQuery(id+"F1.wireOp",EDGE,"E325");
            var Q236;
            Q236=sQuery(id+"F1.wireOp",EDGE,"E633.filletArc");
            var Q237;
            Q237=sQuery(id+"F1.wireOp",EDGE,"E627");
            var Q238;
            Q238=sQuery(id+"F1.wireOp",EDGE,"E324.filletArc");
            var Q239;
            Q239=sQuery(id+"F1.wireOp",EDGE,"E640");
            var Q240;
            Q240=sQuery(id+"F1.wireOp",EDGE,"E645.filletArc");
            var Q241;
            Q241=sQuery(id+"F1.wireOp",EDGE,"E639");
            var Q242;
            Q242=sQuery(id+"F1.wireOp",EDGE,"E312.filletArc");
            var Q243;
            Q243=sQuery(id+"F1.wireOp",EDGE,"E301");
            var Q244;
            Q244=sQuery(id+"F1.wireOp",EDGE,"E657.filletArc");
            var Q245;
            Q245=sQuery(id+"F1.wireOp",EDGE,"E651");
            var Q246;
            Q246=sQuery(id+"F1.wireOp",EDGE,"E300.filletArc");
            var Q247;
            Q247=sQuery(id+"F1.wireOp",EDGE,"E664");
            var Q248;
            Q248=sQuery(id+"F1.wireOp",EDGE,"E663");
            var Q249;
            Q249=sQuery(id+"F1.wireOp",EDGE,"E669.filletArc");
            var Q250;
            Q250=sQuery(id+"F1.wireOp",EDGE,"E668.filletArc");
            var Q251;
            Q251=sQuery(id+"F1.wireOp",EDGE,"E662");
            var Q252;
            Q252=sQuery(id+"F1.wireOp",EDGE,"E667.filletArc");
            var Q253;
            Q253=sQuery(id+"F1.wireOp",EDGE,"E661");
            var Q254;
            Q254=sQuery(id+"F1.wireOp",EDGE,"E672.filletArc");
            var Q255;
            Q255=sQuery(id+"F1.wireOp",EDGE,"E666");
            var Q256;
            Q256=sQuery(id+"F1.wireOp",EDGE,"E671.filletArc");
            var Q257;
            Q257=sQuery(id+"F1.wireOp",EDGE,"E650");
            sweep(context, id + "F10", {"profiles" : qUnion([Q0]), "path" : qUnion([Q1, Q2, Q3, Q4, Q5, Q6, Q7, Q8, Q9, Q10, Q11, Q12, Q13, Q14, Q15, Q16, Q17, Q18, Q19, Q20, Q21, Q22, Q23, Q24, Q25, Q26, Q27, Q28, Q29, Q30, Q31, Q32, Q33, Q34, Q35, Q36, Q37, Q38, Q39, Q40, Q41, Q42, Q43, Q44, Q45, Q46, Q47, Q48, Q49, Q50, Q51, Q52, Q53, Q54, Q55, Q56, Q57, Q58, Q59, Q60, Q61, Q62, Q63, Q64, Q65, Q66, Q67, Q68, Q69, Q70, Q71, Q72, Q73, Q74, Q75, Q76, Q77, Q78, Q79, Q80, Q81, Q82, Q83, Q84, Q85, Q86, Q87, Q88, Q89, Q90, Q91, Q92, Q93, Q94, Q95, Q96, Q97, Q98, Q99, Q100, Q101, Q102, Q103, Q104, Q105, Q106, Q107, Q108, Q109, Q110, Q111, Q112, Q113, Q114, Q115, Q116, Q117, Q118, Q119, Q120, Q121, Q122, Q123, Q124, Q125, Q126, Q127, Q128, Q129, Q130, Q131, Q132, Q133, Q134, Q135, Q136, Q137, Q138, Q139, Q140, Q141, Q142, Q143, Q144, Q145, Q146, Q147, Q148, Q149, Q150, Q151, Q152, Q153, Q154, Q155, Q156, Q157, Q158, Q159, Q160, Q161, Q162, Q163, Q164, Q165, Q166, Q167, Q168, Q169, Q170, Q171, Q172, Q173, Q174, Q175, Q176, Q177, Q178, Q179, Q180, Q181, Q182, Q183, Q184, Q185, Q186, Q187, Q188, Q189, Q190, Q191, Q192, Q193, Q194, Q195, Q196, Q197, Q198, Q199, Q200, Q201, Q202, Q203, Q204, Q205, Q206, Q207, Q208, Q209, Q210, Q211, Q212, Q213, Q214, Q215, Q216, Q217, Q218, Q219, Q220, Q221, Q222, Q223, Q224, Q225, Q226, Q227, Q228, Q229, Q230, Q231, Q232, Q233, Q234, Q235, Q236, Q237, Q238, Q239, Q240, Q241, Q242, Q243, Q244, Q245, Q246, Q247, Q248, Q249, Q250, Q251, Q252, Q253, Q254, Q255, Q256, Q257])});
        }
        {
            var Q0;
            Q0=makeQuery(id+"F10.opSweep","CAP_FACE",FACE,{"disambiguationData":[OSD([sQuery(id+"F1.wireOp",VERTEX,"E483.end"),sQuery(id+"F9.wireOp",EDGE,"E1538")])],"isStart":true});
            var Q1;
            Q1=sQuery(id+"F1.wireOp",EDGE,"E489.filletArc");
            var Q2;
            Q2=sQuery(id+"F1.wireOp",EDGE,"E484");
            var Q3;
            Q3=sQuery(id+"F1.wireOp",EDGE,"E490.filletArc");
            var Q4;
            Q4=sQuery(id+"F1.wireOp",EDGE,"E485");
            var Q5;
            Q5=sQuery(id+"F1.wireOp",EDGE,"E491.filletArc");
            var Q6;
            Q6=sQuery(id+"F1.wireOp",EDGE,"E486");
            var Q7;
            Q7=sQuery(id+"F1.wireOp",EDGE,"E492.filletArc");
            var Q8;
            Q8=sQuery(id+"F1.wireOp",EDGE,"E472");
            var Q9;
            Q9=sQuery(id+"F1.wireOp",EDGE,"E477.filletArc");
            var Q10;
            Q10=sQuery(id+"F1.wireOp",EDGE,"E471");
            var Q11;
            Q11=sQuery(id+"F1.wireOp",EDGE,"E476.filletArc");
            var Q12;
            Q12=sQuery(id+"F1.wireOp",EDGE,"E470");
            var Q13;
            Q13=sQuery(id+"F1.wireOp",EDGE,"E475.filletArc");
            var Q14;
            Q14=sQuery(id+"F1.wireOp",EDGE,"E460");
            var Q15;
            Q15=sQuery(id+"F1.wireOp",EDGE,"E466.filletArc");
            var Q16;
            Q16=sQuery(id+"F1.wireOp",EDGE,"E461");
            var Q17;
            Q17=sQuery(id+"F1.wireOp",EDGE,"E467.filletArc");
            var Q18;
            Q18=sQuery(id+"F1.wireOp",EDGE,"E243");
            var Q19;
            Q19=sQuery(id+"F1.wireOp",EDGE,"E468.filletArc");
            var Q20;
            Q20=sQuery(id+"F1.wireOp",EDGE,"E457");
            var Q21;
            Q21=sQuery(id+"F1.wireOp",EDGE,"E453.filletArc");
            var Q22;
            Q22=sQuery(id+"F1.wireOp",EDGE,"E447");
            var Q23;
            Q23=sQuery(id+"F1.wireOp",EDGE,"E452.filletArc");
            var Q24;
            Q24=sQuery(id+"F1.wireOp",EDGE,"E446");
            var Q25;
            Q25=sQuery(id+"F1.wireOp",EDGE,"E451.filletArc");
            var Q26;
            Q26=sQuery(id+"F1.wireOp",EDGE,"E445");
            var Q27;
            Q27=sQuery(id+"F1.wireOp",EDGE,"E718.filletArc");
            var Q28;
            Q28=sQuery(id+"F1.wireOp",EDGE,"E713");
            var Q29;
            Q29=sQuery(id+"F1.wireOp",EDGE,"E719.filletArc");
            var Q30;
            Q30=sQuery(id+"F1.wireOp",EDGE,"E699");
            var Q31;
            Q31=sQuery(id+"F1.wireOp",EDGE,"E704.filletArc");
            var Q32;
            Q32=sQuery(id+"F1.wireOp",EDGE,"E698");
            var Q33;
            Q33=sQuery(id+"F1.wireOp",EDGE,"E703.filletArc");
            var Q34;
            Q34=sQuery(id+"F1.wireOp",EDGE,"E697");
            var Q35;
            Q35=sQuery(id+"F1.wireOp",EDGE,"E708.filletArc");
            var Q36;
            Q36=sQuery(id+"F1.wireOp",EDGE,"E687");
            var Q37;
            Q37=sQuery(id+"F1.wireOp",EDGE,"E693.filletArc");
            var Q38;
            Q38=sQuery(id+"F1.wireOp",EDGE,"E688");
            var Q39;
            Q39=sQuery(id+"F1.wireOp",EDGE,"E694.filletArc");
            var Q40;
            Q40=sQuery(id+"F1.wireOp",EDGE,"E689");
            var Q41;
            Q41=sQuery(id+"F1.wireOp",EDGE,"E695.filletArc");
            var Q42;
            Q42=sQuery(id+"F1.wireOp",EDGE,"E675");
            var Q43;
            Q43=sQuery(id+"F1.wireOp",EDGE,"E680.filletArc");
            var Q44;
            Q44=sQuery(id+"F1.wireOp",EDGE,"E674");
            var Q45;
            Q45=sQuery(id+"F1.wireOp",EDGE,"E679.filletArc");
            var Q46;
            Q46=sQuery(id+"F1.wireOp",EDGE,"E673");
            var Q47;
            Q47=sQuery(id+"F1.wireOp",EDGE,"E684.filletArc");
            var Q48;
            Q48=sQuery(id+"F1.wireOp",EDGE,"E663");
            var Q49;
            Q49=sQuery(id+"F1.wireOp",EDGE,"E683.filletArc");
            var Q50;
            Q50=sQuery(id+"F1.wireOp",EDGE,"E290");
            var Q51;
            Q51=sQuery(id+"F1.wireOp",EDGE,"E296.filletArc");
            var Q52;
            Q52=sQuery(id+"F1.wireOp",EDGE,"E282");
            var Q53;
            Q53=sQuery(id+"F1.wireOp",EDGE,"E287.filletArc");
            var Q54;
            Q54=sQuery(id+"F1.wireOp",EDGE,"E281");
            var Q55;
            Q55=sQuery(id+"F1.wireOp",EDGE,"E286.filletArc");
            var Q56;
            Q56=sQuery(id+"F1.wireOp",EDGE,"E205");
            var Q57;
            Q57=sQuery(id+"F1.wireOp",EDGE,"E211.filletArc");
            var Q58;
            Q58=sQuery(id+"F1.wireOp",EDGE,"E269");
            var Q59;
            Q59=sQuery(id+"F1.wireOp",EDGE,"E274.filletArc");
            var Q60;
            Q60=sQuery(id+"F1.wireOp",EDGE,"E268");
            var Q61;
            Q61=sQuery(id+"F1.wireOp",EDGE,"E223.filletArc");
            var Q62;
            Q62=sQuery(id+"F1.wireOp",EDGE,"E218");
            var Q63;
            Q63=sQuery(id+"F1.wireOp",EDGE,"E224.filletArc");
            var Q64;
            Q64=sQuery(id+"F1.wireOp",EDGE,"E219");
            var Q65;
            Q65=sQuery(id+"F1.wireOp",EDGE,"E251.filletArc");
            var Q66;
            Q66=sQuery(id+"F1.wireOp",EDGE,"E245");
            var Q67;
            Q67=sQuery(id+"F1.wireOp",EDGE,"E104.filletArc");
            var Q68;
            Q68=sQuery(id+"F1.wireOp",EDGE,"E234");
            var Q69;
            Q69=sQuery(id+"F1.wireOp",EDGE,"E239.filletArc");
            var Q70;
            Q70=sQuery(id+"F1.wireOp",EDGE,"E233");
            var Q71;
            Q71=sQuery(id+"F1.wireOp",EDGE,"E92.filletArc");
            var Q72;
            Q72=sQuery(id+"F1.wireOp",EDGE,"E87");
            var Q73;
            Q73=sQuery(id+"F1.wireOp",EDGE,"E443.filletArc");
            var Q74;
            Q74=sQuery(id+"F1.wireOp",EDGE,"E422");
            var Q75;
            Q75=sQuery(id+"F1.wireOp",EDGE,"E428.filletArc");
            var Q76;
            Q76=sQuery(id+"F1.wireOp",EDGE,"E423");
            var Q77;
            Q77=sQuery(id+"F1.wireOp",EDGE,"E503.filletArc");
            var Q78;
            Q78=sQuery(id+"F1.wireOp",EDGE,"E506");
            var Q79;
            Q79=sQuery(id+"F1.wireOp",EDGE,"E512.filletArc");
            var Q80;
            Q80=sQuery(id+"F1.wireOp",EDGE,"E507");
            var Q81;
            Q81=sQuery(id+"F1.wireOp",EDGE,"E513.filletArc");
            var Q82;
            Q82=sQuery(id+"F1.wireOp",EDGE,"E508");
            var Q83;
            Q83=sQuery(id+"F1.wireOp",EDGE,"E514.filletArc");
            var Q84;
            Q84=sQuery(id+"F1.wireOp",EDGE,"E509");
            var Q85;
            Q85=sQuery(id+"F1.wireOp",EDGE,"E515.filletArc");
            var Q86;
            Q86=sQuery(id+"F1.wireOp",EDGE,"E411");
            var Q87;
            Q87=sQuery(id+"F1.wireOp",EDGE,"E416.filletArc");
            var Q88;
            Q88=sQuery(id+"F1.wireOp",EDGE,"E410");
            var Q89;
            Q89=sQuery(id+"F1.wireOp",EDGE,"E431.filletArc");
            var Q90;
            Q90=sQuery(id+"F1.wireOp",EDGE,"E426");
            var Q91;
            Q91=sQuery(id+"F1.wireOp",EDGE,"E116.filletArc");
            var Q92;
            Q92=sQuery(id+"F1.wireOp",EDGE,"E89");
            var Q93;
            Q93=sQuery(id+"F1.wireOp",EDGE,"E95.filletArc");
            var Q94;
            Q94=sQuery(id+"F1.wireOp",EDGE,"E90");
            var Q95;
            Q95=sQuery(id+"F1.wireOp",EDGE,"E20.filletArc");
            var Q96;
            Q96=sQuery(id+"F1.wireOp",EDGE,"E101");
            var Q97;
            Q97=sQuery(id+"F1.wireOp",EDGE,"E107.filletArc");
            var Q98;
            Q98=sQuery(id+"F1.wireOp",EDGE,"E27");
            var Q99;
            Q99=sQuery(id+"F1.wireOp",EDGE,"E32.filletArc");
            var Q100;
            Q100=sQuery(id+"F1.wireOp",EDGE,"E221");
            var Q101;
            Q101=sQuery(id+"F1.wireOp",EDGE,"E31.filletArc");
            var Q102;
            Q102=sQuery(id+"F1.wireOp",EDGE,"E25");
            var Q103;
            Q103=sQuery(id+"F1.wireOp",EDGE,"E214.filletArc");
            var Q104;
            Q104=sQuery(id+"F1.wireOp",EDGE,"E38");
            var Q105;
            Q105=sQuery(id+"F1.wireOp",EDGE,"E43.filletArc");
            var Q106;
            Q106=sQuery(id+"F1.wireOp",EDGE,"E37");
            var Q107;
            Q107=sQuery(id+"F1.wireOp",EDGE,"E202.filletArc");
            var Q108;
            Q108=sQuery(id+"F1.wireOp",EDGE,"E182");
            var Q109;
            Q109=sQuery(id+"F1.wireOp",EDGE,"E203.filletArc");
            var Q110;
            Q110=sQuery(id+"F1.wireOp",EDGE,"E198");
            var Q111;
            Q111=sQuery(id+"F1.wireOp",EDGE,"E308.filletArc");
            var Q112;
            Q112=sQuery(id+"F1.wireOp",EDGE,"E293");
            var Q113;
            Q113=sQuery(id+"F1.wireOp",EDGE,"E299.filletArc");
            var Q114;
            Q114=sQuery(id+"F1.wireOp",EDGE,"E651");
            var Q115;
            Q115=sQuery(id+"F1.wireOp",EDGE,"E656.filletArc");
            var Q116;
            Q116=sQuery(id+"F1.wireOp",EDGE,"E650");
            var Q117;
            Q117=sQuery(id+"F1.wireOp",EDGE,"E655.filletArc");
            var Q118;
            Q118=sQuery(id+"F1.wireOp",EDGE,"E649");
            var Q119;
            Q119=sQuery(id+"F1.wireOp",EDGE,"E660.filletArc");
            var Q120;
            Q120=sQuery(id+"F1.wireOp",EDGE,"E654");
            var Q121;
            Q121=sQuery(id+"F1.wireOp",EDGE,"E659.filletArc");
            var Q122;
            Q122=sQuery(id+"F1.wireOp",EDGE,"E638");
            var Q123;
            Q123=sQuery(id+"F1.wireOp",EDGE,"E644.filletArc");
            var Q124;
            Q124=sQuery(id+"F1.wireOp",EDGE,"E639");
            var Q125;
            Q125=sQuery(id+"F1.wireOp",EDGE,"E311.filletArc");
            var Q126;
            Q126=sQuery(id+"F1.wireOp",EDGE,"E314");
            var Q127;
            Q127=sQuery(id+"F1.wireOp",EDGE,"E320.filletArc");
            var Q128;
            Q128=sQuery(id+"F1.wireOp",EDGE,"E315");
            var Q129;
            Q129=sQuery(id+"F1.wireOp",EDGE,"E191.filletArc");
            var Q130;
            Q130=sQuery(id+"F1.wireOp",EDGE,"E170");
            var Q131;
            Q131=sQuery(id+"F1.wireOp",EDGE,"E190.filletArc");
            var Q132;
            Q132=sQuery(id+"F1.wireOp",EDGE,"E184");
            var Q133;
            Q133=sQuery(id+"F1.wireOp",EDGE,"E55.filletArc");
            var Q134;
            Q134=sQuery(id+"F1.wireOp",EDGE,"E41");
            var Q135;
            Q135=sQuery(id+"F1.wireOp",EDGE,"E46.filletArc");
            var Q136;
            Q136=sQuery(id+"F1.wireOp",EDGE,"E40");
            var Q137;
            Q137=sQuery(id+"F1.wireOp",EDGE,"E7.filletArc");
            var Q138;
            Q138=sQuery(id+"F1.wireOp",EDGE,"E29");
            var Q139;
            Q139=sQuery(id+"F1.wireOp",EDGE,"E8.filletArc");
            var Q140;
            Q140=sQuery(id+"F1.wireOp",EDGE,"E18");
            var Q141;
            Q141=sQuery(id+"F1.wireOp",EDGE,"E23.filletArc");
            var Q142;
            Q142=sQuery(id+"F1.wireOp",EDGE,"E74");
            var Q143;
            Q143=sQuery(id+"F1.wireOp",EDGE,"E80.filletArc");
            var Q144;
            Q144=sQuery(id+"F1.wireOp",EDGE,"E75");
            var Q145;
            Q145=sQuery(id+"F1.wireOp",EDGE,"E119.filletArc");
            var Q146;
            Q146=sQuery(id+"F1.wireOp",EDGE,"E122");
            var Q147;
            Q147=sQuery(id+"F1.wireOp",EDGE,"E128.filletArc");
            var Q148;
            Q148=sQuery(id+"F1.wireOp",EDGE,"E123");
            var Q149;
            Q149=sQuery(id+"F1.wireOp",EDGE,"E419.filletArc");
            var Q150;
            Q150=sQuery(id+"F1.wireOp",EDGE,"E413");
            var Q151;
            Q151=sQuery(id+"F1.wireOp",EDGE,"E404.filletArc");
            var Q152;
            Q152=sQuery(id+"F1.wireOp",EDGE,"E522");
            var Q153;
            Q153=sQuery(id+"F1.wireOp",EDGE,"E527.filletArc");
            var Q154;
            Q154=sQuery(id+"F1.wireOp",EDGE,"E521");
            var Q155;
            Q155=sQuery(id+"F1.wireOp",EDGE,"E536.filletArc");
            var Q156;
            Q156=sQuery(id+"F1.wireOp",EDGE,"E531");
            var Q157;
            Q157=sQuery(id+"F1.wireOp",EDGE,"E537.filletArc");
            var Q158;
            Q158=sQuery(id+"F1.wireOp",EDGE,"E532");
            var Q159;
            Q159=sQuery(id+"F1.wireOp",EDGE,"E538.filletArc");
            var Q160;
            Q160=sQuery(id+"F1.wireOp",EDGE,"E533");
            var Q161;
            Q161=sQuery(id+"F1.wireOp",EDGE,"E539.filletArc");
            var Q162;
            Q162=sQuery(id+"F1.wireOp",EDGE,"E555");
            var Q163;
            Q163=sQuery(id+"F1.wireOp",EDGE,"E560.filletArc");
            var Q164;
            Q164=sQuery(id+"F1.wireOp",EDGE,"E554");
            var Q165;
            Q165=sQuery(id+"F1.wireOp",EDGE,"E407.filletArc");
            var Q166;
            Q166=sQuery(id+"F1.wireOp",EDGE,"E387");
            var Q167;
            Q167=sQuery(id+"F1.wireOp",EDGE,"E392.filletArc");
            var Q168;
            Q168=sQuery(id+"F1.wireOp",EDGE,"E125");
            var Q169;
            Q169=sQuery(id+"F1.wireOp",EDGE,"E135");
            var Q170;
            Q170=sQuery(id+"F1.wireOp",EDGE,"E140.filletArc");
            var Q171;
            Q171=sQuery(id+"F1.wireOp",EDGE,"E77");
            var Q172;
            Q172=sQuery(id+"F1.wireOp",EDGE,"E83.filletArc");
            var Q173;
            Q173=sQuery(id+"F1.wireOp",EDGE,"E63");
            var Q174;
            Q174=sQuery(id+"F1.wireOp",EDGE,"E68.filletArc");
            var Q175;
            Q175=sQuery(id+"F1.wireOp",EDGE,"E62");
            var Q176;
            Q176=sQuery(id+"F1.wireOp",EDGE,"E67.filletArc");
            var Q177;
            Q177=sQuery(id+"F1.wireOp",EDGE,"E61");
            var Q178;
            Q178=sQuery(id+"F1.wireOp",EDGE,"E58.filletArc");
            var Q179;
            Q179=sQuery(id+"F1.wireOp",EDGE,"E53");
            var Q180;
            Q180=sQuery(id+"F1.wireOp",EDGE,"E163.filletArc");
            var Q181;
            Q181=sQuery(id+"F1.wireOp",EDGE,"E157");
            var Q182;
            Q182=sQuery(id+"F1.wireOp",EDGE,"E178.filletArc");
            var Q183;
            Q183=sQuery(id+"F1.wireOp",EDGE,"E173");
            var Q184;
            Q184=sQuery(id+"F1.wireOp",EDGE,"E179.filletArc");
            var Q185;
            Q185=sQuery(id+"F1.wireOp",EDGE,"E327");
            var Q186;
            Q186=sQuery(id+"F1.wireOp",EDGE,"E332.filletArc");
            var Q187;
            Q187=sQuery(id+"F1.wireOp",EDGE,"E317");
            var Q188;
            Q188=sQuery(id+"F1.wireOp",EDGE,"E323.filletArc");
            var Q189;
            Q189=sQuery(id+"F1.wireOp",EDGE,"E627");
            var Q190;
            Q190=sQuery(id+"F1.wireOp",EDGE,"E632.filletArc");
            var Q191;
            Q191=sQuery(id+"F1.wireOp",EDGE,"E641");
            var Q192;
            Q192=sQuery(id+"F1.wireOp",EDGE,"E631.filletArc");
            var Q193;
            Q193=sQuery(id+"F1.wireOp",EDGE,"E625");
            var Q194;
            Q194=sQuery(id+"F1.wireOp",EDGE,"E636.filletArc");
            var Q195;
            Q195=sQuery(id+"F1.wireOp",EDGE,"E630");
            var Q196;
            Q196=sQuery(id+"F1.wireOp",EDGE,"E635.filletArc");
            var Q197;
            Q197=sQuery(id+"F1.wireOp",EDGE,"E629");
            var Q198;
            Q198=sQuery(id+"F1.wireOp",EDGE,"E728.filletArc");
            var Q199;
            Q199=sQuery(id+"F1.wireOp",EDGE,"E330");
            var Q200;
            Q200=sQuery(id+"F1.wireOp",EDGE,"E335.filletArc");
            var Q201;
            Q201=sQuery(id+"F1.wireOp",EDGE,"E329");
            var Q202;
            Q202=sQuery(id+"F1.wireOp",EDGE,"E620.filletArc");
            var Q203;
            Q203=sQuery(id+"F1.wireOp",EDGE,"E615");
            var Q204;
            Q204=sQuery(id+"F1.wireOp",EDGE,"E359.filletArc");
            var Q205;
            Q205=sQuery(id+"F1.wireOp",EDGE,"E602");
            var Q206;
            Q206=sQuery(id+"F1.wireOp",EDGE,"E358.filletArc");
            var Q207;
            Q207=sQuery(id+"F1.wireOp",EDGE,"E337");
            var Q208;
            Q208=sQuery(id+"F1.wireOp",EDGE,"E343.filletArc");
            var Q209;
            Q209=sQuery(id+"F1.wireOp",EDGE,"E338");
            var Q210;
            Q210=sQuery(id+"F1.wireOp",EDGE,"E166.filletArc");
            var Q211;
            Q211=sQuery(id+"F1.wireOp",EDGE,"E145");
            var Q212;
            Q212=sQuery(id+"F1.wireOp",EDGE,"E151.filletArc");
            var Q213;
            Q213=sQuery(id+"F1.wireOp",EDGE,"E146");
            var Q214;
            Q214=sQuery(id+"F1.wireOp",EDGE,"E152.filletArc");
            var Q215;
            Q215=sQuery(id+"F1.wireOp",EDGE,"E138");
            var Q216;
            Q216=sQuery(id+"F1.wireOp",EDGE,"E143.filletArc");
            var Q217;
            Q217=sQuery(id+"F1.wireOp",EDGE,"E137");
            var Q218;
            Q218=sQuery(id+"F1.wireOp",EDGE,"E380.filletArc");
            var Q219;
            Q219=sQuery(id+"F1.wireOp",EDGE,"E375");
            var Q220;
            Q220=sQuery(id+"F1.wireOp",EDGE,"E395.filletArc");
            var Q221;
            Q221=sQuery(id+"F1.wireOp",EDGE,"E389");
            var Q222;
            Q222=sQuery(id+"F1.wireOp",EDGE,"E548.filletArc");
            var Q223;
            Q223=sQuery(id+"F1.wireOp",EDGE,"E558");
            var Q224;
            Q224=sQuery(id+"F1.wireOp",EDGE,"E549.filletArc");
            var Q225;
            Q225=sQuery(id+"F1.wireOp",EDGE,"E544");
            var Q226;
            Q226=sQuery(id+"F1.wireOp",EDGE,"E550.filletArc");
            var Q227;
            Q227=sQuery(id+"F1.wireOp",EDGE,"E545");
            var Q228;
            Q228=sQuery(id+"F1.wireOp",EDGE,"E551.filletArc");
            var Q229;
            Q229=sQuery(id+"F1.wireOp",EDGE,"E567");
            var Q230;
            Q230=sQuery(id+"F1.wireOp",EDGE,"E572.filletArc");
            var Q231;
            Q231=sQuery(id+"F1.wireOp",EDGE,"E377");
            var Q232;
            Q232=sQuery(id+"F1.wireOp",EDGE,"E383.filletArc");
            var Q233;
            Q233=sQuery(id+"F1.wireOp",EDGE,"E363");
            var Q234;
            Q234=sQuery(id+"F1.wireOp",EDGE,"E368.filletArc");
            var Q235;
            Q235=sQuery(id+"F1.wireOp",EDGE,"E362");
            var Q236;
            Q236=sQuery(id+"F1.wireOp",EDGE,"E367.filletArc");
            var Q237;
            Q237=sQuery(id+"F1.wireOp",EDGE,"E361");
            var Q238;
            Q238=sQuery(id+"F1.wireOp",EDGE,"E346.filletArc");
            var Q239;
            Q239=sQuery(id+"F1.wireOp",EDGE,"E590");
            var Q240;
            Q240=sQuery(id+"F1.wireOp",EDGE,"E595.filletArc");
            var Q241;
            Q241=sQuery(id+"F1.wireOp",EDGE,"E589");
            var Q242;
            Q242=sQuery(id+"F1.wireOp",EDGE,"E610.filletArc");
            var Q243;
            Q243=sQuery(id+"F1.wireOp",EDGE,"E605");
            var Q244;
            Q244=sQuery(id+"F1.wireOp",EDGE,"E611.filletArc");
            var Q245;
            Q245=sQuery(id+"F1.wireOp",EDGE,"E606");
            var Q246;
            Q246=sQuery(id+"F1.wireOp",EDGE,"E131.filletArc");
            var Q247;
            Q247=sQuery(id+"F1.wireOp",EDGE,"E612.filletArc");
            var Q248;
            Q248=sQuery(id+"F1.wireOp",EDGE,"E601");
            sweep(context, id + "F11", {"operationType" : NewBodyOperationType.ADD, "profiles" : qUnion([Q0]), "path" : qUnion([Q1, Q2, Q3, Q4, Q5, Q6, Q7, Q8, Q9, Q10, Q11, Q12, Q13, Q14, Q15, Q16, Q17, Q18, Q19, Q20, Q21, Q22, Q23, Q24, Q25, Q26, Q27, Q28, Q29, Q30, Q31, Q32, Q33, Q34, Q35, Q36, Q37, Q38, Q39, Q40, Q41, Q42, Q43, Q44, Q45, Q46, Q47, Q48, Q49, Q50, Q51, Q52, Q53, Q54, Q55, Q56, Q57, Q58, Q59, Q60, Q61, Q62, Q63, Q64, Q65, Q66, Q67, Q68, Q69, Q70, Q71, Q72, Q73, Q74, Q75, Q76, Q77, Q78, Q79, Q80, Q81, Q82, Q83, Q84, Q85, Q86, Q87, Q88, Q89, Q90, Q91, Q92, Q93, Q94, Q95, Q96, Q97, Q98, Q99, Q100, Q101, Q102, Q103, Q104, Q105, Q106, Q107, Q108, Q109, Q110, Q111, Q112, Q113, Q114, Q115, Q116, Q117, Q118, Q119, Q120, Q121, Q122, Q123, Q124, Q125, Q126, Q127, Q128, Q129, Q130, Q131, Q132, Q133, Q134, Q135, Q136, Q137, Q138, Q139, Q140, Q141, Q142, Q143, Q144, Q145, Q146, Q147, Q148, Q149, Q150, Q151, Q152, Q153, Q154, Q155, Q156, Q157, Q158, Q159, Q160, Q161, Q162, Q163, Q164, Q165, Q166, Q167, Q168, Q169, Q170, Q171, Q172, Q173, Q174, Q175, Q176, Q177, Q178, Q179, Q180, Q181, Q182, Q183, Q184, Q185, Q186, Q187, Q188, Q189, Q190, Q191, Q192, Q193, Q194, Q195, Q196, Q197, Q198, Q199, Q200, Q201, Q202, Q203, Q204, Q205, Q206, Q207, Q208, Q209, Q210, Q211, Q212, Q213, Q214, Q215, Q216, Q217, Q218, Q219, Q220, Q221, Q222, Q223, Q224, Q225, Q226, Q227, Q228, Q229, Q230, Q231, Q232, Q233, Q234, Q235, Q236, Q237, Q238, Q239, Q240, Q241, Q242, Q243, Q244, Q245, Q246, Q247, Q248])});
        }
        {
            var Q0;
            Q0 = qSketchRegion(id + "F9", true);
            var Q1;
            Q1=sQuery(id+"F1.wireOp",EDGE,"E483");
            var Q2;
            Q2=sQuery(id+"F1.wireOp",EDGE,"E488.filletArc");
            var Q3;
            Q3=sQuery(id+"F1.wireOp",EDGE,"E482");
            var Q4;
            Q4=sQuery(id+"F1.wireOp",EDGE,"E487.filletArc");
            var Q5;
            Q5=sQuery(id+"F1.wireOp",EDGE,"E472");
            var Q6;
            Q6=sQuery(id+"F1.wireOp",EDGE,"E478.filletArc");
            var Q7;
            Q7=sQuery(id+"F1.wireOp",EDGE,"E473");
            var Q8;
            Q8=sQuery(id+"F1.wireOp",EDGE,"E479.filletArc");
            var Q9;
            Q9=sQuery(id+"F1.wireOp",EDGE,"E474");
            var Q10;
            Q10=sQuery(id+"F1.wireOp",EDGE,"E236.filletArc");
            var Q11;
            Q11=sQuery(id+"F1.wireOp",EDGE,"E461");
            var Q12;
            Q12=sQuery(id+"F1.wireOp",EDGE,"E467.filletArc");
            var Q13;
            Q13=sQuery(id+"F1.wireOp",EDGE,"E243");
            var Q14;
            Q14=sQuery(id+"F1.wireOp",EDGE,"E248.filletArc");
            var Q15;
            Q15=sQuery(id+"F1.wireOp",EDGE,"E242");
            var Q16;
            Q16=sQuery(id+"F1.wireOp",EDGE,"E455.filletArc");
            var Q17;
            Q17=sQuery(id+"F1.wireOp",EDGE,"E450");
            var Q18;
            Q18=sQuery(id+"F1.wireOp",EDGE,"E260.filletArc");
            var Q19;
            Q19=sQuery(id+"F1.wireOp",EDGE,"E713");
            var Q20;
            Q20=sQuery(id+"F1.wireOp",EDGE,"E259.filletArc");
            var Q21;
            Q21=sQuery(id+"F1.wireOp",EDGE,"E253");
            var Q22;
            Q22=sQuery(id+"F1.wireOp",EDGE,"E706.filletArc");
            var Q23;
            Q23=sQuery(id+"F1.wireOp",EDGE,"E266");
            var Q24;
            Q24=sQuery(id+"F1.wireOp",EDGE,"E271.filletArc");
            var Q25;
            Q25=sQuery(id+"F1.wireOp",EDGE,"E266");
            var Q26;
            Q26=sQuery(id+"F1.wireOp",EDGE,"E688");
            var Q27;
            Q27=sQuery(id+"F1.wireOp",EDGE,"E694.filletArc");
            var Q28;
            Q28=sQuery(id+"F1.wireOp",EDGE,"E689");
            var Q29;
            Q29=sQuery(id+"F1.wireOp",EDGE,"E283.filletArc");
            var Q30;
            Q30=sQuery(id+"F1.wireOp",EDGE,"E277");
            var Q31;
            Q31=sQuery(id+"F1.wireOp",EDGE,"E682.filletArc");
            var Q32;
            Q32=sQuery(id+"F1.wireOp",EDGE,"E290");
            var Q33;
            Q33=sQuery(id+"F1.wireOp",EDGE,"E295.filletArc");
            var Q34;
            Q34=sQuery(id+"F1.wireOp",EDGE,"E664");
            var Q35;
            Q35=sQuery(id+"F1.wireOp",EDGE,"E300.filletArc");
            var Q36;
            Q36=sQuery(id+"F1.wireOp",EDGE,"E651");
            var Q37;
            Q37=sQuery(id+"F1.wireOp",EDGE,"E657.filletArc");
            var Q38;
            Q38=sQuery(id+"F1.wireOp",EDGE,"E301");
            var Q39;
            Q39=sQuery(id+"F1.wireOp",EDGE,"E658.filletArc");
            var Q40;
            Q40=sQuery(id+"F1.wireOp",EDGE,"E638");
            var Q41;
            Q41=sQuery(id+"F1.wireOp",EDGE,"E643.filletArc");
            var Q42;
            Q42=sQuery(id+"F1.wireOp",EDGE,"E648.filletArc");
            var Q43;
            Q43=sQuery(id+"F1.wireOp",EDGE,"E637");
            var Q44;
            Q44=sQuery(id+"F1.wireOp",EDGE,"E642");
            var Q45;
            Q45=sQuery(id+"F1.wireOp",EDGE,"E647.filletArc");
            var Q46;
            Q46=sQuery(id+"F1.wireOp",EDGE,"E641");
            var Q47;
            Q47=sQuery(id+"F1.wireOp",EDGE,"E641");
            var Q48;
            Q48=sQuery(id+"F1.wireOp",EDGE,"E632.filletArc");
            var Q49;
            Q49=sQuery(id+"F1.wireOp",EDGE,"E627");
            var Q50;
            Q50=sQuery(id+"F1.wireOp",EDGE,"E633.filletArc");
            var Q51;
            Q51=sQuery(id+"F1.wireOp",EDGE,"E325");
            var Q52;
            Q52=sQuery(id+"F1.wireOp",EDGE,"E634.filletArc");
            var Q53;
            Q53=sQuery(id+"F1.wireOp",EDGE,"E629");
            var Q54;
            Q54=sQuery(id+"F1.wireOp",EDGE,"E727.filletArc");
            var Q55;
            Q55=sQuery(id+"F1.wireOp",EDGE,"E721");
            var Q56;
            Q56=sQuery(id+"F1.wireOp",EDGE,"E732.filletArc");
            var Q57;
            Q57=sQuery(id+"F1.wireOp",EDGE,"E726");
            var Q58;
            Q58=sQuery(id+"F1.wireOp",EDGE,"E731.filletArc");
            var Q59;
            Q59=sQuery(id+"F1.wireOp",EDGE,"E725");
            var Q60;
            Q60=sQuery(id+"F1.wireOp",EDGE,"E730.filletArc");
            var Q61;
            Q61=sQuery(id+"F1.wireOp",EDGE,"E613");
            var Q62;
            Q62=sQuery(id+"F1.wireOp",EDGE,"E619.filletArc");
            var Q63;
            Q63=sQuery(id+"F1.wireOp",EDGE,"E329");
            var Q64;
            Q64=sQuery(id+"F1.wireOp",EDGE,"E620.filletArc");
            var Q65;
            Q65=sQuery(id+"F1.wireOp",EDGE,"E615");
            var Q66;
            Q66=sQuery(id+"F1.wireOp",EDGE,"E359.filletArc");
            var Q67;
            Q67=sQuery(id+"F1.wireOp",EDGE,"E602");
            var Q68;
            Q68=sQuery(id+"F1.wireOp",EDGE,"E608.filletArc");
            var Q69;
            Q69=sQuery(id+"F1.wireOp",EDGE,"E603");
            var Q70;
            Q70=sQuery(id+"F1.wireOp",EDGE,"E347.filletArc");
            var Q71;
            Q71=sQuery(id+"F1.wireOp",EDGE,"E596.filletArc");
            var Q72;
            Q72=sQuery(id+"F1.wireOp",EDGE,"E591");
            var Q73;
            Q73=sQuery(id+"F1.wireOp",EDGE,"E597.filletArc");
            var Q74;
            Q74=sQuery(id+"F1.wireOp",EDGE,"E590");
            var Q75;
            Q75=sQuery(id+"F1.wireOp",EDGE,"E577");
            var Q76;
            Q76=sQuery(id+"F1.wireOp",EDGE,"E588.filletArc");
            var Q77;
            Q77=sQuery(id+"F1.wireOp",EDGE,"E582");
            var Q78;
            Q78=sQuery(id+"F1.wireOp",EDGE,"E587.filletArc");
            var Q79;
            Q79=sQuery(id+"F1.wireOp",EDGE,"E581");
            var Q80;
            Q80=sQuery(id+"F1.wireOp",EDGE,"E586.filletArc");
            var Q81;
            Q81=sQuery(id+"F1.wireOp",EDGE,"E580");
            var Q82;
            Q82=sQuery(id+"F1.wireOp",EDGE,"E585.filletArc");
            var Q83;
            Q83=sQuery(id+"F1.wireOp",EDGE,"E570");
            var Q84;
            Q84=sQuery(id+"F1.wireOp",EDGE,"E576.filletArc");
            var Q85;
            Q85=sQuery(id+"F1.wireOp",EDGE,"E364");
            var Q86;
            Q86=sQuery(id+"F1.wireOp",EDGE,"E571.filletArc");
            var Q87;
            Q87=sQuery(id+"F1.wireOp",EDGE,"E377");
            var Q88;
            Q88=sQuery(id+"F1.wireOp",EDGE,"E382.filletArc");
            var Q89;
            Q89=sQuery(id+"F1.wireOp",EDGE,"E541");
            var Q90;
            Q90=sQuery(id+"F1.wireOp",EDGE,"E547.filletArc");
            var Q91;
            Q91=sQuery(id+"F1.wireOp",EDGE,"E389");
            var Q92;
            Q92=sQuery(id+"F1.wireOp",EDGE,"E394.filletArc");
            var Q93;
            Q93=sQuery(id+"F1.wireOp",EDGE,"E553");
            var Q94;
            Q94=sQuery(id+"F1.wireOp",EDGE,"E559.filletArc");
            var Q95;
            Q95=sQuery(id+"F1.wireOp",EDGE,"E554");
            var Q96;
            Q96=sQuery(id+"F1.wireOp",EDGE,"E406.filletArc");
            var Q97;
            Q97=sQuery(id+"F1.wireOp",EDGE,"E529");
            var Q98;
            Q98=sQuery(id+"F1.wireOp",EDGE,"E405.filletArc");
            var Q99;
            Q99=sQuery(id+"F1.wireOp",EDGE,"E522");
            var Q100;
            Q100=sQuery(id+"F1.wireOp",EDGE,"E528.filletArc");
            var Q101;
            Q101=sQuery(id+"F1.wireOp",EDGE,"E412");
            var Q102;
            Q102=sQuery(id+"F1.wireOp",EDGE,"E417.filletArc");
            var Q103;
            Q103=sQuery(id+"F1.wireOp",EDGE,"E411");
            var Q104;
            Q104=sQuery(id+"F1.wireOp",EDGE,"E516.filletArc");
            var Q105;
            Q105=sQuery(id+"F1.wireOp",EDGE,"E505");
            var Q106;
            Q106=sQuery(id+"F1.wireOp",EDGE,"E429.filletArc");
            var Q107;
            Q107=sQuery(id+"F1.wireOp",EDGE,"E423");
            var Q108;
            Q108=sQuery(id+"F1.wireOp",EDGE,"E504.filletArc");
            var Q109;
            Q109=sQuery(id+"F1.wireOp",EDGE,"E493");
            var Q110;
            Q110=sQuery(id+"F1.wireOp",EDGE,"E486");
            var Q111;
            Q111=sQuery(id+"F1.wireOp",EDGE,"E441.filletArc");
            sweep(context, id + "F12", {"operationType" : NewBodyOperationType.ADD, "profiles" : qUnion([Q0]), "path" : qUnion([Q1, Q2, Q3, Q4, Q5, Q6, Q7, Q8, Q9, Q10, Q11, Q12, Q13, Q14, Q15, Q16, Q17, Q18, Q19, Q20, Q21, Q22, Q23, Q24, Q25, Q26, Q27, Q28, Q29, Q30, Q31, Q32, Q33, Q34, Q35, Q36, Q37, Q38, Q39, Q40, Q41, Q42, Q43, Q44, Q45, Q46, Q47, Q48, Q49, Q50, Q51, Q52, Q53, Q54, Q55, Q56, Q57, Q58, Q59, Q60, Q61, Q62, Q63, Q64, Q65, Q66, Q67, Q68, Q69, Q70, Q71, Q72, Q73, Q74, Q75, Q76, Q77, Q78, Q79, Q80, Q81, Q82, Q83, Q84, Q85, Q86, Q87, Q88, Q89, Q90, Q91, Q92, Q93, Q94, Q95, Q96, Q97, Q98, Q99, Q100, Q101, Q102, Q103, Q104, Q105, Q106, Q107, Q108, Q109, Q110, Q111])});
        }
        {
            var Q0;
            Q0 = qSketchRegion(id + "F9", true);
            var Q1;
            Q1=sQuery(id+"F1.wireOp",EDGE,"E489.filletArc");
            var Q2;
            Q2=sQuery(id+"F1.wireOp",EDGE,"E484");
            var Q3;
            Q3=sQuery(id+"F1.wireOp",EDGE,"E490.filletArc");
            var Q4;
            Q4=sQuery(id+"F1.wireOp",EDGE,"E485");
            var Q5;
            Q5=sQuery(id+"F1.wireOp",EDGE,"E499.filletArc");
            var Q6;
            Q6=sQuery(id+"F1.wireOp",EDGE,"E493");
            var Q7;
            Q7=sQuery(id+"F1.wireOp",EDGE,"E504.filletArc");
            var Q8;
            Q8=sQuery(id+"F1.wireOp",EDGE,"E423");
            var Q9;
            Q9=sQuery(id+"F1.wireOp",EDGE,"E429.filletArc");
            var Q10;
            Q10=sQuery(id+"F1.wireOp",EDGE,"E505");
            var Q11;
            Q11=sQuery(id+"F1.wireOp",EDGE,"E430.filletArc");
            var Q12;
            Q12=sQuery(id+"F1.wireOp",EDGE,"E410");
            var Q13;
            Q13=sQuery(id+"F1.wireOp",EDGE,"E415.filletArc");
            var Q14;
            Q14=sQuery(id+"F1.wireOp",EDGE,"E410");
            var Q15;
            Q15=sQuery(id+"F1.wireOp",EDGE,"E409");
            var Q16;
            Q16=sQuery(id+"F1.wireOp",EDGE,"E420.filletArc");
            var Q17;
            Q17=sQuery(id+"F1.wireOp",EDGE,"E123");
            var Q18;
            Q18=sQuery(id+"F1.wireOp",EDGE,"E129.filletArc");
            var Q19;
            Q19=sQuery(id+"F1.wireOp",EDGE,"E397");
            var Q20;
            Q20=sQuery(id+"F1.wireOp",EDGE,"E125");
            var Q21;
            Q21=sQuery(id+"F1.wireOp",EDGE,"E130.filletArc");
            var Q22;
            Q22=sQuery(id+"F1.wireOp",EDGE,"E136");
            var Q23;
            Q23=sQuery(id+"F1.wireOp",EDGE,"E391.filletArc");
            var Q24;
            Q24=sQuery(id+"F1.wireOp",EDGE,"E396.filletArc");
            var Q25;
            Q25=sQuery(id+"F1.wireOp",EDGE,"E375");
            var Q26;
            Q26=sQuery(id+"F1.wireOp",EDGE,"E381.filletArc");
            var Q27;
            Q27=sQuery(id+"F1.wireOp",EDGE,"E541");
            var Q28;
            Q28=sQuery(id+"F1.wireOp",EDGE,"E382.filletArc");
            var Q29;
            Q29=sQuery(id+"F1.wireOp",EDGE,"E377");
            var Q30;
            Q30=sQuery(id+"F1.wireOp",EDGE,"E571.filletArc");
            var Q31;
            Q31=sQuery(id+"F1.wireOp",EDGE,"E364");
            var Q32;
            Q32=sQuery(id+"F1.wireOp",EDGE,"E370.filletArc");
            var Q33;
            Q33=sQuery(id+"F1.wireOp",EDGE,"E365");
            var Q34;
            Q34=sQuery(id+"F1.wireOp",EDGE,"E371.filletArc");
            var Q35;
            Q35=sQuery(id+"F1.wireOp",EDGE,"E591");
            sweep(context, id + "F13", {"operationType" : NewBodyOperationType.ADD, "profiles" : qUnion([Q0]), "path" : qUnion([Q1, Q2, Q3, Q4, Q5, Q6, Q7, Q8, Q9, Q10, Q11, Q12, Q13, Q14, Q15, Q16, Q17, Q18, Q19, Q20, Q21, Q22, Q23, Q24, Q25, Q26, Q27, Q28, Q29, Q30, Q31, Q32, Q33, Q34, Q35])});
        }
        {
            var Q0;
            Q0=sQuery(id+"F3.wireOp",VERTEX,"E967.end");
            var Q1;
            Q1=sQuery(id+"F3.wireOp",EDGE,"E967");
            cPlane(context, id + "F14", {"entities" : qUnion([Q0, Q1]), "cplaneType" : CPlaneType.LINE_POINT, "offset" : 25 * mm, "width" : 150 * mm, "height" : 150 * mm});
        }
        {
            var Q0;
            Q0=qCreatedBy(id+"F14.planeOp",FACE);
            var sketch = newSketch(context, id + "F15", { "sketchPlane" : qUnion([Q0])});
            skCircle(sketch, "E1539", {"center": v(7.8, 0.62) * mm, "radius": 0.2 * mm});
            skSolve(sketch);
        }
        {
            var Q0;
            Q0 = qSketchRegion(id + "F15", true);
            var Q1;
            Q1=sQuery(id+"F3.wireOp",EDGE,"E967");
            var Q2;
            Q2=sQuery(id+"F3.wireOp",EDGE,"E845");
            var Q3;
            Q3=sQuery(id+"F3.wireOp",EDGE,"E850.filletArc");
            var Q4;
            Q4=sQuery(id+"F3.wireOp",EDGE,"E844");
            var Q5;
            Q5=sQuery(id+"F3.wireOp",EDGE,"E949");
            var Q6;
            Q6=sQuery(id+"F3.wireOp",EDGE,"E836.filletArc");
            var Q7;
            Q7=sQuery(id+"F3.wireOp",EDGE,"E831");
            var Q8;
            Q8=sQuery(id+"F3.wireOp",EDGE,"E758");
            var Q9;
            Q9=sQuery(id+"F3.wireOp",EDGE,"E829.filletArc");
            var Q10;
            Q10=sQuery(id+"F3.wireOp",EDGE,"E812");
            var Q11;
            Q11=sQuery(id+"F3.wireOp",EDGE,"E926");
            var Q12;
            Q12=sQuery(id+"F3.wireOp",EDGE,"E747");
            var Q13;
            Q13=sQuery(id+"F3.wireOp",EDGE,"E818.filletArc");
            var Q14;
            Q14=sQuery(id+"F3.wireOp",EDGE,"E752.filletArc");
            var Q15;
            Q15=sQuery(id+"F3.wireOp",EDGE,"E761");
            var Q16;
            Q16=sQuery(id+"F3.wireOp",EDGE,"E766.filletArc");
            var Q17;
            Q17=sQuery(id+"F3.wireOp",EDGE,"E735");
            var Q18;
            Q18=sQuery(id+"F3.wireOp",EDGE,"E741.filletArc");
            var Q19;
            Q19=sQuery(id+"F3.wireOp",EDGE,"E771");
            var Q20;
            Q20=sQuery(id+"F3.wireOp",EDGE,"E777.filletArc");
            var Q21;
            Q21=sQuery(id+"F3.wireOp",EDGE,"E772");
            var Q22;
            Q22=sQuery(id+"F3.wireOp",EDGE,"E784.filletArc");
            var Q23;
            Q23=sQuery(id+"F3.wireOp",EDGE,"E784.filletArc");
            var Q24;
            Q24=sQuery(id+"F3.wireOp",EDGE,"E854");
            var Q25;
            Q25=sQuery(id+"F3.wireOp",EDGE,"E860.filletArc");
            var Q26;
            Q26=sQuery(id+"F3.wireOp",EDGE,"E855");
            var Q27;
            Q27=sQuery(id+"F3.wireOp",EDGE,"E970");
            var Q28;
            Q28=sQuery(id+"F3.wireOp",EDGE,"E982.filletArc");
            var Q29;
            Q29=sQuery(id+"F3.wireOp",EDGE,"E977");
            var Q30;
            Q30=sQuery(id+"F3.wireOp",EDGE,"E978");
            var Q31;
            Q31=sQuery(id+"F3.wireOp",EDGE,"E983.filletArc");
            var Q32;
            Q32=sQuery(id+"F3.wireOp",EDGE,"E986.filletArc");
            var Q33;
            Q33=sQuery(id+"F3.wireOp",EDGE,"E980");
            var Q34;
            Q34=sQuery(id+"F3.wireOp",EDGE,"E865");
            var Q35;
            Q35=sQuery(id+"F3.wireOp",EDGE,"E870.filletArc");
            var Q36;
            Q36=sQuery(id+"F3.wireOp",EDGE,"E864");
            var Q37;
            Q37=sQuery(id+"F3.wireOp",EDGE,"E877.filletArc");
            var Q38;
            Q38=sQuery(id+"F3.wireOp",EDGE,"E782");
            var Q39;
            Q39=sQuery(id+"F3.wireOp",EDGE,"E787.filletArc");
            var Q40;
            Q40=sQuery(id+"F3.wireOp",EDGE,"E781");
            var Q41;
            Q41=sQuery(id+"F3.wireOp",EDGE,"E795.filletArc");
            var Q42;
            Q42=sQuery(id+"F3.wireOp",EDGE,"E739");
            var Q43;
            Q43=sQuery(id+"F3.wireOp",EDGE,"E744.filletArc");
            var Q44;
            Q44=sQuery(id+"F3.wireOp",EDGE,"E801");
            var Q45;
            Q45=sQuery(id+"F3.wireOp",EDGE,"E805.filletArc");
            var Q46;
            Q46=sQuery(id+"F3.wireOp",EDGE,"E750");
            var Q47;
            Q47=sQuery(id+"F3.wireOp",EDGE,"E755.filletArc");
            var Q48;
            Q48=sQuery(id+"F3.wireOp",EDGE,"E749");
            var Q49;
            Q49=sQuery(id+"F3.wireOp",EDGE,"E919.filletArc");
            var Q50;
            Q50=sQuery(id+"F3.wireOp",EDGE,"E915");
            var Q51;
            Q51=sQuery(id+"F3.wireOp",EDGE,"E1061");
            var Q52;
            Q52=sQuery(id+"F3.wireOp",EDGE,"E922.filletArc");
            var Q53;
            Q53=sQuery(id+"F3.wireOp",EDGE,"E904");
            var Q54;
            Q54=sQuery(id+"F3.wireOp",EDGE,"E909.filletArc");
            var Q55;
            Q55=sQuery(id+"F3.wireOp",EDGE,"E802");
            var Q56;
            Q56=sQuery(id+"F3.wireOp",EDGE,"E808.filletArc");
            var Q57;
            Q57=sQuery(id+"F3.wireOp",EDGE,"E803");
            var Q58;
            Q58=sQuery(id+"F3.wireOp",EDGE,"E898.filletArc");
            var Q59;
            Q59=sQuery(id+"F3.wireOp",EDGE,"E894");
            var Q60;
            Q60=sQuery(id+"F3.wireOp",EDGE,"E798.filletArc");
            var Q61;
            Q61=sQuery(id+"F3.wireOp",EDGE,"E793");
            var Q62;
            Q62=sQuery(id+"F3.wireOp",EDGE,"E888.filletArc");
            var Q63;
            Q63=sQuery(id+"F3.wireOp",EDGE,"E883");
            var Q64;
            Q64=sQuery(id+"F3.wireOp",EDGE,"E880.filletArc");
            var Q65;
            Q65=sQuery(id+"F3.wireOp",EDGE,"E875");
            var Q66;
            Q66=sQuery(id+"F3.wireOp",EDGE,"E1012.filletArc");
            var Q67;
            Q67=sQuery(id+"F3.wireOp",EDGE,"E1007");
            var Q68;
            Q68=sQuery(id+"F3.wireOp",EDGE,"E1005.filletArc");
            var Q69;
            Q69=sQuery(id+"F3.wireOp",EDGE,"E1000");
            var Q70;
            Q70=sQuery(id+"F3.wireOp",EDGE,"E1009");
            var Q71;
            Q71=sQuery(id+"F3.wireOp",EDGE,"E1023.filletArc");
            var Q72;
            Q72=sQuery(id+"F3.wireOp",EDGE,"E886");
            var Q73;
            Q73=sQuery(id+"F3.wireOp",EDGE,"E891.filletArc");
            var Q74;
            Q74=sQuery(id+"F3.wireOp",EDGE,"E885");
            var Q75;
            Q75=sQuery(id+"F3.wireOp",EDGE,"E1033.filletArc");
            var Q76;
            Q76=sQuery(id+"F3.wireOp",EDGE,"E896");
            var Q77;
            Q77=sQuery(id+"F3.wireOp",EDGE,"E901.filletArc");
            var Q78;
            Q78=sQuery(id+"F3.wireOp",EDGE,"E895");
            var Q79;
            Q79=sQuery(id+"F3.wireOp",EDGE,"E1043.filletArc");
            var Q80;
            Q80=sQuery(id+"F3.wireOp",EDGE,"E907");
            var Q81;
            Q81=sQuery(id+"F3.wireOp",EDGE,"E912.filletArc");
            var Q82;
            Q82=sQuery(id+"F3.wireOp",EDGE,"E1050");
            var Q83;
            Q83=sQuery(id+"F3.wireOp",EDGE,"E932.filletArc");
            var Q84;
            Q84=sQuery(id+"F3.wireOp",EDGE,"E927");
            var Q85;
            Q85=sQuery(id+"F3.wireOp",EDGE,"E1060");
            var Q86;
            Q86=sQuery(id+"F3.wireOp",EDGE,"E1064.filletArc");
            var Q87;
            Q87=sQuery(id+"F3.wireOp",EDGE,"E1054.filletArc");
            var Q88;
            Q88=sQuery(id+"F3.wireOp",EDGE,"E1049");
            var Q89;
            Q89=sQuery(id+"F3.wireOp",EDGE,"E1051");
            var Q90;
            Q90=sQuery(id+"F3.wireOp",EDGE,"E1057.filletArc");
            var Q91;
            Q91=sQuery(id+"F3.wireOp",EDGE,"E1052");
            var Q92;
            Q92=sQuery(id+"F3.wireOp",EDGE,"E1124.filletArc");
            var Q93;
            Q93=sQuery(id+"F3.wireOp",EDGE,"E1040");
            var Q94;
            Q94=sQuery(id+"F3.wireOp",EDGE,"E1046.filletArc");
            var Q95;
            Q95=sQuery(id+"F3.wireOp",EDGE,"E1041");
            var Q96;
            Q96=sQuery(id+"F3.wireOp",EDGE,"E1134.filletArc");
            var Q97;
            Q97=sQuery(id+"F3.wireOp",EDGE,"E1129");
            var Q98;
            Q98=sQuery(id+"F3.wireOp",EDGE,"E1036.filletArc");
            var Q99;
            Q99=sQuery(id+"F3.wireOp",EDGE,"E1031");
            var Q100;
            Q100=sQuery(id+"F3.wireOp",EDGE,"E1144.filletArc");
            var Q101;
            Q101=sQuery(id+"F3.wireOp",EDGE,"E1020");
            var Q102;
            Q102=sQuery(id+"F3.wireOp",EDGE,"E1026.filletArc");
            var Q103;
            Q103=sQuery(id+"F3.wireOp",EDGE,"E1021");
            var Q104;
            Q104=sQuery(id+"F3.wireOp",EDGE,"E972.filletArc");
            var Q105;
            Q105=sQuery(id+"F3.wireOp",EDGE,"E960");
            var Q106;
            Q106=sQuery(id+"F3.wireOp",EDGE,"E965.filletArc");
            var Q107;
            Q107=sQuery(id+"F3.wireOp",EDGE,"E842");
            var Q108;
            Q108=sQuery(id+"F3.wireOp",EDGE,"E847.filletArc");
            var Q109;
            Q109=sQuery(id+"F3.wireOp",EDGE,"E841");
            var Q110;
            Q110=sQuery(id+"F3.wireOp",EDGE,"E954.filletArc");
            var Q111;
            Q111=sQuery(id+"F3.wireOp",EDGE,"E1076.filletArc");
            var Q112;
            Q112=sQuery(id+"F3.wireOp",EDGE,"E1071");
            var Q113;
            Q113=sQuery(id+"F3.wireOp",EDGE,"E821");
            var Q114;
            Q114=sQuery(id+"F3.wireOp",EDGE,"E825.filletArc");
            var Q115;
            Q115=sQuery(id+"F3.wireOp",EDGE,"E820");
            var Q116;
            Q116=sQuery(id+"F3.wireOp",EDGE,"E828.filletArc");
            var Q117;
            Q117=sQuery(id+"F3.wireOp",EDGE,"E826.filletArc");
            var Q118;
            Q118=sQuery(id+"F3.wireOp",EDGE,"E763.filletArc");
            var Q119;
            Q119=sQuery(id+"F3.wireOp",EDGE,"E759");
            var Q120;
            Q120=sQuery(id+"F3.wireOp",EDGE,"E839.filletArc");
            var Q121;
            Q121=sQuery(id+"F3.wireOp",EDGE,"E768");
            var Q122;
            Q122=sQuery(id+"F3.wireOp",EDGE,"E774.filletArc");
            var Q123;
            Q123=sQuery(id+"F3.wireOp",EDGE,"E857.filletArc");
            var Q124;
            Q124=sQuery(id+"F3.wireOp",EDGE,"E969");
            var Q125;
            Q125=sQuery(id+"F3.wireOp",EDGE,"E975.filletArc");
            var Q126;
            Q126=sQuery(id+"F3.wireOp",EDGE,"E985.filletArc");
            var Q127;
            Q127=sQuery(id+"F3.wireOp",EDGE,"E979");
            var Q128;
            Q128=sQuery(id+"F3.wireOp",EDGE,"E867.filletArc");
            var Q129;
            Q129=sQuery(id+"F3.wireOp",EDGE,"E929.filletArc");
            var Q130;
            Q130=sQuery(id+"F3.wireOp",EDGE,"E925");
            var Q131;
            Q131=sQuery(id+"F3.wireOp",EDGE,"E928.filletArc");
            var Q132;
            Q132=sQuery(id+"F3.wireOp",EDGE,"E924");
            var Q133;
            Q133=sQuery(id+"F3.wireOp",EDGE,"E931.filletArc");
            var Q134;
            Q134=sQuery(id+"F3.wireOp",EDGE,"E1002.filletArc");
            var Q135;
            Q135=sQuery(id+"F3.wireOp",EDGE,"E989");
            var Q136;
            Q136=sQuery(id+"F3.wireOp",EDGE,"E1063.filletArc");
            var Q137;
            Q137=sQuery(id+"F3.wireOp",EDGE,"E1059");
            var Q138;
            Q138=sQuery(id+"F3.wireOp",EDGE,"E1066.filletArc");
            var Q139;
            Q139=sQuery(id+"F3.wireOp",EDGE,"E1062");
            var Q140;
            Q140=sQuery(id+"F3.wireOp",EDGE,"E1067.filletArc");
            var Q141;
            Q141=sQuery(id+"F3.wireOp",EDGE,"E1056.filletArc");
            var Q142;
            Q142=sQuery(id+"F3.wireOp",EDGE,"E1048");
            var Q143;
            Q143=sQuery(id+"F3.wireOp",EDGE,"E1027.filletArc");
            var Q144;
            Q144=sQuery(id+"F3.wireOp",EDGE,"E1019");
            var Q145;
            Q145=sQuery(id+"F3.wireOp",EDGE,"E1024.filletArc");
            var Q146;
            Q146=sQuery(id+"F3.wireOp",EDGE,"E1006.filletArc");
            var Q147;
            Q147=sQuery(id+"F3.wireOp",EDGE,"E998");
            var Q148;
            Q148=sQuery(id+"F3.wireOp",EDGE,"E1003.filletArc");
            sweep(context, id + "F16", {"profiles" : qUnion([Q0]), "path" : qUnion([Q1, Q2, Q3, Q4, Q5, Q6, Q7, Q8, Q9, Q10, Q11, Q12, Q13, Q14, Q15, Q16, Q17, Q18, Q19, Q20, Q21, Q22, Q23, Q24, Q25, Q26, Q27, Q28, Q29, Q30, Q31, Q32, Q33, Q34, Q35, Q36, Q37, Q38, Q39, Q40, Q41, Q42, Q43, Q44, Q45, Q46, Q47, Q48, Q49, Q50, Q51, Q52, Q53, Q54, Q55, Q56, Q57, Q58, Q59, Q60, Q61, Q62, Q63, Q64, Q65, Q66, Q67, Q68, Q69, Q70, Q71, Q72, Q73, Q74, Q75, Q76, Q77, Q78, Q79, Q80, Q81, Q82, Q83, Q84, Q85, Q86, Q87, Q88, Q89, Q90, Q91, Q92, Q93, Q94, Q95, Q96, Q97, Q98, Q99, Q100, Q101, Q102, Q103, Q104, Q105, Q106, Q107, Q108, Q109, Q110, Q111, Q112, Q113, Q114, Q115, Q116, Q117, Q118, Q119, Q120, Q121, Q122, Q123, Q124, Q125, Q126, Q127, Q128, Q129, Q130, Q131, Q132, Q133, Q134, Q135, Q136, Q137, Q138, Q139, Q140, Q141, Q142, Q143, Q144, Q145, Q146, Q147, Q148])});
        }
        {
            var Q0;
            Q0 = qSketchRegion(id + "F15", true);
            var Q1;
            Q1=sQuery(id+"F3.wireOp",EDGE,"E973.filletArc");
            var Q2;
            Q2=sQuery(id+"F3.wireOp",EDGE,"E968");
            var Q3;
            Q3=sQuery(id+"F3.wireOp",EDGE,"E976.filletArc");
            var Q4;
            Q4=sQuery(id+"F3.wireOp",EDGE,"E970");
            var Q5;
            Q5=sQuery(id+"F3.wireOp",EDGE,"E981.filletArc");
            var Q6;
            Q6=sQuery(id+"F3.wireOp",EDGE,"E853");
            var Q7;
            Q7=sQuery(id+"F3.wireOp",EDGE,"E984.filletArc");
            var Q8;
            Q8=sQuery(id+"F3.wireOp",EDGE,"E979");
            var Q9;
            Q9=sQuery(id+"F3.wireOp",EDGE,"E985.filletArc");
            var Q10;
            Q10=sQuery(id+"F3.wireOp",EDGE,"E980");
            var Q11;
            Q11=sQuery(id+"F3.wireOp",EDGE,"E992.filletArc");
            var Q12;
            Q12=sQuery(id+"F3.wireOp",EDGE,"E987");
            var Q13;
            Q13=sQuery(id+"F3.wireOp",EDGE,"E993.filletArc");
            var Q14;
            Q14=sQuery(id+"F3.wireOp",EDGE,"E988");
            var Q15;
            Q15=sQuery(id+"F3.wireOp",EDGE,"E996.filletArc");
            var Q16;
            Q16=sQuery(id+"F3.wireOp",EDGE,"E990");
            var Q17;
            Q17=sQuery(id+"F3.wireOp",EDGE,"E995.filletArc");
            var Q18;
            Q18=sQuery(id+"F3.wireOp",EDGE,"E989");
            var Q19;
            Q19=sQuery(id+"F3.wireOp",EDGE,"E1002.filletArc");
            var Q20;
            Q20=sQuery(id+"F3.wireOp",EDGE,"E865");
            var Q21;
            Q21=sQuery(id+"F3.wireOp",EDGE,"E870.filletArc");
            var Q22;
            Q22=sQuery(id+"F3.wireOp",EDGE,"E864");
            var Q23;
            Q23=sQuery(id+"F3.wireOp",EDGE,"E869.filletArc");
            var Q24;
            Q24=sQuery(id+"F3.wireOp",EDGE,"E780");
            var Q25;
            Q25=sQuery(id+"F3.wireOp",EDGE,"E785.filletArc");
            var Q26;
            Q26=sQuery(id+"F3.wireOp",EDGE,"E854");
            var Q27;
            Q27=sQuery(id+"F3.wireOp",EDGE,"E859.filletArc");
            var Q28;
            Q28=sQuery(id+"F3.wireOp",EDGE,"E770");
            var Q29;
            Q29=sQuery(id+"F3.wireOp",EDGE,"E856.filletArc");
            var Q30;
            Q30=sQuery(id+"F3.wireOp",EDGE,"E845");
            var Q31;
            Q31=sQuery(id+"F3.wireOp",EDGE,"E851.filletArc");
            var Q32;
            Q32=sQuery(id+"F3.wireOp",EDGE,"E843");
            var Q33;
            Q33=sQuery(id+"F3.wireOp",EDGE,"E848.filletArc");
            var Q34;
            Q34=sQuery(id+"F3.wireOp",EDGE,"E842");
            var Q35;
            Q35=sQuery(id+"F3.wireOp",EDGE,"E847.filletArc");
            var Q36;
            Q36=sQuery(id+"F3.wireOp",EDGE,"E841");
            var Q37;
            Q37=sQuery(id+"F3.wireOp",EDGE,"E846.filletArc");
            var Q38;
            Q38=sQuery(id+"F3.wireOp",EDGE,"E833");
            var Q39;
            Q39=sQuery(id+"F3.wireOp",EDGE,"E840.filletArc");
            var Q40;
            Q40=sQuery(id+"F3.wireOp",EDGE,"E768");
            var Q41;
            Q41=sQuery(id+"F3.wireOp",EDGE,"E839.filletArc");
            var Q42;
            Q42=sQuery(id+"F3.wireOp",EDGE,"E759");
            var Q43;
            Q43=sQuery(id+"F3.wireOp",EDGE,"E838.filletArc");
            var Q44;
            Q44=sQuery(id+"F3.wireOp",EDGE,"E823");
            var Q45;
            Q45=sQuery(id+"F3.wireOp",EDGE,"E827.filletArc");
            var Q46;
            Q46=sQuery(id+"F3.wireOp",EDGE,"E1071");
            var Q47;
            Q47=sQuery(id+"F3.wireOp",EDGE,"E826.filletArc");
            var Q48;
            Q48=sQuery(id+"F3.wireOp",EDGE,"E821");
            var Q49;
            Q49=sQuery(id+"F3.wireOp",EDGE,"E825.filletArc");
            var Q50;
            Q50=sQuery(id+"F3.wireOp",EDGE,"E820");
            var Q51;
            Q51=sQuery(id+"F3.wireOp",EDGE,"E1117.filletArc");
            var Q52;
            Q52=sQuery(id+"F3.wireOp",EDGE,"E811");
            var Q53;
            Q53=sQuery(id+"F3.wireOp",EDGE,"E810");
            var Q54;
            Q54=sQuery(id+"F3.wireOp",EDGE,"E814.filletArc");
            var Q55;
            Q55=sQuery(id+"F3.wireOp",EDGE,"E821");
            var Q56;
            Q56=sQuery(id+"F3.wireOp",EDGE,"E817.filletArc");
            var Q57;
            Q57=sQuery(id+"F3.wireOp",EDGE,"E926");
            var Q58;
            Q58=sQuery(id+"F3.wireOp",EDGE,"E930.filletArc");
            var Q59;
            Q59=sQuery(id+"F3.wireOp",EDGE,"E746");
            var Q60;
            Q60=sQuery(id+"F3.wireOp",EDGE,"E915");
            var Q61;
            Q61=sQuery(id+"F3.wireOp",EDGE,"E933.filletArc");
            var Q62;
            Q62=sQuery(id+"F3.wireOp",EDGE,"E932.filletArc");
            var Q63;
            Q63=sQuery(id+"F3.wireOp",EDGE,"E927");
            var Q64;
            Q64=sQuery(id+"F3.wireOp",EDGE,"E1083.filletArc");
            var Q65;
            Q65=sQuery(id+"F3.wireOp",EDGE,"E1079");
            var Q66;
            Q66=sQuery(id+"F3.wireOp",EDGE,"E1082.filletArc");
            var Q67;
            Q67=sQuery(id+"F3.wireOp",EDGE,"E1078");
            var Q68;
            Q68=sQuery(id+"F3.wireOp",EDGE,"E1085.filletArc");
            var Q69;
            Q69=sQuery(id+"F3.wireOp",EDGE,"E1081");
            var Q70;
            Q70=sQuery(id+"F3.wireOp",EDGE,"E1086.filletArc");
            var Q71;
            Q71=sQuery(id+"F3.wireOp",EDGE,"E1060");
            var Q72;
            Q72=sQuery(id+"F3.wireOp",EDGE,"E1064.filletArc");
            var Q73;
            Q73=sQuery(id+"F3.wireOp",EDGE,"E1061");
            var Q74;
            Q74=sQuery(id+"F3.wireOp",EDGE,"E1065.filletArc");
            var Q75;
            Q75=sQuery(id+"F3.wireOp",EDGE,"E903");
            var Q76;
            Q76=sQuery(id+"F3.wireOp",EDGE,"E1068.filletArc");
            var Q77;
            Q77=sQuery(id+"F3.wireOp",EDGE,"E1049");
            var Q78;
            Q78=sQuery(id+"F3.wireOp",EDGE,"E1053.filletArc");
            var Q79;
            Q79=sQuery(id+"F3.wireOp",EDGE,"E1048");
            var Q80;
            Q80=sQuery(id+"F3.wireOp",EDGE,"E1056.filletArc");
            var Q81;
            Q81=sQuery(id+"F3.wireOp",EDGE,"E1051");
            var Q82;
            Q82=sQuery(id+"F3.wireOp",EDGE,"E1057.filletArc");
            var Q83;
            Q83=sQuery(id+"F3.wireOp",EDGE,"E1052");
            var Q84;
            Q84=sQuery(id+"F3.wireOp",EDGE,"E1058.filletArc");
            var Q85;
            Q85=sQuery(id+"F3.wireOp",EDGE,"E1038");
            var Q86;
            Q86=sQuery(id+"F3.wireOp",EDGE,"E1042.filletArc");
            var Q87;
            Q87=sQuery(id+"F3.wireOp",EDGE,"E907");
            var Q88;
            Q88=sQuery(id+"F3.wireOp",EDGE,"E913.filletArc");
            var Q89;
            Q89=sQuery(id+"F3.wireOp",EDGE,"E893");
            var Q90;
            Q90=sQuery(id+"F3.wireOp",EDGE,"E910.filletArc");
            var Q91;
            Q91=sQuery(id+"F3.wireOp",EDGE,"E802");
            var Q92;
            Q92=sQuery(id+"F3.wireOp",EDGE,"E807.filletArc");
            var Q93;
            Q93=sQuery(id+"F3.wireOp",EDGE,"E800");
            var Q94;
            Q94=sQuery(id+"F3.wireOp",EDGE,"E804.filletArc");
            var Q95;
            Q95=sQuery(id+"F3.wireOp",EDGE,"E750");
            var Q96;
            Q96=sQuery(id+"F3.wireOp",EDGE,"E756.filletArc");
            var Q97;
            Q97=sQuery(id+"F3.wireOp",EDGE,"E734");
            var Q98;
            Q98=sQuery(id+"F3.wireOp",EDGE,"E740.filletArc");
            var Q99;
            Q99=sQuery(id+"F3.wireOp",EDGE,"E735");
            var Q100;
            Q100=sQuery(id+"F3.wireOp",EDGE,"E741.filletArc");
            var Q101;
            Q101=sQuery(id+"F3.wireOp",EDGE,"E771");
            var Q102;
            Q102=sQuery(id+"F3.wireOp",EDGE,"E742.filletArc");
            var Q103;
            Q103=sQuery(id+"F3.wireOp",EDGE,"E737");
            var Q104;
            Q104=sQuery(id+"F3.wireOp",EDGE,"E786.filletArc");
            var Q105;
            Q105=sQuery(id+"F3.wireOp",EDGE,"E781");
            var Q106;
            Q106=sQuery(id+"F3.wireOp",EDGE,"E796.filletArc");
            var Q107;
            Q107=sQuery(id+"F3.wireOp",EDGE,"E791");
            var Q108;
            Q108=sQuery(id+"F3.wireOp",EDGE,"E879.filletArc");
            var Q109;
            Q109=sQuery(id+"F3.wireOp",EDGE,"E883");
            var Q110;
            Q110=sQuery(id+"F3.wireOp",EDGE,"E880.filletArc");
            var Q111;
            Q111=sQuery(id+"F3.wireOp",EDGE,"E1012.filletArc");
            var Q112;
            Q112=sQuery(id+"F3.wireOp",EDGE,"E875");
            var Q113;
            Q113=sQuery(id+"F3.wireOp",EDGE,"E1007");
            var Q114;
            Q114=sQuery(id+"F3.wireOp",EDGE,"E1013.filletArc");
            var Q115;
            Q115=sQuery(id+"F3.wireOp",EDGE,"E1008");
            var Q116;
            Q116=sQuery(id+"F3.wireOp",EDGE,"E1016.filletArc");
            var Q117;
            Q117=sQuery(id+"F3.wireOp",EDGE,"E1010");
            var Q118;
            Q118=sQuery(id+"F3.wireOp",EDGE,"E1015.filletArc");
            var Q119;
            Q119=sQuery(id+"F3.wireOp",EDGE,"E1009");
            var Q120;
            Q120=sQuery(id+"F3.wireOp",EDGE,"E1023.filletArc");
            var Q121;
            Q121=sQuery(id+"F3.wireOp",EDGE,"E886");
            var Q122;
            Q122=sQuery(id+"F3.wireOp",EDGE,"E1022.filletArc");
            var Q123;
            Q123=sQuery(id+"F3.wireOp",EDGE,"E1017");
            var Q124;
            Q124=sQuery(id+"F3.wireOp",EDGE,"E1037.filletArc");
            var Q125;
            Q125=sQuery(id+"F3.wireOp",EDGE,"E1031");
            var Q126;
            Q126=sQuery(id+"F3.wireOp",EDGE,"E1036.filletArc");
            var Q127;
            Q127=sQuery(id+"F3.wireOp",EDGE,"E1129");
            var Q128;
            Q128=sQuery(id+"F3.wireOp",EDGE,"E1028");
            var Q129;
            Q129=sQuery(id+"F3.wireOp",EDGE,"E1035.filletArc");
            var Q130;
            Q130=sQuery(id+"F3.wireOp",EDGE,"E1032.filletArc");
            var Q131;
            Q131=sQuery(id+"F3.wireOp",EDGE,"E896");
            var Q132;
            Q132=sQuery(id+"F3.wireOp",EDGE,"E902.filletArc");
            var Q133;
            Q133=sQuery(id+"F3.wireOp",EDGE,"E882");
            var Q134;
            Q134=sQuery(id+"F3.wireOp",EDGE,"E899.filletArc");
            var Q135;
            Q135=sQuery(id+"F3.wireOp",EDGE,"E894");
            var Q136;
            Q136=sQuery(id+"F3.wireOp",EDGE,"E797.filletArc");
            var Q137;
            Q137=sQuery(id+"F3.wireOp",EDGE,"E789");
            var Q138;
            Q138=sQuery(id+"F3.wireOp",EDGE,"E806.filletArc");
            sweep(context, id + "F17", {"operationType" : NewBodyOperationType.ADD, "profiles" : qUnion([Q0]), "path" : qUnion([Q1, Q2, Q3, Q4, Q5, Q6, Q7, Q8, Q9, Q10, Q11, Q12, Q13, Q14, Q15, Q16, Q17, Q18, Q19, Q20, Q21, Q22, Q23, Q24, Q25, Q26, Q27, Q28, Q29, Q30, Q31, Q32, Q33, Q34, Q35, Q36, Q37, Q38, Q39, Q40, Q41, Q42, Q43, Q44, Q45, Q46, Q47, Q48, Q49, Q50, Q51, Q52, Q53, Q54, Q55, Q56, Q57, Q58, Q59, Q60, Q61, Q62, Q63, Q64, Q65, Q66, Q67, Q68, Q69, Q70, Q71, Q72, Q73, Q74, Q75, Q76, Q77, Q78, Q79, Q80, Q81, Q82, Q83, Q84, Q85, Q86, Q87, Q88, Q89, Q90, Q91, Q92, Q93, Q94, Q95, Q96, Q97, Q98, Q99, Q100, Q101, Q102, Q103, Q104, Q105, Q106, Q107, Q108, Q109, Q110, Q111, Q112, Q113, Q114, Q115, Q116, Q117, Q118, Q119, Q120, Q121, Q122, Q123, Q124, Q125, Q126, Q127, Q128, Q129, Q130, Q131, Q132, Q133, Q134, Q135, Q136, Q137, Q138])});
        }
        {
            var Q0;
            Q0 = qSketchRegion(id + "F15", true);
            var Q1;
            Q1=sQuery(id+"F3.wireOp",EDGE,"E967");
            var Q2;
            Q2=sQuery(id+"F3.wireOp",EDGE,"E972.filletArc");
            var Q3;
            Q3=sQuery(id+"F3.wireOp",EDGE,"E960");
            var Q4;
            Q4=sQuery(id+"F3.wireOp",EDGE,"E971.filletArc");
            var Q5;
            Q5=sQuery(id+"F3.wireOp",EDGE,"E843");
            var Q6;
            Q6=sQuery(id+"F3.wireOp",EDGE,"E851.filletArc");
            var Q7;
            Q7=sQuery(id+"F3.wireOp",EDGE,"E845");
            var Q8;
            Q8=sQuery(id+"F3.wireOp",EDGE,"E856.filletArc");
            var Q9;
            Q9=sQuery(id+"F3.wireOp",EDGE,"E770");
            var Q10;
            Q10=sQuery(id+"F3.wireOp",EDGE,"E778.filletArc");
            var Q11;
            Q11=sQuery(id+"F3.wireOp",EDGE,"E772");
            var Q12;
            Q12=sQuery(id+"F3.wireOp",EDGE,"E777.filletArc");
            var Q13;
            Q13=sQuery(id+"F3.wireOp",EDGE,"E771");
            var Q14;
            Q14=sQuery(id+"F3.wireOp",EDGE,"E760");
            var Q15;
            Q15=sQuery(id+"F3.wireOp",EDGE,"E776.filletArc");
            var Q16;
            Q16=sQuery(id+"F3.wireOp",EDGE,"E764.filletArc");
            var Q17;
            Q17=sQuery(id+"F3.wireOp",EDGE,"E759");
            var Q18;
            Q18=sQuery(id+"F3.wireOp",EDGE,"E763.filletArc");
            var Q19;
            Q19=sQuery(id+"F3.wireOp",EDGE,"E758");
            var Q20;
            Q20=sQuery(id+"F3.wireOp",EDGE,"E762.filletArc");
            var Q21;
            Q21=sQuery(id+"F3.wireOp",EDGE,"E757");
            var Q22;
            Q22=sQuery(id+"F3.wireOp",EDGE,"E765.filletArc");
            var Q23;
            Q23=sQuery(id+"F3.wireOp",EDGE,"E761");
            var Q24;
            Q24=sQuery(id+"F3.wireOp",EDGE,"E753.filletArc");
            var Q25;
            Q25=sQuery(id+"F3.wireOp",EDGE,"E734");
            var Q26;
            Q26=sQuery(id+"F3.wireOp",EDGE,"E743.filletArc");
            var Q27;
            Q27=sQuery(id+"F3.wireOp",EDGE,"E801");
            var Q28;
            Q28=sQuery(id+"F3.wireOp",EDGE,"E744.filletArc");
            var Q29;
            Q29=sQuery(id+"F3.wireOp",EDGE,"E739");
            var Q30;
            Q30=sQuery(id+"F3.wireOp",EDGE,"E795.filletArc");
            var Q31;
            Q31=sQuery(id+"F3.wireOp",EDGE,"E781");
            var Q32;
            Q32=sQuery(id+"F3.wireOp",EDGE,"E787.filletArc");
            var Q33;
            Q33=sQuery(id+"F3.wireOp",EDGE,"E782");
            var Q34;
            Q34=sQuery(id+"F3.wireOp",EDGE,"E788.filletArc");
            var Q35;
            Q35=sQuery(id+"F3.wireOp",EDGE,"E780");
            var Q36;
            Q36=sQuery(id+"F3.wireOp",EDGE,"E866.filletArc");
            var Q37;
            Q37=sQuery(id+"F3.wireOp",EDGE,"E855");
            var Q38;
            Q38=sQuery(id+"F3.wireOp",EDGE,"E867.filletArc");
            var Q39;
            Q39=sQuery(id+"F3.wireOp",EDGE,"E979");
            var Q40;
            Q40=sQuery(id+"F3.wireOp",EDGE,"E868.filletArc");
            var Q41;
            Q41=sQuery(id+"F3.wireOp",EDGE,"E863");
            var Q42;
            Q42=sQuery(id+"F3.wireOp",EDGE,"E871.filletArc");
            var Q43;
            Q43=sQuery(id+"F3.wireOp",EDGE,"E865");
            var Q44;
            Q44=sQuery(id+"F3.wireOp",EDGE,"E1001.filletArc");
            var Q45;
            Q45=sQuery(id+"F3.wireOp",EDGE,"E873");
            var Q46;
            Q46=sQuery(id+"F3.wireOp",EDGE,"E881.filletArc");
            var Q47;
            Q47=sQuery(id+"F3.wireOp",EDGE,"E875");
            var Q48;
            Q48=sQuery(id+"F3.wireOp",EDGE,"E1011.filletArc");
            var Q49;
            Q49=sQuery(id+"F3.wireOp",EDGE,"E884");
            var Q50;
            Q50=sQuery(id+"F3.wireOp",EDGE,"E892.filletArc");
            var Q51;
            Q51=sQuery(id+"F3.wireOp",EDGE,"E886");
            var Q52;
            Q52=sQuery(id+"F3.wireOp",EDGE,"E891.filletArc");
            var Q53;
            Q53=sQuery(id+"F3.wireOp",EDGE,"E885");
            var Q54;
            Q54=sQuery(id+"F3.wireOp",EDGE,"E1033.filletArc");
            var Q55;
            Q55=sQuery(id+"F3.wireOp",EDGE,"E896");
            var Q56;
            Q56=sQuery(id+"F3.wireOp",EDGE,"E901.filletArc");
            var Q57;
            Q57=sQuery(id+"F3.wireOp",EDGE,"E895");
            var Q58;
            Q58=sQuery(id+"F3.wireOp",EDGE,"E893");
            var Q59;
            Q59=sQuery(id+"F3.wireOp",EDGE,"E900.filletArc");
            var Q60;
            Q60=sQuery(id+"F3.wireOp",EDGE,"E910.filletArc");
            var Q61;
            Q61=sQuery(id+"F3.wireOp",EDGE,"E802");
            var Q62;
            Q62=sQuery(id+"F3.wireOp",EDGE,"E909.filletArc");
            var Q63;
            Q63=sQuery(id+"F3.wireOp",EDGE,"E904");
            var Q64;
            Q64=sQuery(id+"F3.wireOp",EDGE,"E922.filletArc");
            var Q65;
            Q65=sQuery(id+"F3.wireOp",EDGE,"E1061");
            var Q66;
            Q66=sQuery(id+"F3.wireOp",EDGE,"E921.filletArc");
            var Q67;
            Q67=sQuery(id+"F3.wireOp",EDGE,"E914");
            var Q68;
            Q68=sQuery(id+"F3.wireOp",EDGE,"E918.filletArc");
            var Q69;
            Q69=sQuery(id+"F3.wireOp",EDGE,"E915");
            sweep(context, id + "F18", {"operationType" : NewBodyOperationType.ADD, "profiles" : qUnion([Q0]), "path" : qUnion([Q1, Q2, Q3, Q4, Q5, Q6, Q7, Q8, Q9, Q10, Q11, Q12, Q13, Q14, Q15, Q16, Q17, Q18, Q19, Q20, Q21, Q22, Q23, Q24, Q25, Q26, Q27, Q28, Q29, Q30, Q31, Q32, Q33, Q34, Q35, Q36, Q37, Q38, Q39, Q40, Q41, Q42, Q43, Q44, Q45, Q46, Q47, Q48, Q49, Q50, Q51, Q52, Q53, Q54, Q55, Q56, Q57, Q58, Q59, Q60, Q61, Q62, Q63, Q64, Q65, Q66, Q67, Q68, Q69])});
        }
        {
            var Q0;
            Q0=sQuery(id+"F5.wireOp",EDGE,"E1324");
            var Q1;
            Q1=sQuery(id+"F5.wireOp",VERTEX,"E1324.end");
            cPlane(context, id + "F19", {"entities" : qUnion([Q0, Q1]), "cplaneType" : CPlaneType.LINE_POINT, "offset" : 25 * mm, "width" : 150 * mm, "height" : 150 * mm});
        }
        {
            var Q0;
            Q0=qCreatedBy(id+"F19.planeOp",FACE);
            var sketch = newSketch(context, id + "F20", { "sketchPlane" : qUnion([Q0])});
            skCircle(sketch, "E1540", {"center": v(4.8, 1.03) * mm, "radius": 0.2 * mm});
            skSolve(sketch);
        }
        {
            var Q0;
            Q0 = qSketchRegion(id + "F20", true);
            var Q1;
            Q1=sQuery(id+"F5.wireOp",EDGE,"E1324");
            var Q2;
            Q2=sQuery(id+"F5.wireOp",EDGE,"E1329.filletArc");
            var Q3;
            Q3=sQuery(id+"F5.wireOp",EDGE,"E1314");
            var Q4;
            Q4=sQuery(id+"F5.wireOp",EDGE,"E1320.filletArc");
            var Q5;
            Q5=sQuery(id+"F5.wireOp",EDGE,"E1209.filletArc");
            var Q6;
            Q6=sQuery(id+"F5.wireOp",EDGE,"E1203");
            var Q7;
            Q7=sQuery(id+"F5.wireOp",EDGE,"E1315");
            var Q8;
            Q8=sQuery(id+"F5.wireOp",EDGE,"E1308.filletArc");
            var Q9;
            Q9=sQuery(id+"F5.wireOp",EDGE,"E1216");
            var Q10;
            Q10=sQuery(id+"F5.wireOp",EDGE,"E1221.filletArc");
            var Q11;
            Q11=sQuery(id+"F5.wireOp",EDGE,"E1215");
            var Q12;
            Q12=sQuery(id+"F5.wireOp",EDGE,"E1220.filletArc");
            var Q13;
            Q13=sQuery(id+"F5.wireOp",EDGE,"E1214");
            var Q14;
            Q14=sQuery(id+"F5.wireOp",EDGE,"E1283.filletArc");
            var Q15;
            Q15=sQuery(id+"F5.wireOp",EDGE,"E1278");
            var Q16;
            Q16=sQuery(id+"F5.wireOp",EDGE,"E1232.filletArc");
            var Q17;
            Q17=sQuery(id+"F5.wireOp",EDGE,"E1409");
            var Q18;
            Q18=sQuery(id+"F5.wireOp",EDGE,"E1415.filletArc");
            var Q19;
            Q19=sQuery(id+"F5.wireOp",EDGE,"E1395");
            var Q20;
            Q20=sQuery(id+"F5.wireOp",EDGE,"E1400.filletArc");
            var Q21;
            Q21=sQuery(id+"F5.wireOp",EDGE,"E1394");
            var Q22;
            Q22=sQuery(id+"F5.wireOp",EDGE,"E1394");
            var Q23;
            Q23=sQuery(id+"F5.wireOp",EDGE,"E1405.filletArc");
            var Q24;
            Q24=sQuery(id+"F5.wireOp",EDGE,"E1399");
            var Q25;
            Q25=sQuery(id+"F5.wireOp",EDGE,"E1404.filletArc");
            var Q26;
            Q26=sQuery(id+"F5.wireOp",EDGE,"E1383");
            var Q27;
            Q27=sQuery(id+"F5.wireOp",EDGE,"E1403.filletArc");
            var Q28;
            Q28=sQuery(id+"F5.wireOp",EDGE,"E1238");
            var Q29;
            Q29=sQuery(id+"F5.wireOp",EDGE,"E1244.filletArc");
            var Q30;
            Q30=sQuery(id+"F5.wireOp",EDGE,"E1230");
            var Q31;
            Q31=sQuery(id+"F5.wireOp",EDGE,"E1235.filletArc");
            var Q32;
            Q32=sQuery(id+"F5.wireOp",EDGE,"E1190");
            var Q33;
            Q33=sQuery(id+"F5.wireOp",EDGE,"E1196.filletArc");
            var Q34;
            Q34=sQuery(id+"F5.wireOp",EDGE,"E1191");
            var Q35;
            Q35=sQuery(id+"F5.wireOp",EDGE,"E1197.filletArc");
            var Q36;
            Q36=sQuery(id+"F5.wireOp",EDGE,"E1192");
            var Q37;
            Q37=sQuery(id+"F5.wireOp",EDGE,"E1212.filletArc");
            var Q38;
            Q38=sQuery(id+"F5.wireOp",EDGE,"E1263");
            var Q39;
            Q39=sQuery(id+"F5.wireOp",EDGE,"E1269.filletArc");
            var Q40;
            Q40=sQuery(id+"F5.wireOp",EDGE,"E1264");
            var Q41;
            Q41=sQuery(id+"F5.wireOp",EDGE,"E1347");
            var Q42;
            Q42=sQuery(id+"F5.wireOp",EDGE,"E1272.filletArc");
            var Q43;
            Q43=sQuery(id+"F5.wireOp",EDGE,"E1252");
            var Q44;
            Q44=sQuery(id+"F5.wireOp",EDGE,"E1257.filletArc");
            var Q45;
            Q45=sQuery(id+"F5.wireOp",EDGE,"E1251");
            var Q46;
            Q46=sQuery(id+"F5.wireOp",EDGE,"E1256.filletArc");
            var Q47;
            Q47=sQuery(id+"F5.wireOp",EDGE,"E1250");
            var Q48;
            Q48=sQuery(id+"F5.wireOp",EDGE,"E1372");
            var Q49;
            Q49=sQuery(id+"F5.wireOp",EDGE,"E1261.filletArc");
            var Q50;
            Q50=sQuery(id+"F5.wireOp",EDGE,"E1260.filletArc");
            var Q51;
            Q51=sQuery(id+"F5.wireOp",EDGE,"E1359");
            var Q52;
            Q52=sQuery(id+"F5.wireOp",EDGE,"E1259.filletArc");
            var Q53;
            Q53=sQuery(id+"F5.wireOp",EDGE,"E1346");
            var Q54;
            Q54=sQuery(id+"F5.wireOp",EDGE,"E1270.filletArc");
            var Q55;
            Q55=sQuery(id+"F5.wireOp",EDGE,"E1265");
            var Q56;
            Q56=sQuery(id+"F5.wireOp",EDGE,"E1271.filletArc");
            sweep(context, id + "F21", {"profiles" : qUnion([Q0]), "path" : qUnion([Q1, Q2, Q3, Q4, Q5, Q6, Q7, Q8, Q9, Q10, Q11, Q12, Q13, Q14, Q15, Q16, Q17, Q18, Q19, Q20, Q21, Q22, Q23, Q24, Q25, Q26, Q27, Q28, Q29, Q30, Q31, Q32, Q33, Q34, Q35, Q36, Q37, Q38, Q39, Q40, Q41, Q42, Q43, Q44, Q45, Q46, Q47, Q48, Q49, Q50, Q51, Q52, Q53, Q54, Q55, Q56])});
        }
        {
            var Q0;
            Q0 = qSketchRegion(id + "F20", true);
            var Q1;
            Q1=sQuery(id+"F5.wireOp",EDGE,"E1330.filletArc");
            var Q2;
            Q2=sQuery(id+"F5.wireOp",EDGE,"E1325");
            var Q3;
            Q3=sQuery(id+"F5.wireOp",EDGE,"E1331.filletArc");
            var Q4;
            Q4=sQuery(id+"F5.wireOp",EDGE,"E1326");
            var Q5;
            Q5=sQuery(id+"F5.wireOp",EDGE,"E1332.filletArc");
            var Q6;
            Q6=sQuery(id+"F5.wireOp",EDGE,"E1264");
            var Q7;
            Q7=sQuery(id+"F5.wireOp",EDGE,"E1333.filletArc");
            var Q8;
            Q8=sQuery(id+"F5.wireOp",EDGE,"E1205");
            var Q9;
            Q9=sQuery(id+"F5.wireOp",EDGE,"E1210.filletArc");
            var Q10;
            Q10=sQuery(id+"F5.wireOp",EDGE,"E1315");
            var Q11;
            Q11=sQuery(id+"F5.wireOp",EDGE,"E1209.filletArc");
            var Q12;
            Q12=sQuery(id+"F5.wireOp",EDGE,"E1203");
            var Q13;
            Q13=sQuery(id+"F5.wireOp",EDGE,"E1208.filletArc");
            var Q14;
            Q14=sQuery(id+"F5.wireOp",EDGE,"E1202");
            var Q15;
            Q15=sQuery(id+"F5.wireOp",EDGE,"E1233.filletArc");
            var Q16;
            Q16=sQuery(id+"F5.wireOp",EDGE,"E1278");
            var Q17;
            Q17=sQuery(id+"F5.wireOp",EDGE,"E1232.filletArc");
            var Q18;
            Q18=sQuery(id+"F5.wireOp",EDGE,"E1409");
            var Q19;
            Q19=sQuery(id+"F5.wireOp",EDGE,"E1237.filletArc");
            var Q20;
            Q20=sQuery(id+"F5.wireOp",EDGE,"E1396");
            var Q21;
            Q21=sQuery(id+"F5.wireOp",EDGE,"E1195");
            var Q22;
            Q22=sQuery(id+"F5.wireOp",EDGE,"E1250");
            var Q23;
            Q23=sQuery(id+"F5.wireOp",EDGE,"E1371");
            var Q24;
            Q24=sQuery(id+"F5.wireOp",EDGE,"E1247.filletArc");
            var Q25;
            Q25=sQuery(id+"F5.wireOp",EDGE,"E1248.filletArc");
            var Q26;
            Q26=sQuery(id+"F5.wireOp",EDGE,"E1243");
            var Q27;
            Q27=sQuery(id+"F5.wireOp",EDGE,"E1213.filletArc");
            var Q28;
            Q28=sQuery(id+"F5.wireOp",EDGE,"E1192");
            var Q29;
            Q29=sQuery(id+"F5.wireOp",EDGE,"E1198.filletArc");
            var Q30;
            Q30=sQuery(id+"F5.wireOp",EDGE,"E1193");
            var Q31;
            Q31=sQuery(id+"F5.wireOp",EDGE,"E1199.filletArc");
            var Q32;
            Q32=sQuery(id+"F5.wireOp",EDGE,"E1251");
            var Q33;
            Q33=sQuery(id+"F5.wireOp",EDGE,"E1200.filletArc");
            var Q34;
            Q34=sQuery(id+"F5.wireOp",EDGE,"E1190");
            var Q35;
            Q35=sQuery(id+"F5.wireOp",EDGE,"E1201.filletArc");
            var Q36;
            Q36=sQuery(id+"F5.wireOp",EDGE,"E1234.filletArc");
            var Q37;
            Q37=sQuery(id+"F5.wireOp",EDGE,"E1219");
            var Q38;
            Q38=sQuery(id+"F5.wireOp",EDGE,"E1402.filletArc");
            var Q39;
            Q39=sQuery(id+"F5.wireOp",EDGE,"E1238");
            var Q40;
            Q40=sQuery(id+"F5.wireOp",EDGE,"E1249.filletArc");
            sweep(context, id + "F22", {"operationType" : NewBodyOperationType.ADD, "profiles" : qUnion([Q0]), "path" : qUnion([Q1, Q2, Q3, Q4, Q5, Q6, Q7, Q8, Q9, Q10, Q11, Q12, Q13, Q14, Q15, Q16, Q17, Q18, Q19, Q20, Q21, Q22, Q23, Q24, Q25, Q26, Q27, Q28, Q29, Q30, Q31, Q32, Q33, Q34, Q35, Q36, Q37, Q38, Q39, Q40])});
        }
    });
